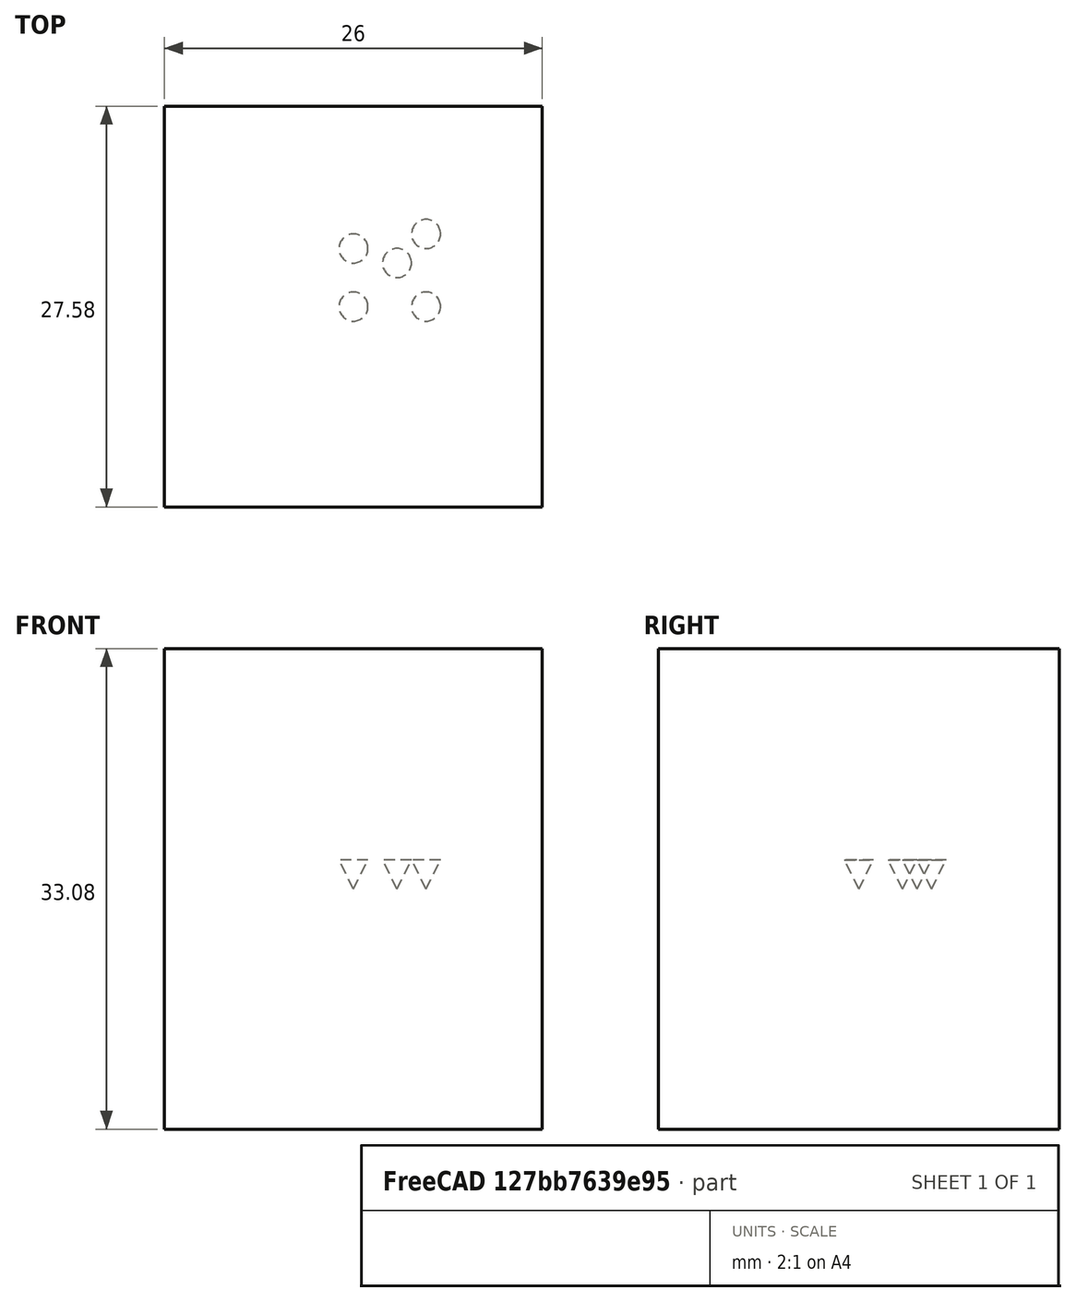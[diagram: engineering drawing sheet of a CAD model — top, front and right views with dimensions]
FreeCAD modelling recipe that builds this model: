
FCSTD DOCUMENT  (FreeCAD 1.0R39109 (Git))
Label: PointArray
License: All rights reserved
objects: App::DocumentObjectGroupPython×1251, Part::Vertex×5, Part::FeaturePython×2, App::Part×2, Part::Cone×1, Part::Compound×1
note: 9 computed .brp shape members not serialized (recipe doc carries the construction recipe); baked Part::Feature solids carry a one-line shape summary decoded from their .brp

FEATURE [App::DocumentObjectGroupPython] HALFPI  # scripted group (container) (typed FeaturePython)
  name = HALFPI
  value = pi/2.
FEATURE [App::DocumentObjectGroupPython] PI  # scripted group (container) (typed FeaturePython)
  name = PI
  value = 1.*pi
FEATURE [App::DocumentObjectGroupPython] TWOPI  # scripted group (container) (typed FeaturePython)
  name = TWOPI
  value = 2.*pi
FEATURE [App::DocumentObjectGroupPython] Constants  # scripted group (container) (typed FeaturePython)
  Group = -> [HALFPI,PI,TWOPI]
FEATURE [App::DocumentObjectGroupPython] Variables  # scripted group (container) (typed FeaturePython)
FEATURE [App::DocumentObjectGroupPython] Quantities  # scripted group (container) (typed FeaturePython)
FEATURE [App::DocumentObjectGroupPython] Isotopes  # scripted group (container) (typed FeaturePython)
FEATURE [App::DocumentObjectGroupPython] Elements  # scripted group (container) (typed FeaturePython)
FEATURE [App::DocumentObjectGroupPython] Matrix  # scripted group (container) (typed FeaturePython)
FEATURE [App::DocumentObjectGroupPython] Surfaces  # scripted group (container) (typed FeaturePython)
FEATURE [App::DocumentObjectGroupPython] Opticals  # scripted group (container) (typed FeaturePython)
  Group = -> [Matrix,Surfaces]
FEATURE [App::DocumentObjectGroupPython] G4Isotopes  # scripted group (container) (typed FeaturePython)
FEATURE [App::DocumentObjectGroupPython] H_element  # scripted group (container) (typed FeaturePython)
  Z = 1
  atom_value = 1.008
  formula = H
  name = H_element
FEATURE [App::DocumentObjectGroupPython] He_element  # scripted group (container) (typed FeaturePython)
  Z = 2
  atom_value = 4.0026
  formula = He
  name = He_element
FEATURE [App::DocumentObjectGroupPython] Li_element  # scripted group (container) (typed FeaturePython)
  Z = 3
  atom_value = 6.94
  formula = Li
  name = Li_element
FEATURE [App::DocumentObjectGroupPython] Be_element  # scripted group (container) (typed FeaturePython)
  Z = 4
  atom_value = 9.01218
  formula = Be
  name = Be_element
FEATURE [App::DocumentObjectGroupPython] B_element  # scripted group (container) (typed FeaturePython)
  Z = 5
  atom_value = 10.81
  formula = B
  name = B_element
FEATURE [App::DocumentObjectGroupPython] C_element  # scripted group (container) (typed FeaturePython)
  Z = 6
  atom_value = 12.011
  formula = C
  name = C_element
FEATURE [App::DocumentObjectGroupPython] N_element  # scripted group (container) (typed FeaturePython)
  Z = 7
  atom_value = 14.007
  formula = N
  name = N_element
FEATURE [App::DocumentObjectGroupPython] O_element  # scripted group (container) (typed FeaturePython)
  Z = 8
  atom_value = 15.999
  formula = O
  name = O_element
FEATURE [App::DocumentObjectGroupPython] F_element  # scripted group (container) (typed FeaturePython)
  Z = 9
  atom_value = 18.9984
  formula = F
  name = F_element
FEATURE [App::DocumentObjectGroupPython] Ne_element  # scripted group (container) (typed FeaturePython)
  Z = 10
  atom_value = 20.1797
  formula = Ne
  name = Ne_element
FEATURE [App::DocumentObjectGroupPython] Na_element  # scripted group (container) (typed FeaturePython)
  Z = 11
  atom_value = 22.9898
  formula = Na
  name = Na_element
FEATURE [App::DocumentObjectGroupPython] Mg_element  # scripted group (container) (typed FeaturePython)
  Z = 12
  atom_value = 24.305
  formula = Mg
  name = Mg_element
FEATURE [App::DocumentObjectGroupPython] Al_element  # scripted group (container) (typed FeaturePython)
  Z = 13
  atom_value = 26.9815
  formula = Al
  name = Al_element
FEATURE [App::DocumentObjectGroupPython] Si_element  # scripted group (container) (typed FeaturePython)
  Z = 14
  atom_value = 28.085
  formula = Si
  name = Si_element
FEATURE [App::DocumentObjectGroupPython] P_element  # scripted group (container) (typed FeaturePython)
  Z = 15
  atom_value = 30.9738
  formula = P
  name = P_element
FEATURE [App::DocumentObjectGroupPython] S_element  # scripted group (container) (typed FeaturePython)
  Z = 16
  atom_value = 32.06
  formula = S
  name = S_element
FEATURE [App::DocumentObjectGroupPython] Cl_element  # scripted group (container) (typed FeaturePython)
  Z = 17
  atom_value = 35.45
  formula = Cl
  name = Cl_element
FEATURE [App::DocumentObjectGroupPython] Ar_element  # scripted group (container) (typed FeaturePython)
  Z = 18
  atom_value = 39.95
  formula = Ar
  name = Ar_element
FEATURE [App::DocumentObjectGroupPython] K_element  # scripted group (container) (typed FeaturePython)
  Z = 19
  atom_value = 39.0983
  formula = K
  name = K_element
FEATURE [App::DocumentObjectGroupPython] Ca_element  # scripted group (container) (typed FeaturePython)
  Z = 20
  atom_value = 40.078
  formula = Ca
  name = Ca_element
FEATURE [App::DocumentObjectGroupPython] Sc_element  # scripted group (container) (typed FeaturePython)
  Z = 21
  atom_value = 44.9559
  formula = Sc
  name = Sc_element
FEATURE [App::DocumentObjectGroupPython] Ti_element  # scripted group (container) (typed FeaturePython)
  Z = 22
  atom_value = 47.867
  formula = Ti
  name = Ti_element
FEATURE [App::DocumentObjectGroupPython] V_element  # scripted group (container) (typed FeaturePython)
  Z = 23
  atom_value = 50.9415
  formula = V
  name = V_element
FEATURE [App::DocumentObjectGroupPython] Cr_element  # scripted group (container) (typed FeaturePython)
  Z = 24
  atom_value = 51.9961
  formula = Cr
  name = Cr_element
FEATURE [App::DocumentObjectGroupPython] Mn_element  # scripted group (container) (typed FeaturePython)
  Z = 25
  atom_value = 54.938
  formula = Mn
  name = Mn_element
FEATURE [App::DocumentObjectGroupPython] Fe_element  # scripted group (container) (typed FeaturePython)
  Z = 26
  atom_value = 55.845
  formula = Fe
  name = Fe_element
FEATURE [App::DocumentObjectGroupPython] Co_element  # scripted group (container) (typed FeaturePython)
  Z = 27
  atom_value = 58.9332
  formula = Co
  name = Co_element
FEATURE [App::DocumentObjectGroupPython] Ni_element  # scripted group (container) (typed FeaturePython)
  Z = 28
  atom_value = 58.6934
  formula = Ni
  name = Ni_element
FEATURE [App::DocumentObjectGroupPython] Cu_element  # scripted group (container) (typed FeaturePython)
  Z = 29
  atom_value = 63.546
  formula = Cu
  name = Cu_element
FEATURE [App::DocumentObjectGroupPython] Zn_element  # scripted group (container) (typed FeaturePython)
  Z = 30
  atom_value = 65.38
  formula = Zn
  name = Zn_element
FEATURE [App::DocumentObjectGroupPython] Ga_element  # scripted group (container) (typed FeaturePython)
  Z = 31
  atom_value = 69.723
  formula = Ga
  name = Ga_element
FEATURE [App::DocumentObjectGroupPython] Ge_element  # scripted group (container) (typed FeaturePython)
  Z = 32
  atom_value = 72.63
  formula = Ge
  name = Ge_element
FEATURE [App::DocumentObjectGroupPython] As_element  # scripted group (container) (typed FeaturePython)
  Z = 33
  atom_value = 74.9216
  formula = As
  name = As_element
FEATURE [App::DocumentObjectGroupPython] Se_element  # scripted group (container) (typed FeaturePython)
  Z = 34
  atom_value = 78.971
  formula = Se
  name = Se_element
FEATURE [App::DocumentObjectGroupPython] Br_element  # scripted group (container) (typed FeaturePython)
  Z = 35
  atom_value = 79.904
  formula = Br
  name = Br_element
FEATURE [App::DocumentObjectGroupPython] Kr_element  # scripted group (container) (typed FeaturePython)
  Z = 36
  atom_value = 83.798
  formula = Kr
  name = Kr_element
FEATURE [App::DocumentObjectGroupPython] Rb_element  # scripted group (container) (typed FeaturePython)
  Z = 37
  atom_value = 85.4678
  formula = Rb
  name = Rb_element
FEATURE [App::DocumentObjectGroupPython] Sr_element  # scripted group (container) (typed FeaturePython)
  Z = 38
  atom_value = 87.62
  formula = Sr
  name = Sr_element
FEATURE [App::DocumentObjectGroupPython] Y_element  # scripted group (container) (typed FeaturePython)
  Z = 39
  atom_value = 88.9058
  formula = Y
  name = Y_element
FEATURE [App::DocumentObjectGroupPython] Zr_element  # scripted group (container) (typed FeaturePython)
  Z = 40
  atom_value = 91.224
  formula = Zr
  name = Zr_element
FEATURE [App::DocumentObjectGroupPython] Nb_element  # scripted group (container) (typed FeaturePython)
  Z = 41
  atom_value = 92.9064
  formula = Nb
  name = Nb_element
FEATURE [App::DocumentObjectGroupPython] Mo_element  # scripted group (container) (typed FeaturePython)
  Z = 42
  atom_value = 95.95
  formula = Mo
  name = Mo_element
FEATURE [App::DocumentObjectGroupPython] Tc_element  # scripted group (container) (typed FeaturePython)
  Z = 43
  atom_value = 97
  formula = Tc
  name = Tc_element
FEATURE [App::DocumentObjectGroupPython] Ru_element  # scripted group (container) (typed FeaturePython)
  Z = 44
  atom_value = 101.07
  formula = Ru
  name = Ru_element
FEATURE [App::DocumentObjectGroupPython] Rh_element  # scripted group (container) (typed FeaturePython)
  Z = 45
  atom_value = 102.905
  formula = Rh
  name = Rh_element
FEATURE [App::DocumentObjectGroupPython] Pd_element  # scripted group (container) (typed FeaturePython)
  Z = 46
  atom_value = 106.42
  formula = Pd
  name = Pd_element
FEATURE [App::DocumentObjectGroupPython] Ag_element  # scripted group (container) (typed FeaturePython)
  Z = 47
  atom_value = 107.868
  formula = Ag
  name = Ag_element
FEATURE [App::DocumentObjectGroupPython] Cd_element  # scripted group (container) (typed FeaturePython)
  Z = 48
  atom_value = 112.414
  formula = Cd
  name = Cd_element
FEATURE [App::DocumentObjectGroupPython] In_element  # scripted group (container) (typed FeaturePython)
  Z = 49
  atom_value = 114.818
  formula = In
  name = In_element
FEATURE [App::DocumentObjectGroupPython] Sn_element  # scripted group (container) (typed FeaturePython)
  Z = 50
  atom_value = 118.71
  formula = Sn
  name = Sn_element
FEATURE [App::DocumentObjectGroupPython] Sb_element  # scripted group (container) (typed FeaturePython)
  Z = 51
  atom_value = 121.76
  formula = Sb
  name = Sb_element
FEATURE [App::DocumentObjectGroupPython] Te_element  # scripted group (container) (typed FeaturePython)
  Z = 52
  atom_value = 127.6
  formula = Te
  name = Te_element
FEATURE [App::DocumentObjectGroupPython] I_element  # scripted group (container) (typed FeaturePython)
  Z = 53
  atom_value = 126.904
  formula = I
  name = I_element
FEATURE [App::DocumentObjectGroupPython] Xe_element  # scripted group (container) (typed FeaturePython)
  Z = 54
  atom_value = 131.293
  formula = Xe
  name = Xe_element
FEATURE [App::DocumentObjectGroupPython] Cs_element  # scripted group (container) (typed FeaturePython)
  Z = 55
  atom_value = 132.905
  formula = Cs
  name = Cs_element
FEATURE [App::DocumentObjectGroupPython] Ba_element  # scripted group (container) (typed FeaturePython)
  Z = 56
  atom_value = 137.327
  formula = Ba
  name = Ba_element
FEATURE [App::DocumentObjectGroupPython] La_element  # scripted group (container) (typed FeaturePython)
  Z = 57
  atom_value = 138.905
  formula = La
  name = La_element
FEATURE [App::DocumentObjectGroupPython] Ce_element  # scripted group (container) (typed FeaturePython)
  Z = 58
  atom_value = 140.116
  formula = Ce
  name = Ce_element
FEATURE [App::DocumentObjectGroupPython] Pr_element  # scripted group (container) (typed FeaturePython)
  Z = 59
  atom_value = 140.908
  formula = Pr
  name = Pr_element
FEATURE [App::DocumentObjectGroupPython] Nd_element  # scripted group (container) (typed FeaturePython)
  Z = 60
  atom_value = 144.242
  formula = Nd
  name = Nd_element
FEATURE [App::DocumentObjectGroupPython] Pm_element  # scripted group (container) (typed FeaturePython)
  Z = 61
  atom_value = 145
  formula = Pm
  name = Pm_element
FEATURE [App::DocumentObjectGroupPython] Sm_element  # scripted group (container) (typed FeaturePython)
  Z = 62
  atom_value = 150.36
  formula = Sm
  name = Sm_element
FEATURE [App::DocumentObjectGroupPython] Eu_element  # scripted group (container) (typed FeaturePython)
  Z = 63
  atom_value = 151.964
  formula = Eu
  name = Eu_element
FEATURE [App::DocumentObjectGroupPython] Gd_element  # scripted group (container) (typed FeaturePython)
  Z = 64
  atom_value = 157.25
  formula = Gd
  name = Gd_element
FEATURE [App::DocumentObjectGroupPython] Tb_element  # scripted group (container) (typed FeaturePython)
  Z = 65
  atom_value = 158.925
  formula = Tb
  name = Tb_element
FEATURE [App::DocumentObjectGroupPython] Dy_element  # scripted group (container) (typed FeaturePython)
  Z = 66
  atom_value = 162.5
  formula = Dy
  name = Dy_element
FEATURE [App::DocumentObjectGroupPython] Ho_element  # scripted group (container) (typed FeaturePython)
  Z = 67
  atom_value = 164.93
  formula = Ho
  name = Ho_element
FEATURE [App::DocumentObjectGroupPython] Er_element  # scripted group (container) (typed FeaturePython)
  Z = 68
  atom_value = 167.259
  formula = Er
  name = Er_element
FEATURE [App::DocumentObjectGroupPython] Tm_element  # scripted group (container) (typed FeaturePython)
  Z = 69
  atom_value = 168.934
  formula = Tm
  name = Tm_element
FEATURE [App::DocumentObjectGroupPython] Yb_element  # scripted group (container) (typed FeaturePython)
  Z = 70
  atom_value = 173.045
  formula = Yb
  name = Yb_element
FEATURE [App::DocumentObjectGroupPython] Lu_element  # scripted group (container) (typed FeaturePython)
  Z = 71
  atom_value = 174.967
  formula = Lu
  name = Lu_element
FEATURE [App::DocumentObjectGroupPython] Hf_element  # scripted group (container) (typed FeaturePython)
  Z = 72
  atom_value = 178.49
  formula = Hf
  name = Hf_element
FEATURE [App::DocumentObjectGroupPython] Ta_element  # scripted group (container) (typed FeaturePython)
  Z = 73
  atom_value = 180.948
  formula = Ta
  name = Ta_element
FEATURE [App::DocumentObjectGroupPython] W_element  # scripted group (container) (typed FeaturePython)
  Z = 74
  atom_value = 183.84
  formula = W
  name = W_element
FEATURE [App::DocumentObjectGroupPython] Re_element  # scripted group (container) (typed FeaturePython)
  Z = 75
  atom_value = 186.207
  formula = Re
  name = Re_element
FEATURE [App::DocumentObjectGroupPython] Os_element  # scripted group (container) (typed FeaturePython)
  Z = 76
  atom_value = 190.23
  formula = Os
  name = Os_element
FEATURE [App::DocumentObjectGroupPython] Ir_element  # scripted group (container) (typed FeaturePython)
  Z = 77
  atom_value = 192.217
  formula = Ir
  name = Ir_element
FEATURE [App::DocumentObjectGroupPython] Pt_element  # scripted group (container) (typed FeaturePython)
  Z = 78
  atom_value = 195.084
  formula = Pt
  name = Pt_element
FEATURE [App::DocumentObjectGroupPython] Au_element  # scripted group (container) (typed FeaturePython)
  Z = 79
  atom_value = 196.967
  formula = Au
  name = Au_element
FEATURE [App::DocumentObjectGroupPython] Hg_element  # scripted group (container) (typed FeaturePython)
  Z = 80
  atom_value = 200.592
  formula = Hg
  name = Hg_element
FEATURE [App::DocumentObjectGroupPython] Tl_element  # scripted group (container) (typed FeaturePython)
  Z = 81
  atom_value = 204.38
  formula = Tl
  name = Tl_element
FEATURE [App::DocumentObjectGroupPython] Pb_element  # scripted group (container) (typed FeaturePython)
  Z = 82
  atom_value = 207.2
  formula = Pb
  name = Pb_element
FEATURE [App::DocumentObjectGroupPython] Bi_element  # scripted group (container) (typed FeaturePython)
  Z = 83
  atom_value = 208.98
  formula = Bi
  name = Bi_element
FEATURE [App::DocumentObjectGroupPython] Po_element  # scripted group (container) (typed FeaturePython)
  Z = 84
  atom_value = 209
  formula = Po
  name = Po_element
FEATURE [App::DocumentObjectGroupPython] At_element  # scripted group (container) (typed FeaturePython)
  Z = 85
  atom_value = 210
  formula = At
  name = At_element
FEATURE [App::DocumentObjectGroupPython] Rn_element  # scripted group (container) (typed FeaturePython)
  Z = 86
  atom_value = 222
  formula = Rn
  name = Rn_element
FEATURE [App::DocumentObjectGroupPython] Fr_element  # scripted group (container) (typed FeaturePython)
  Z = 87
  atom_value = 223
  formula = Fr
  name = Fr_element
FEATURE [App::DocumentObjectGroupPython] Ra_element  # scripted group (container) (typed FeaturePython)
  Z = 88
  atom_value = 226
  formula = Ra
  name = Ra_element
FEATURE [App::DocumentObjectGroupPython] Ac_element  # scripted group (container) (typed FeaturePython)
  Z = 89
  atom_value = 227
  formula = Ac
  name = Ac_element
FEATURE [App::DocumentObjectGroupPython] Th_element  # scripted group (container) (typed FeaturePython)
  Z = 90
  atom_value = 232.038
  formula = Th
  name = Th_element
FEATURE [App::DocumentObjectGroupPython] Pa_element  # scripted group (container) (typed FeaturePython)
  Z = 91
  atom_value = 231.036
  formula = Pa
  name = Pa_element
FEATURE [App::DocumentObjectGroupPython] U_element  # scripted group (container) (typed FeaturePython)
  Z = 92
  atom_value = 238.029
  formula = U
  name = U_element
FEATURE [App::DocumentObjectGroupPython] Np_element  # scripted group (container) (typed FeaturePython)
  Z = 93
  atom_value = 237
  formula = Np
  name = Np_element
FEATURE [App::DocumentObjectGroupPython] Pu_element  # scripted group (container) (typed FeaturePython)
  Z = 94
  atom_value = 244
  formula = Pu
  name = Pu_element
FEATURE [App::DocumentObjectGroupPython] Am_element  # scripted group (container) (typed FeaturePython)
  Z = 95
  atom_value = 243
  formula = Am
  name = Am_element
FEATURE [App::DocumentObjectGroupPython] Cm_element  # scripted group (container) (typed FeaturePython)
  Z = 96
  atom_value = 247
  formula = Cm
  name = Cm_element
FEATURE [App::DocumentObjectGroupPython] Bk_element  # scripted group (container) (typed FeaturePython)
  Z = 97
  atom_value = 247
  formula = Bk
  name = Bk_element
FEATURE [App::DocumentObjectGroupPython] Cf_element  # scripted group (container) (typed FeaturePython)
  Z = 98
  atom_value = 251
  formula = Cf
  name = Cf_element
FEATURE [App::DocumentObjectGroupPython] G4Elements  # scripted group (container) (typed FeaturePython)
  Group = -> [H_element,He_element,Li_element,Be_element,B_element,C_element,N_element,O_element,F_element,Ne_element,Na_element,Mg_element,Al_element,Si_element,P_element,S_element,Cl_element,Ar_element,K_element,Ca_element,Sc_element,Ti_element,V_element,Cr_element,Mn_element,Fe_element,Co_element,Ni_element,Cu_element,Zn_element,Ga_element,Ge_element,As_element,Se_element,Br_element,Kr_element,Rb_element,+61 more]
FEATURE [App::DocumentObjectGroupPython] H_element001  label="H_element : 0.101"  # scripted group (container) (typed FeaturePython)
  n = 0.101327
FEATURE [App::DocumentObjectGroupPython] C_element001  label="C_element : 0.775"  # scripted group (container) (typed FeaturePython)
  n = 0.7755
FEATURE [App::DocumentObjectGroupPython] N_element001  label="N_element : 0.035"  # scripted group (container) (typed FeaturePython)
  n = 0.035057
FEATURE [App::DocumentObjectGroupPython] O_element001  label="O_element : 0.052"  # scripted group (container) (typed FeaturePython)
  n = 0.0523159
FEATURE [App::DocumentObjectGroupPython] F_element001  label="F_element : 0.017"  # scripted group (container) (typed FeaturePython)
  n = 0.017422
FEATURE [App::DocumentObjectGroupPython] Ca_element001  label="Ca_element : 0.018"  # scripted group (container) (typed FeaturePython)
  n = 0.018378
FEATURE [App::DocumentObjectGroupPython] G4_A_150_TISSUE  label="G4_A-150_TISSUE"  # scripted group (container) (typed FeaturePython)
  Dunit = g/cm3
  Dvalue = 1.127
  Group = -> [H_element001,C_element001,N_element001,O_element001,F_element001,Ca_element001]
  conduct = 2
  density = 1
  expand = 3
  formula = G4_A-150_TISSUE
  name = G4_A-150_TISSUE
  specific = 4
FEATURE [App::DocumentObjectGroupPython] C_element002  label="C_element : 3"  # scripted group (container) (typed FeaturePython)
  n = 3
  ref = C_element
FEATURE [App::DocumentObjectGroupPython] H_element002  label="H_element : 6"  # scripted group (container) (typed FeaturePython)
  n = 6
  ref = H_element
FEATURE [App::DocumentObjectGroupPython] O_element002  label="O_element : 1"  # scripted group (container) (typed FeaturePython)
  n = 1
  ref = O_element
FEATURE [App::DocumentObjectGroupPython] G4_ACETONE  # scripted group (container) (typed FeaturePython)
  Dunit = g/cm3
  Dvalue = 0.7899
  Group = -> [C_element002,H_element002,O_element002]
  conduct = 2
  density = 1
  expand = 3
  formula = G4_ACETONE
  name = G4_ACETONE
  specific = 4
FEATURE [App::DocumentObjectGroupPython] C_element003  label="C_element : 2"  # scripted group (container) (typed FeaturePython)
  n = 2
  ref = C_element
FEATURE [App::DocumentObjectGroupPython] H_element003  label="H_element : 2"  # scripted group (container) (typed FeaturePython)
  n = 2
  ref = H_element
FEATURE [App::DocumentObjectGroupPython] G4_ACETYLENE  # scripted group (container) (typed FeaturePython)
  Dunit = g/cm3
  Dvalue = 0.0010967
  Group = -> [C_element003,H_element003]
  conduct = 2
  density = 1
  expand = 3
  formula = G4_ACETYLENE
  name = G4_ACETYLENE
  specific = 4
FEATURE [App::DocumentObjectGroupPython] C_element004  label="C_element : 5"  # scripted group (container) (typed FeaturePython)
  n = 5
  ref = C_element
FEATURE [App::DocumentObjectGroupPython] H_element004  label="H_element : 5"  # scripted group (container) (typed FeaturePython)
  n = 5
  ref = H_element
FEATURE [App::DocumentObjectGroupPython] N_element002  label="N_element : 5"  # scripted group (container) (typed FeaturePython)
  n = 5
  ref = N_element
FEATURE [App::DocumentObjectGroupPython] G4_ADENINE  # scripted group (container) (typed FeaturePython)
  Dunit = g/cm3
  Dvalue = 1.6
  Group = -> [C_element004,H_element004,N_element002]
  conduct = 2
  density = 1
  expand = 3
  formula = G4_ADENINE
  name = G4_ADENINE
  specific = 4
FEATURE [App::DocumentObjectGroupPython] H_element005  label="H_element : 0.114"  # scripted group (container) (typed FeaturePython)
  n = 0.114
FEATURE [App::DocumentObjectGroupPython] C_element005  label="C_element : 0.598"  # scripted group (container) (typed FeaturePython)
  n = 0.598
FEATURE [App::DocumentObjectGroupPython] N_element003  label="N_element : 0.007"  # scripted group (container) (typed FeaturePython)
  n = 0.007
FEATURE [App::DocumentObjectGroupPython] O_element003  label="O_element : 0.278"  # scripted group (container) (typed FeaturePython)
  n = 0.278
FEATURE [App::DocumentObjectGroupPython] Na_element001  label="Na_element : 0.001"  # scripted group (container) (typed FeaturePython)
  n = 0.001
FEATURE [App::DocumentObjectGroupPython] S_element001  label="S_element : 0.001"  # scripted group (container) (typed FeaturePython)
  n = 0.001
FEATURE [App::DocumentObjectGroupPython] Cl_element001  label="Cl_element : 0.001"  # scripted group (container) (typed FeaturePython)
  n = 0.001
FEATURE [App::DocumentObjectGroupPython] G4_ADIPOSE_TISSUE_ICRP  # scripted group (container) (typed FeaturePython)
  Dunit = g/cm3
  Dvalue = 0.95
  Group = -> [H_element005,C_element005,N_element003,O_element003,Na_element001,S_element001,Cl_element001]
  conduct = 2
  density = 1
  expand = 3
  formula = G4_ADIPOSE_TISSUE_ICRP
  name = G4_ADIPOSE_TISSUE_ICRP
  specific = 4
FEATURE [App::DocumentObjectGroupPython] C_element006  label="C_element : 0.000"  # scripted group (container) (typed FeaturePython)
  n = 0.000124
FEATURE [App::DocumentObjectGroupPython] N_element004  label="N_element : 0.755"  # scripted group (container) (typed FeaturePython)
  n = 0.755268
FEATURE [App::DocumentObjectGroupPython] O_element004  label="O_element : 0.232"  # scripted group (container) (typed FeaturePython)
  n = 0.231781
FEATURE [App::DocumentObjectGroupPython] Ar_element001  label="Ar_element : 0.013"  # scripted group (container) (typed FeaturePython)
  n = 0.012827
FEATURE [App::DocumentObjectGroupPython] G4_AIR  # scripted group (container) (typed FeaturePython)
  Dunit = g/cm3
  Dvalue = 0.00120479
  Group = -> [C_element006,N_element004,O_element004,Ar_element001]
  conduct = 2
  density = 1
  expand = 3
  formula = G4_AIR
  name = G4_AIR
  specific = 4
FEATURE [App::DocumentObjectGroupPython] C_element007  label="C_element : 006"  # scripted group (container) (typed FeaturePython)
  n = 3
  ref = C_element
FEATURE [App::DocumentObjectGroupPython] H_element006  label="H_element : 7"  # scripted group (container) (typed FeaturePython)
  n = 7
  ref = H_element
FEATURE [App::DocumentObjectGroupPython] N_element005  label="N_element : 1"  # scripted group (container) (typed FeaturePython)
  n = 1
  ref = N_element
FEATURE [App::DocumentObjectGroupPython] O_element005  label="O_element : 2"  # scripted group (container) (typed FeaturePython)
  n = 2
  ref = O_element
FEATURE [App::DocumentObjectGroupPython] G4_ALANINE  # scripted group (container) (typed FeaturePython)
  Dunit = g/cm3
  Dvalue = 1.42
  Group = -> [C_element007,H_element006,N_element005,O_element005]
  conduct = 2
  density = 1
  expand = 3
  formula = G4_ALANINE
  name = G4_ALANINE
  specific = 4
FEATURE [App::DocumentObjectGroupPython] Al_element001  label="Al_element : 2"  # scripted group (container) (typed FeaturePython)
  n = 2
  ref = Al_element
FEATURE [App::DocumentObjectGroupPython] O_element006  label="O_element : 3"  # scripted group (container) (typed FeaturePython)
  n = 3
  ref = O_element
FEATURE [App::DocumentObjectGroupPython] G4_ALUMINUM_OXIDE  # scripted group (container) (typed FeaturePython)
  Dunit = g/cm3
  Dvalue = 3.97
  Group = -> [Al_element001,O_element006]
  conduct = 2
  density = 1
  expand = 3
  formula = G4_ALUMINUM_OXIDE
  name = G4_ALUMINUM_OXIDE
  specific = 4
FEATURE [App::DocumentObjectGroupPython] H_element007  label="H_element : 0.106"  # scripted group (container) (typed FeaturePython)
  n = 0.10593
FEATURE [App::DocumentObjectGroupPython] C_element008  label="C_element : 0.789"  # scripted group (container) (typed FeaturePython)
  n = 0.788974
FEATURE [App::DocumentObjectGroupPython] O_element007  label="O_element : 0.105"  # scripted group (container) (typed FeaturePython)
  n = 0.105096
FEATURE [App::DocumentObjectGroupPython] G4_AMBER  # scripted group (container) (typed FeaturePython)
  Dunit = g/cm3
  Dvalue = 1.1
  Group = -> [H_element007,C_element008,O_element007]
  conduct = 2
  density = 1
  expand = 3
  formula = G4_AMBER
  name = G4_AMBER
  specific = 4
FEATURE [App::DocumentObjectGroupPython] N_element006  label="N_element : 006"  # scripted group (container) (typed FeaturePython)
  n = 1
  ref = N_element
FEATURE [App::DocumentObjectGroupPython] H_element008  label="H_element : 3"  # scripted group (container) (typed FeaturePython)
  n = 3
  ref = H_element
FEATURE [App::DocumentObjectGroupPython] G4_AMMONIA  # scripted group (container) (typed FeaturePython)
  Dunit = g/cm3
  Dvalue = 0.000826019
  Group = -> [N_element006,H_element008]
  conduct = 2
  density = 1
  expand = 3
  formula = G4_AMMONIA
  name = G4_AMMONIA
  specific = 4
FEATURE [App::DocumentObjectGroupPython] C_element009  label="C_element : 6"  # scripted group (container) (typed FeaturePython)
  n = 6
  ref = C_element
FEATURE [App::DocumentObjectGroupPython] H_element009  label="H_element : 008"  # scripted group (container) (typed FeaturePython)
  n = 7
  ref = H_element
FEATURE [App::DocumentObjectGroupPython] N_element007  label="N_element : 007"  # scripted group (container) (typed FeaturePython)
  n = 1
  ref = N_element
FEATURE [App::DocumentObjectGroupPython] G4_ANILINE  # scripted group (container) (typed FeaturePython)
  Dunit = g/cm3
  Dvalue = 1.0235
  Group = -> [C_element009,H_element009,N_element007]
  conduct = 2
  density = 1
  expand = 3
  formula = G4_ANILINE
  name = G4_ANILINE
  specific = 4
FEATURE [App::DocumentObjectGroupPython] C_element010  label="C_element : 14"  # scripted group (container) (typed FeaturePython)
  n = 14
  ref = C_element
FEATURE [App::DocumentObjectGroupPython] H_element010  label="H_element : 10"  # scripted group (container) (typed FeaturePython)
  n = 10
  ref = H_element
FEATURE [App::DocumentObjectGroupPython] G4_ANTHRACENE  # scripted group (container) (typed FeaturePython)
  Dunit = g/cm3
  Dvalue = 1.283
  Group = -> [C_element010,H_element010]
  conduct = 2
  density = 1
  expand = 3
  formula = G4_ANTHRACENE
  name = G4_ANTHRACENE
  specific = 4
FEATURE [App::DocumentObjectGroupPython] H_element011  label="H_element : 0.065"  # scripted group (container) (typed FeaturePython)
  n = 0.0654709
FEATURE [App::DocumentObjectGroupPython] C_element011  label="C_element : 0.537"  # scripted group (container) (typed FeaturePython)
  n = 0.536944
FEATURE [App::DocumentObjectGroupPython] N_element008  label="N_element : 0.021"  # scripted group (container) (typed FeaturePython)
  n = 0.0215
FEATURE [App::DocumentObjectGroupPython] O_element008  label="O_element : 0.032"  # scripted group (container) (typed FeaturePython)
  n = 0.032085
FEATURE [App::DocumentObjectGroupPython] F_element002  label="F_element : 0.167"  # scripted group (container) (typed FeaturePython)
  n = 0.167411
FEATURE [App::DocumentObjectGroupPython] Ca_element002  label="Ca_element : 0.177"  # scripted group (container) (typed FeaturePython)
  n = 0.176589
FEATURE [App::DocumentObjectGroupPython] G4_B_100_BONE  label="G4_B-100_BONE"  # scripted group (container) (typed FeaturePython)
  Dunit = g/cm3
  Dvalue = 1.45
  Group = -> [H_element011,C_element011,N_element008,O_element008,F_element002,Ca_element002]
  conduct = 2
  density = 1
  expand = 3
  formula = G4_B-100_BONE
  name = G4_B-100_BONE
  specific = 4
FEATURE [App::DocumentObjectGroupPython] H_element012  label="H_element : 0.057"  # scripted group (container) (typed FeaturePython)
  n = 0.057441
FEATURE [App::DocumentObjectGroupPython] C_element012  label="C_element : 0.790"  # scripted group (container) (typed FeaturePython)
  n = 0.774591
FEATURE [App::DocumentObjectGroupPython] O_element009  label="O_element : 0.168"  # scripted group (container) (typed FeaturePython)
  n = 0.167968
FEATURE [App::DocumentObjectGroupPython] G4_BAKELITE  # scripted group (container) (typed FeaturePython)
  Dunit = g/cm3
  Dvalue = 1.25
  Group = -> [H_element012,C_element012,O_element009]
  conduct = 2
  density = 1
  expand = 3
  formula = G4_BAKELITE
  name = G4_BAKELITE
  specific = 4
FEATURE [App::DocumentObjectGroupPython] Ba_element001  label="Ba_element : 1"  # scripted group (container) (typed FeaturePython)
  n = 1
  ref = Ba_element
FEATURE [App::DocumentObjectGroupPython] F_element003  label="F_element : 2"  # scripted group (container) (typed FeaturePython)
  n = 2
  ref = F_element
FEATURE [App::DocumentObjectGroupPython] G4_BARIUM_FLUORIDE  # scripted group (container) (typed FeaturePython)
  Dunit = g/cm3
  Dvalue = 4.89
  Group = -> [Ba_element001,F_element003]
  conduct = 2
  density = 1
  expand = 3
  formula = G4_BARIUM_FLUORIDE
  name = G4_BARIUM_FLUORIDE
  specific = 4
FEATURE [App::DocumentObjectGroupPython] Ba_element002  label="Ba_element : 002"  # scripted group (container) (typed FeaturePython)
  n = 1
  ref = Ba_element
FEATURE [App::DocumentObjectGroupPython] S_element002  label="S_element : 1"  # scripted group (container) (typed FeaturePython)
  n = 1
  ref = S_element
FEATURE [App::DocumentObjectGroupPython] O_element010  label="O_element : 4"  # scripted group (container) (typed FeaturePython)
  n = 4
  ref = O_element
FEATURE [App::DocumentObjectGroupPython] G4_BARIUM_SULFATE  # scripted group (container) (typed FeaturePython)
  Dunit = g/cm3
  Dvalue = 4.5
  Group = -> [Ba_element002,S_element002,O_element010]
  conduct = 2
  density = 1
  expand = 3
  formula = G4_BARIUM_SULFATE
  name = G4_BARIUM_SULFATE
  specific = 4
FEATURE [App::DocumentObjectGroupPython] C_element013  label="C_element : 007"  # scripted group (container) (typed FeaturePython)
  n = 6
  ref = C_element
FEATURE [App::DocumentObjectGroupPython] H_element013  label="H_element : 009"  # scripted group (container) (typed FeaturePython)
  n = 6
  ref = H_element
FEATURE [App::DocumentObjectGroupPython] G4_BENZENE  # scripted group (container) (typed FeaturePython)
  Dunit = g/cm3
  Dvalue = 0.87865
  Group = -> [C_element013,H_element013]
  conduct = 2
  density = 1
  expand = 3
  formula = G4_BENZENE
  name = G4_BENZENE
  specific = 4
FEATURE [App::DocumentObjectGroupPython] Be_element001  label="Be_element : 1"  # scripted group (container) (typed FeaturePython)
  n = 1
  ref = Be_element
FEATURE [App::DocumentObjectGroupPython] O_element011  label="O_element : 005"  # scripted group (container) (typed FeaturePython)
  n = 1
  ref = O_element
FEATURE [App::DocumentObjectGroupPython] G4_BERYLLIUM_OXIDE  # scripted group (container) (typed FeaturePython)
  Dunit = g/cm3
  Dvalue = 3.01
  Group = -> [Be_element001,O_element011]
  conduct = 2
  density = 1
  expand = 3
  formula = G4_BERYLLIUM_OXIDE
  name = G4_BERYLLIUM_OXIDE
  specific = 4
FEATURE [App::DocumentObjectGroupPython] Bi_element001  label="Bi_element : 4"  # scripted group (container) (typed FeaturePython)
  n = 4
  ref = Bi_element
FEATURE [App::DocumentObjectGroupPython] Ge_element001  label="Ge_element : 3"  # scripted group (container) (typed FeaturePython)
  n = 3
  ref = Ge_element
FEATURE [App::DocumentObjectGroupPython] O_element012  label="O_element : 12"  # scripted group (container) (typed FeaturePython)
  n = 12
  ref = O_element
FEATURE [App::DocumentObjectGroupPython] G4_BGO  # scripted group (container) (typed FeaturePython)
  Dunit = g/cm3
  Dvalue = 7.13
  Group = -> [Bi_element001,Ge_element001,O_element012]
  conduct = 2
  density = 1
  expand = 3
  formula = G4_BGO
  name = G4_BGO
  specific = 4
FEATURE [App::DocumentObjectGroupPython] H_element014  label="H_element : 0.102"  # scripted group (container) (typed FeaturePython)
  n = 0.102
FEATURE [App::DocumentObjectGroupPython] C_element014  label="C_element : 0.110"  # scripted group (container) (typed FeaturePython)
  n = 0.11
FEATURE [App::DocumentObjectGroupPython] N_element009  label="N_element : 0.033"  # scripted group (container) (typed FeaturePython)
  n = 0.033
FEATURE [App::DocumentObjectGroupPython] O_element013  label="O_element : 0.745"  # scripted group (container) (typed FeaturePython)
  n = 0.745
FEATURE [App::DocumentObjectGroupPython] Na_element002  label="Na_element : 0.002"  # scripted group (container) (typed FeaturePython)
  n = 0.001
FEATURE [App::DocumentObjectGroupPython] P_element001  label="P_element : 0.001"  # scripted group (container) (typed FeaturePython)
  n = 0.001
FEATURE [App::DocumentObjectGroupPython] S_element003  label="S_element : 0.002"  # scripted group (container) (typed FeaturePython)
  n = 0.002
FEATURE [App::DocumentObjectGroupPython] Cl_element002  label="Cl_element : 0.003"  # scripted group (container) (typed FeaturePython)
  n = 0.003
FEATURE [App::DocumentObjectGroupPython] K_element001  label="K_element : 0.002"  # scripted group (container) (typed FeaturePython)
  n = 0.002
FEATURE [App::DocumentObjectGroupPython] Fe_element001  label="Fe_element : 0.001"  # scripted group (container) (typed FeaturePython)
  n = 0.001
FEATURE [App::DocumentObjectGroupPython] G4_BLOOD_ICRP  # scripted group (container) (typed FeaturePython)
  Dunit = g/cm3
  Dvalue = 1.06
  Group = -> [H_element014,C_element014,N_element009,O_element013,Na_element002,P_element001,S_element003,Cl_element002,K_element001,Fe_element001]
  conduct = 2
  density = 1
  expand = 3
  formula = G4_BLOOD_ICRP
  name = G4_BLOOD_ICRP
  specific = 4
FEATURE [App::DocumentObjectGroupPython] H_element015  label="H_element : 0.064"  # scripted group (container) (typed FeaturePython)
  n = 0.064
FEATURE [App::DocumentObjectGroupPython] C_element015  label="C_element : 0.278"  # scripted group (container) (typed FeaturePython)
  n = 0.278
FEATURE [App::DocumentObjectGroupPython] N_element010  label="N_element : 0.027"  # scripted group (container) (typed FeaturePython)
  n = 0.027
FEATURE [App::DocumentObjectGroupPython] O_element014  label="O_element : 0.410"  # scripted group (container) (typed FeaturePython)
  n = 0.41
FEATURE [App::DocumentObjectGroupPython] Mg_element001  label="Mg_element : 0.002"  # scripted group (container) (typed FeaturePython)
  n = 0.002
FEATURE [App::DocumentObjectGroupPython] P_element002  label="P_element : 0.070"  # scripted group (container) (typed FeaturePython)
  n = 0.07
FEATURE [App::DocumentObjectGroupPython] S_element004  label="S_element : 0.003"  # scripted group (container) (typed FeaturePython)
  n = 0.002
FEATURE [App::DocumentObjectGroupPython] Ca_element003  label="Ca_element : 0.147"  # scripted group (container) (typed FeaturePython)
  n = 0.147
FEATURE [App::DocumentObjectGroupPython] G4_BONE_COMPACT_ICRU  # scripted group (container) (typed FeaturePython)
  Dunit = g/cm3
  Dvalue = 1.85
  Group = -> [H_element015,C_element015,N_element010,O_element014,Mg_element001,P_element002,S_element004,Ca_element003]
  conduct = 2
  density = 1
  expand = 3
  formula = G4_BONE_COMPACT_ICRU
  name = G4_BONE_COMPACT_ICRU
  specific = 4
FEATURE [App::DocumentObjectGroupPython] H_element016  label="H_element : 0.034"  # scripted group (container) (typed FeaturePython)
  n = 0.034
FEATURE [App::DocumentObjectGroupPython] C_element016  label="C_element : 0.155"  # scripted group (container) (typed FeaturePython)
  n = 0.155
FEATURE [App::DocumentObjectGroupPython] N_element011  label="N_element : 0.042"  # scripted group (container) (typed FeaturePython)
  n = 0.042
FEATURE [App::DocumentObjectGroupPython] O_element015  label="O_element : 0.435"  # scripted group (container) (typed FeaturePython)
  n = 0.435
FEATURE [App::DocumentObjectGroupPython] Na_element003  label="Na_element : 0.003"  # scripted group (container) (typed FeaturePython)
  n = 0.001
FEATURE [App::DocumentObjectGroupPython] Mg_element002  label="Mg_element : 0.003"  # scripted group (container) (typed FeaturePython)
  n = 0.002
FEATURE [App::DocumentObjectGroupPython] P_element003  label="P_element : 0.103"  # scripted group (container) (typed FeaturePython)
  n = 0.103
FEATURE [App::DocumentObjectGroupPython] S_element005  label="S_element : 0.004"  # scripted group (container) (typed FeaturePython)
  n = 0.003
FEATURE [App::DocumentObjectGroupPython] Ca_element004  label="Ca_element : 0.225"  # scripted group (container) (typed FeaturePython)
  n = 0.225
FEATURE [App::DocumentObjectGroupPython] G4_BONE_CORTICAL_ICRP  # scripted group (container) (typed FeaturePython)
  Dunit = g/cm3
  Dvalue = 1.92
  Group = -> [H_element016,C_element016,N_element011,O_element015,Na_element003,Mg_element002,P_element003,S_element005,Ca_element004]
  conduct = 2
  density = 1
  expand = 3
  formula = G4_BONE_CORTICAL_ICRP
  name = G4_BONE_CORTICAL_ICRP
  specific = 4
FEATURE [App::DocumentObjectGroupPython] B_element001  label="B_element : 4"  # scripted group (container) (typed FeaturePython)
  n = 4
  ref = B_element
FEATURE [App::DocumentObjectGroupPython] C_element017  label="C_element : 1"  # scripted group (container) (typed FeaturePython)
  n = 1
  ref = C_element
FEATURE [App::DocumentObjectGroupPython] G4_BORON_CARBIDE  # scripted group (container) (typed FeaturePython)
  Dunit = g/cm3
  Dvalue = 2.52
  Group = -> [B_element001,C_element017]
  conduct = 2
  density = 1
  expand = 3
  formula = G4_BORON_CARBIDE
  name = G4_BORON_CARBIDE
  specific = 4
FEATURE [App::DocumentObjectGroupPython] B_element002  label="B_element : 2"  # scripted group (container) (typed FeaturePython)
  n = 2
  ref = B_element
FEATURE [App::DocumentObjectGroupPython] O_element016  label="O_element : 006"  # scripted group (container) (typed FeaturePython)
  n = 3
  ref = O_element
FEATURE [App::DocumentObjectGroupPython] G4_BORON_OXIDE  # scripted group (container) (typed FeaturePython)
  Dunit = g/cm3
  Dvalue = 1.812
  Group = -> [B_element002,O_element016]
  conduct = 2
  density = 1
  expand = 3
  formula = G4_BORON_OXIDE
  name = G4_BORON_OXIDE
  specific = 4
FEATURE [App::DocumentObjectGroupPython] H_element017  label="H_element : 0.107"  # scripted group (container) (typed FeaturePython)
  n = 0.107
FEATURE [App::DocumentObjectGroupPython] C_element018  label="C_element : 0.145"  # scripted group (container) (typed FeaturePython)
  n = 0.145
FEATURE [App::DocumentObjectGroupPython] N_element012  label="N_element : 0.022"  # scripted group (container) (typed FeaturePython)
  n = 0.022
FEATURE [App::DocumentObjectGroupPython] O_element017  label="O_element : 0.712"  # scripted group (container) (typed FeaturePython)
  n = 0.712
FEATURE [App::DocumentObjectGroupPython] Na_element004  label="Na_element : 0.004"  # scripted group (container) (typed FeaturePython)
  n = 0.002
FEATURE [App::DocumentObjectGroupPython] P_element004  label="P_element : 0.004"  # scripted group (container) (typed FeaturePython)
  n = 0.004
FEATURE [App::DocumentObjectGroupPython] S_element006  label="S_element : 0.005"  # scripted group (container) (typed FeaturePython)
  n = 0.002
FEATURE [App::DocumentObjectGroupPython] Cl_element003  label="Cl_element : 0.004"  # scripted group (container) (typed FeaturePython)
  n = 0.003
FEATURE [App::DocumentObjectGroupPython] K_element002  label="K_element : 0.003"  # scripted group (container) (typed FeaturePython)
  n = 0.003
FEATURE [App::DocumentObjectGroupPython] G4_BRAIN_ICRP  # scripted group (container) (typed FeaturePython)
  Dunit = g/cm3
  Dvalue = 1.04
  Group = -> [H_element017,C_element018,N_element012,O_element017,Na_element004,P_element004,S_element006,Cl_element003,K_element002]
  conduct = 2
  density = 1
  expand = 3
  formula = G4_BRAIN_ICRP
  name = G4_BRAIN_ICRP
  specific = 4
FEATURE [App::DocumentObjectGroupPython] C_element019  label="C_element : 4"  # scripted group (container) (typed FeaturePython)
  n = 4
  ref = C_element
FEATURE [App::DocumentObjectGroupPython] H_element018  label="H_element : 010"  # scripted group (container) (typed FeaturePython)
  n = 10
  ref = H_element
FEATURE [App::DocumentObjectGroupPython] G4_BUTANE  # scripted group (container) (typed FeaturePython)
  Dunit = g/cm3
  Dvalue = 0.00249343
  Group = -> [C_element019,H_element018]
  conduct = 2
  density = 1
  expand = 3
  formula = G4_BUTANE
  name = G4_BUTANE
  specific = 4
FEATURE [App::DocumentObjectGroupPython] C_element020  label="C_element : 008"  # scripted group (container) (typed FeaturePython)
  n = 4
  ref = C_element
FEATURE [App::DocumentObjectGroupPython] H_element019  label="H_element : 011"  # scripted group (container) (typed FeaturePython)
  n = 10
  ref = H_element
FEATURE [App::DocumentObjectGroupPython] O_element018  label="O_element : 007"  # scripted group (container) (typed FeaturePython)
  n = 1
  ref = O_element
FEATURE [App::DocumentObjectGroupPython] G4_N_BUTYL_ALCOHOL  label="G4_N-BUTYL_ALCOHOL"  # scripted group (container) (typed FeaturePython)
  Dunit = g/cm3
  Dvalue = 0.8098
  Group = -> [C_element020,H_element019,O_element018]
  conduct = 2
  density = 1
  expand = 3
  formula = G4_N-BUTYL_ALCOHOL
  name = G4_N-BUTYL_ALCOHOL
  specific = 4
FEATURE [App::DocumentObjectGroupPython] H_element020  label="H_element : 0.025"  # scripted group (container) (typed FeaturePython)
  n = 0.02468
FEATURE [App::DocumentObjectGroupPython] C_element021  label="C_element : 0.502"  # scripted group (container) (typed FeaturePython)
  n = 0.501611
FEATURE [App::DocumentObjectGroupPython] O_element019  label="O_element : 0.005"  # scripted group (container) (typed FeaturePython)
  n = 0.004527
FEATURE [App::DocumentObjectGroupPython] F_element004  label="F_element : 0.465"  # scripted group (container) (typed FeaturePython)
  n = 0.465209
FEATURE [App::DocumentObjectGroupPython] Si_element001  label="Si_element : 0.004"  # scripted group (container) (typed FeaturePython)
  n = 0.003973
FEATURE [App::DocumentObjectGroupPython] G4_C_552  label="G4_C-552"  # scripted group (container) (typed FeaturePython)
  Dunit = g/cm3
  Dvalue = 1.76
  Group = -> [H_element020,C_element021,O_element019,F_element004,Si_element001]
  conduct = 2
  density = 1
  expand = 3
  formula = G4_C-552
  name = G4_C-552
  specific = 4
FEATURE [App::DocumentObjectGroupPython] Cd_element001  label="Cd_element : 1"  # scripted group (container) (typed FeaturePython)
  n = 1
  ref = Cd_element
FEATURE [App::DocumentObjectGroupPython] Te_element001  label="Te_element : 1"  # scripted group (container) (typed FeaturePython)
  n = 1
  ref = Te_element
FEATURE [App::DocumentObjectGroupPython] G4_CADMIUM_TELLURIDE  # scripted group (container) (typed FeaturePython)
  Dunit = g/cm3
  Dvalue = 6.2
  Group = -> [Cd_element001,Te_element001]
  conduct = 2
  density = 1
  expand = 3
  formula = G4_CADMIUM_TELLURIDE
  name = G4_CADMIUM_TELLURIDE
  specific = 4
FEATURE [App::DocumentObjectGroupPython] Cd_element002  label="Cd_element : 002"  # scripted group (container) (typed FeaturePython)
  n = 1
  ref = Cd_element
FEATURE [App::DocumentObjectGroupPython] W_element001  label="W_element : 1"  # scripted group (container) (typed FeaturePython)
  n = 1
  ref = W_element
FEATURE [App::DocumentObjectGroupPython] O_element020  label="O_element : 008"  # scripted group (container) (typed FeaturePython)
  n = 4
  ref = O_element
FEATURE [App::DocumentObjectGroupPython] G4_CADMIUM_TUNGSTATE  # scripted group (container) (typed FeaturePython)
  Dunit = g/cm3
  Dvalue = 7.9
  Group = -> [Cd_element002,W_element001,O_element020]
  conduct = 2
  density = 1
  expand = 3
  formula = G4_CADMIUM_TUNGSTATE
  name = G4_CADMIUM_TUNGSTATE
  specific = 4
FEATURE [App::DocumentObjectGroupPython] Ca_element005  label="Ca_element : 1"  # scripted group (container) (typed FeaturePython)
  n = 1
  ref = Ca_element
FEATURE [App::DocumentObjectGroupPython] C_element022  label="C_element : 009"  # scripted group (container) (typed FeaturePython)
  n = 1
  ref = C_element
FEATURE [App::DocumentObjectGroupPython] O_element021  label="O_element : 009"  # scripted group (container) (typed FeaturePython)
  n = 3
  ref = O_element
FEATURE [App::DocumentObjectGroupPython] G4_CALCIUM_CARBONATE  # scripted group (container) (typed FeaturePython)
  Dunit = g/cm3
  Dvalue = 2.8
  Group = -> [Ca_element005,C_element022,O_element021]
  conduct = 2
  density = 1
  expand = 3
  formula = G4_CALCIUM_CARBONATE
  name = G4_CALCIUM_CARBONATE
  specific = 4
FEATURE [App::DocumentObjectGroupPython] Ca_element006  label="Ca_element : 002"  # scripted group (container) (typed FeaturePython)
  n = 1
  ref = Ca_element
FEATURE [App::DocumentObjectGroupPython] F_element005  label="F_element : 003"  # scripted group (container) (typed FeaturePython)
  n = 2
  ref = F_element
FEATURE [App::DocumentObjectGroupPython] G4_CALCIUM_FLUORIDE  # scripted group (container) (typed FeaturePython)
  Dunit = g/cm3
  Dvalue = 3.18
  Group = -> [Ca_element006,F_element005]
  conduct = 2
  density = 1
  expand = 3
  formula = G4_CALCIUM_FLUORIDE
  name = G4_CALCIUM_FLUORIDE
  specific = 4
FEATURE [App::DocumentObjectGroupPython] Ca_element007  label="Ca_element : 003"  # scripted group (container) (typed FeaturePython)
  n = 1
  ref = Ca_element
FEATURE [App::DocumentObjectGroupPython] O_element022  label="O_element : 010"  # scripted group (container) (typed FeaturePython)
  n = 1
  ref = O_element
FEATURE [App::DocumentObjectGroupPython] G4_CALCIUM_OXIDE  # scripted group (container) (typed FeaturePython)
  Dunit = g/cm3
  Dvalue = 3.3
  Group = -> [Ca_element007,O_element022]
  conduct = 2
  density = 1
  expand = 3
  formula = G4_CALCIUM_OXIDE
  name = G4_CALCIUM_OXIDE
  specific = 4
FEATURE [App::DocumentObjectGroupPython] Ca_element008  label="Ca_element : 004"  # scripted group (container) (typed FeaturePython)
  n = 1
  ref = Ca_element
FEATURE [App::DocumentObjectGroupPython] S_element007  label="S_element : 002"  # scripted group (container) (typed FeaturePython)
  n = 1
  ref = S_element
FEATURE [App::DocumentObjectGroupPython] O_element023  label="O_element : 011"  # scripted group (container) (typed FeaturePython)
  n = 4
  ref = O_element
FEATURE [App::DocumentObjectGroupPython] G4_CALCIUM_SULFATE  # scripted group (container) (typed FeaturePython)
  Dunit = g/cm3
  Dvalue = 2.96
  Group = -> [Ca_element008,S_element007,O_element023]
  conduct = 2
  density = 1
  expand = 3
  formula = G4_CALCIUM_SULFATE
  name = G4_CALCIUM_SULFATE
  specific = 4
FEATURE [App::DocumentObjectGroupPython] Ca_element009  label="Ca_element : 005"  # scripted group (container) (typed FeaturePython)
  n = 1
  ref = Ca_element
FEATURE [App::DocumentObjectGroupPython] W_element002  label="W_element : 002"  # scripted group (container) (typed FeaturePython)
  n = 1
  ref = W_element
FEATURE [App::DocumentObjectGroupPython] O_element024  label="O_element : 012"  # scripted group (container) (typed FeaturePython)
  n = 4
  ref = O_element
FEATURE [App::DocumentObjectGroupPython] G4_CALCIUM_TUNGSTATE  # scripted group (container) (typed FeaturePython)
  Dunit = g/cm3
  Dvalue = 6.062
  Group = -> [Ca_element009,W_element002,O_element024]
  conduct = 2
  density = 1
  expand = 3
  formula = G4_CALCIUM_TUNGSTATE
  name = G4_CALCIUM_TUNGSTATE
  specific = 4
FEATURE [App::DocumentObjectGroupPython] C_element023  label="C_element : 010"  # scripted group (container) (typed FeaturePython)
  n = 1
  ref = C_element
FEATURE [App::DocumentObjectGroupPython] O_element025  label="O_element : 013"  # scripted group (container) (typed FeaturePython)
  n = 2
  ref = O_element
FEATURE [App::DocumentObjectGroupPython] G4_CARBON_DIOXIDE  # scripted group (container) (typed FeaturePython)
  Dunit = g/cm3
  Dvalue = 0.00184212
  Group = -> [C_element023,O_element025]
  conduct = 2
  density = 1
  expand = 3
  formula = G4_CARBON_DIOXIDE
  name = G4_CARBON_DIOXIDE
  specific = 4
FEATURE [App::DocumentObjectGroupPython] C_element024  label="C_element : 011"  # scripted group (container) (typed FeaturePython)
  n = 1
  ref = C_element
FEATURE [App::DocumentObjectGroupPython] Cl_element004  label="Cl_element : 4"  # scripted group (container) (typed FeaturePython)
  n = 4
  ref = Cl_element
FEATURE [App::DocumentObjectGroupPython] G4_CARBON_TETRACHLORIDE  # scripted group (container) (typed FeaturePython)
  Dunit = g/cm3
  Dvalue = 1.594
  Group = -> [C_element024,Cl_element004]
  conduct = 2
  density = 1
  expand = 3
  formula = G4_CARBON_TETRACHLORIDE
  name = G4_CARBON_TETRACHLORIDE
  specific = 4
FEATURE [App::DocumentObjectGroupPython] C_element025  label="C_element : 012"  # scripted group (container) (typed FeaturePython)
  n = 6
  ref = C_element
FEATURE [App::DocumentObjectGroupPython] H_element021  label="H_element : 012"  # scripted group (container) (typed FeaturePython)
  n = 10
  ref = H_element
FEATURE [App::DocumentObjectGroupPython] O_element026  label="O_element : 5"  # scripted group (container) (typed FeaturePython)
  n = 5
  ref = O_element
FEATURE [App::DocumentObjectGroupPython] G4_CELLULOSE_CELLOPHANE  # scripted group (container) (typed FeaturePython)
  Dunit = g/cm3
  Dvalue = 1.42
  Group = -> [C_element025,H_element021,O_element026]
  conduct = 2
  density = 1
  expand = 3
  formula = G4_CELLULOSE_CELLOPHANE
  name = G4_CELLULOSE_CELLOPHANE
  specific = 4
FEATURE [App::DocumentObjectGroupPython] H_element022  label="H_element : 0.067"  # scripted group (container) (typed FeaturePython)
  n = 0.067125
FEATURE [App::DocumentObjectGroupPython] C_element026  label="C_element : 0.545"  # scripted group (container) (typed FeaturePython)
  n = 0.545403
FEATURE [App::DocumentObjectGroupPython] O_element027  label="O_element : 0.387"  # scripted group (container) (typed FeaturePython)
  n = 0.387472
FEATURE [App::DocumentObjectGroupPython] G4_CELLULOSE_BUTYRATE  # scripted group (container) (typed FeaturePython)
  Dunit = g/cm3
  Dvalue = 1.2
  Group = -> [H_element022,C_element026,O_element027]
  conduct = 2
  density = 1
  expand = 3
  formula = G4_CELLULOSE_BUTYRATE
  name = G4_CELLULOSE_BUTYRATE
  specific = 4
FEATURE [App::DocumentObjectGroupPython] H_element023  label="H_element : 0.029"  # scripted group (container) (typed FeaturePython)
  n = 0.029216
FEATURE [App::DocumentObjectGroupPython] C_element027  label="C_element : 0.271"  # scripted group (container) (typed FeaturePython)
  n = 0.271296
FEATURE [App::DocumentObjectGroupPython] N_element013  label="N_element : 0.121"  # scripted group (container) (typed FeaturePython)
  n = 0.121276
FEATURE [App::DocumentObjectGroupPython] O_element028  label="O_element : 0.578"  # scripted group (container) (typed FeaturePython)
  n = 0.578212
FEATURE [App::DocumentObjectGroupPython] G4_CELLULOSE_NITRATE  # scripted group (container) (typed FeaturePython)
  Dunit = g/cm3
  Dvalue = 1.49
  Group = -> [H_element023,C_element027,N_element013,O_element028]
  conduct = 2
  density = 1
  expand = 3
  formula = G4_CELLULOSE_NITRATE
  name = G4_CELLULOSE_NITRATE
  specific = 4
FEATURE [App::DocumentObjectGroupPython] H_element024  label="H_element : 0.108"  # scripted group (container) (typed FeaturePython)
  n = 0.107596
FEATURE [App::DocumentObjectGroupPython] N_element014  label="N_element : 0.001"  # scripted group (container) (typed FeaturePython)
  n = 0.0008
FEATURE [App::DocumentObjectGroupPython] O_element029  label="O_element : 0.875"  # scripted group (container) (typed FeaturePython)
  n = 0.874976
FEATURE [App::DocumentObjectGroupPython] S_element008  label="S_element : 0.015"  # scripted group (container) (typed FeaturePython)
  n = 0.014627
FEATURE [App::DocumentObjectGroupPython] Ce_element001  label="Ce_element : 0.002"  # scripted group (container) (typed FeaturePython)
  n = 0.002001
FEATURE [App::DocumentObjectGroupPython] G4_CERIC_SULFATE  # scripted group (container) (typed FeaturePython)
  Dunit = g/cm3
  Dvalue = 1.03
  Group = -> [H_element024,N_element014,O_element029,S_element008,Ce_element001]
  conduct = 2
  density = 1
  expand = 3
  formula = G4_CERIC_SULFATE
  name = G4_CERIC_SULFATE
  specific = 4
FEATURE [App::DocumentObjectGroupPython] Cs_element001  label="Cs_element : 1"  # scripted group (container) (typed FeaturePython)
  n = 1
  ref = Cs_element
FEATURE [App::DocumentObjectGroupPython] F_element006  label="F_element : 1"  # scripted group (container) (typed FeaturePython)
  n = 1
  ref = F_element
FEATURE [App::DocumentObjectGroupPython] G4_CESIUM_FLUORIDE  # scripted group (container) (typed FeaturePython)
  Dunit = g/cm3
  Dvalue = 4.115
  Group = -> [Cs_element001,F_element006]
  conduct = 2
  density = 1
  expand = 3
  formula = G4_CESIUM_FLUORIDE
  name = G4_CESIUM_FLUORIDE
  specific = 4
FEATURE [App::DocumentObjectGroupPython] Cs_element002  label="Cs_element : 002"  # scripted group (container) (typed FeaturePython)
  n = 1
  ref = Cs_element
FEATURE [App::DocumentObjectGroupPython] I_element001  label="I_element : 1"  # scripted group (container) (typed FeaturePython)
  n = 1
  ref = I_element
FEATURE [App::DocumentObjectGroupPython] G4_CESIUM_IODIDE  # scripted group (container) (typed FeaturePython)
  Dunit = g/cm3
  Dvalue = 4.51
  Group = -> [Cs_element002,I_element001]
  conduct = 2
  density = 1
  expand = 3
  formula = G4_CESIUM_IODIDE
  name = G4_CESIUM_IODIDE
  specific = 4
FEATURE [App::DocumentObjectGroupPython] C_element028  label="C_element : 013"  # scripted group (container) (typed FeaturePython)
  n = 6
  ref = C_element
FEATURE [App::DocumentObjectGroupPython] H_element025  label="H_element : 013"  # scripted group (container) (typed FeaturePython)
  n = 5
  ref = H_element
FEATURE [App::DocumentObjectGroupPython] Cl_element005  label="Cl_element : 1"  # scripted group (container) (typed FeaturePython)
  n = 1
  ref = Cl_element
FEATURE [App::DocumentObjectGroupPython] G4_CHLOROBENZENE  # scripted group (container) (typed FeaturePython)
  Dunit = g/cm3
  Dvalue = 1.1058
  Group = -> [C_element028,H_element025,Cl_element005]
  conduct = 2
  density = 1
  expand = 3
  formula = G4_CHLOROBENZENE
  name = G4_CHLOROBENZENE
  specific = 4
FEATURE [App::DocumentObjectGroupPython] C_element029  label="C_element : 014"  # scripted group (container) (typed FeaturePython)
  n = 1
  ref = C_element
FEATURE [App::DocumentObjectGroupPython] H_element026  label="H_element : 1"  # scripted group (container) (typed FeaturePython)
  n = 1
  ref = H_element
FEATURE [App::DocumentObjectGroupPython] Cl_element006  label="Cl_element : 3"  # scripted group (container) (typed FeaturePython)
  n = 3
  ref = Cl_element
FEATURE [App::DocumentObjectGroupPython] G4_CHLOROFORM  # scripted group (container) (typed FeaturePython)
  Dunit = g/cm3
  Dvalue = 1.4832
  Group = -> [C_element029,H_element026,Cl_element006]
  conduct = 2
  density = 1
  expand = 3
  formula = G4_CHLOROFORM
  name = G4_CHLOROFORM
  specific = 4
FEATURE [App::DocumentObjectGroupPython] H_element027  label="H_element : 0.010"  # scripted group (container) (typed FeaturePython)
  n = 0.01
FEATURE [App::DocumentObjectGroupPython] C_element030  label="C_element : 0.001"  # scripted group (container) (typed FeaturePython)
  n = 0.001
FEATURE [App::DocumentObjectGroupPython] O_element030  label="O_element : 0.529"  # scripted group (container) (typed FeaturePython)
  n = 0.529107
FEATURE [App::DocumentObjectGroupPython] Na_element005  label="Na_element : 0.016"  # scripted group (container) (typed FeaturePython)
  n = 0.016
FEATURE [App::DocumentObjectGroupPython] Mg_element003  label="Mg_element : 0.004"  # scripted group (container) (typed FeaturePython)
  n = 0.002
FEATURE [App::DocumentObjectGroupPython] Al_element002  label="Al_element : 0.034"  # scripted group (container) (typed FeaturePython)
  n = 0.033872
FEATURE [App::DocumentObjectGroupPython] Si_element002  label="Si_element : 0.337"  # scripted group (container) (typed FeaturePython)
  n = 0.337021
FEATURE [App::DocumentObjectGroupPython] K_element003  label="K_element : 0.013"  # scripted group (container) (typed FeaturePython)
  n = 0.013
FEATURE [App::DocumentObjectGroupPython] Ca_element010  label="Ca_element : 0.044"  # scripted group (container) (typed FeaturePython)
  n = 0.044
FEATURE [App::DocumentObjectGroupPython] Fe_element002  label="Fe_element : 0.014"  # scripted group (container) (typed FeaturePython)
  n = 0.014
FEATURE [App::DocumentObjectGroupPython] G4_CONCRETE  # scripted group (container) (typed FeaturePython)
  Dunit = g/cm3
  Dvalue = 2.3
  Group = -> [H_element027,C_element030,O_element030,Na_element005,Mg_element003,Al_element002,Si_element002,K_element003,Ca_element010,Fe_element002]
  conduct = 2
  density = 1
  expand = 3
  formula = G4_CONCRETE
  name = G4_CONCRETE
  specific = 4
FEATURE [App::DocumentObjectGroupPython] C_element031  label="C_element : 015"  # scripted group (container) (typed FeaturePython)
  n = 6
  ref = C_element
FEATURE [App::DocumentObjectGroupPython] H_element028  label="H_element : 12"  # scripted group (container) (typed FeaturePython)
  n = 12
  ref = H_element
FEATURE [App::DocumentObjectGroupPython] G4_CYCLOHEXANE  # scripted group (container) (typed FeaturePython)
  Dunit = g/cm3
  Dvalue = 0.779
  Group = -> [C_element031,H_element028]
  conduct = 2
  density = 1
  expand = 3
  formula = G4_CYCLOHEXANE
  name = G4_CYCLOHEXANE
  specific = 4
FEATURE [App::DocumentObjectGroupPython] C_element032  label="C_element : 016"  # scripted group (container) (typed FeaturePython)
  n = 6
  ref = C_element
FEATURE [App::DocumentObjectGroupPython] H_element029  label="H_element : 4"  # scripted group (container) (typed FeaturePython)
  n = 4
  ref = H_element
FEATURE [App::DocumentObjectGroupPython] Cl_element007  label="Cl_element : 2"  # scripted group (container) (typed FeaturePython)
  n = 2
  ref = Cl_element
FEATURE [App::DocumentObjectGroupPython] G4_1_2_DICHLOROBENZENE  label="G4_1.2-DICHLOROBENZENE"  # scripted group (container) (typed FeaturePython)
  Dunit = g/cm3
  Dvalue = 1.3048
  Group = -> [C_element032,H_element029,Cl_element007]
  conduct = 2
  density = 1
  expand = 3
  formula = G4_1.2-DICHLOROBENZENE
  name = G4_1.2-DICHLOROBENZENE
  specific = 4
FEATURE [App::DocumentObjectGroupPython] C_element033  label="C_element : 017"  # scripted group (container) (typed FeaturePython)
  n = 4
  ref = C_element
FEATURE [App::DocumentObjectGroupPython] H_element030  label="H_element : 8"  # scripted group (container) (typed FeaturePython)
  n = 8
  ref = H_element
FEATURE [App::DocumentObjectGroupPython] O_element031  label="O_element : 014"  # scripted group (container) (typed FeaturePython)
  n = 1
  ref = O_element
FEATURE [App::DocumentObjectGroupPython] Cl_element008  label="Cl_element : 005"  # scripted group (container) (typed FeaturePython)
  n = 2
  ref = Cl_element
FEATURE [App::DocumentObjectGroupPython] G4_DICHLORODIETHYL_ETHER  # scripted group (container) (typed FeaturePython)
  Dunit = g/cm3
  Dvalue = 1.2199
  Group = -> [C_element033,H_element030,O_element031,Cl_element008]
  conduct = 2
  density = 1
  expand = 3
  formula = G4_DICHLORODIETHYL_ETHER
  name = G4_DICHLORODIETHYL_ETHER
  specific = 4
FEATURE [App::DocumentObjectGroupPython] C_element034  label="C_element : 018"  # scripted group (container) (typed FeaturePython)
  n = 2
  ref = C_element
FEATURE [App::DocumentObjectGroupPython] H_element031  label="H_element : 014"  # scripted group (container) (typed FeaturePython)
  n = 4
  ref = H_element
FEATURE [App::DocumentObjectGroupPython] Cl_element009  label="Cl_element : 006"  # scripted group (container) (typed FeaturePython)
  n = 2
  ref = Cl_element
FEATURE [App::DocumentObjectGroupPython] G4_1_2_DICHLOROETHANE  label="G4_1.2-DICHLOROETHANE"  # scripted group (container) (typed FeaturePython)
  Dunit = g/cm3
  Dvalue = 1.2351
  Group = -> [C_element034,H_element031,Cl_element009]
  conduct = 2
  density = 1
  expand = 3
  formula = G4_1.2-DICHLOROETHANE
  name = G4_1.2-DICHLOROETHANE
  specific = 4
FEATURE [App::DocumentObjectGroupPython] C_element035  label="C_element : 019"  # scripted group (container) (typed FeaturePython)
  n = 4
  ref = C_element
FEATURE [App::DocumentObjectGroupPython] H_element032  label="H_element : 015"  # scripted group (container) (typed FeaturePython)
  n = 10
  ref = H_element
FEATURE [App::DocumentObjectGroupPython] O_element032  label="O_element : 015"  # scripted group (container) (typed FeaturePython)
  n = 1
  ref = O_element
FEATURE [App::DocumentObjectGroupPython] G4_DIETHYL_ETHER  # scripted group (container) (typed FeaturePython)
  Dunit = g/cm3
  Dvalue = 0.71378
  Group = -> [C_element035,H_element032,O_element032]
  conduct = 2
  density = 1
  expand = 3
  formula = G4_DIETHYL_ETHER
  name = G4_DIETHYL_ETHER
  specific = 4
FEATURE [App::DocumentObjectGroupPython] C_element036  label="C_element : 020"  # scripted group (container) (typed FeaturePython)
  n = 3
  ref = C_element
FEATURE [App::DocumentObjectGroupPython] H_element033  label="H_element : 016"  # scripted group (container) (typed FeaturePython)
  n = 7
  ref = H_element
FEATURE [App::DocumentObjectGroupPython] N_element015  label="N_element : 008"  # scripted group (container) (typed FeaturePython)
  n = 1
  ref = N_element
FEATURE [App::DocumentObjectGroupPython] O_element033  label="O_element : 016"  # scripted group (container) (typed FeaturePython)
  n = 1
  ref = O_element
FEATURE [App::DocumentObjectGroupPython] G4_N_N_DIMETHYL_FORMAMIDE  label="G4_N.N-DIMETHYL_FORMAMIDE"  # scripted group (container) (typed FeaturePython)
  Dunit = g/cm3
  Dvalue = 0.9487
  Group = -> [C_element036,H_element033,N_element015,O_element033]
  conduct = 2
  density = 1
  expand = 3
  formula = G4_N.N-DIMETHYL_FORMAMIDE
  name = G4_N.N-DIMETHYL_FORMAMIDE
  specific = 4
FEATURE [App::DocumentObjectGroupPython] C_element037  label="C_element : 021"  # scripted group (container) (typed FeaturePython)
  n = 2
  ref = C_element
FEATURE [App::DocumentObjectGroupPython] H_element034  label="H_element : 017"  # scripted group (container) (typed FeaturePython)
  n = 6
  ref = H_element
FEATURE [App::DocumentObjectGroupPython] O_element034  label="O_element : 017"  # scripted group (container) (typed FeaturePython)
  n = 1
  ref = O_element
FEATURE [App::DocumentObjectGroupPython] S_element009  label="S_element : 003"  # scripted group (container) (typed FeaturePython)
  n = 1
  ref = S_element
FEATURE [App::DocumentObjectGroupPython] G4_DIMETHYL_SULFOXIDE  # scripted group (container) (typed FeaturePython)
  Dunit = g/cm3
  Dvalue = 1.1014
  Group = -> [C_element037,H_element034,O_element034,S_element009]
  conduct = 2
  density = 1
  expand = 3
  formula = G4_DIMETHYL_SULFOXIDE
  name = G4_DIMETHYL_SULFOXIDE
  specific = 4
FEATURE [App::DocumentObjectGroupPython] C_element038  label="C_element : 022"  # scripted group (container) (typed FeaturePython)
  n = 2
  ref = C_element
FEATURE [App::DocumentObjectGroupPython] H_element035  label="H_element : 018"  # scripted group (container) (typed FeaturePython)
  n = 6
  ref = H_element
FEATURE [App::DocumentObjectGroupPython] G4_ETHANE  # scripted group (container) (typed FeaturePython)
  Dunit = g/cm3
  Dvalue = 0.00125324
  Group = -> [C_element038,H_element035]
  conduct = 2
  density = 1
  expand = 3
  formula = G4_ETHANE
  name = G4_ETHANE
  specific = 4
FEATURE [App::DocumentObjectGroupPython] C_element039  label="C_element : 023"  # scripted group (container) (typed FeaturePython)
  n = 2
  ref = C_element
FEATURE [App::DocumentObjectGroupPython] H_element036  label="H_element : 019"  # scripted group (container) (typed FeaturePython)
  n = 6
  ref = H_element
FEATURE [App::DocumentObjectGroupPython] O_element035  label="O_element : 018"  # scripted group (container) (typed FeaturePython)
  n = 1
  ref = O_element
FEATURE [App::DocumentObjectGroupPython] G4_ETHYL_ALCOHOL  # scripted group (container) (typed FeaturePython)
  Dunit = g/cm3
  Dvalue = 0.7893
  Group = -> [C_element039,H_element036,O_element035]
  conduct = 2
  density = 1
  expand = 3
  formula = G4_ETHYL_ALCOHOL
  name = G4_ETHYL_ALCOHOL
  specific = 4
FEATURE [App::DocumentObjectGroupPython] H_element037  label="H_element : 0.090"  # scripted group (container) (typed FeaturePython)
  n = 0.090027
FEATURE [App::DocumentObjectGroupPython] C_element040  label="C_element : 0.585"  # scripted group (container) (typed FeaturePython)
  n = 0.585182
FEATURE [App::DocumentObjectGroupPython] O_element036  label="O_element : 0.325"  # scripted group (container) (typed FeaturePython)
  n = 0.324791
FEATURE [App::DocumentObjectGroupPython] G4_ETHYL_CELLULOSE  # scripted group (container) (typed FeaturePython)
  Dunit = g/cm3
  Dvalue = 1.13
  Group = -> [H_element037,C_element040,O_element036]
  conduct = 2
  density = 1
  expand = 3
  formula = G4_ETHYL_CELLULOSE
  name = G4_ETHYL_CELLULOSE
  specific = 4
FEATURE [App::DocumentObjectGroupPython] C_element041  label="C_element : 024"  # scripted group (container) (typed FeaturePython)
  n = 2
  ref = C_element
FEATURE [App::DocumentObjectGroupPython] H_element038  label="H_element : 020"  # scripted group (container) (typed FeaturePython)
  n = 4
  ref = H_element
FEATURE [App::DocumentObjectGroupPython] G4_ETHYLENE  # scripted group (container) (typed FeaturePython)
  Dunit = g/cm3
  Dvalue = 0.00117497
  Group = -> [C_element041,H_element038]
  conduct = 2
  density = 1
  expand = 3
  formula = G4_ETHYLENE
  name = G4_ETHYLENE
  specific = 4
FEATURE [App::DocumentObjectGroupPython] H_element039  label="H_element : 0.096"  # scripted group (container) (typed FeaturePython)
  n = 0.096
FEATURE [App::DocumentObjectGroupPython] C_element042  label="C_element : 0.195"  # scripted group (container) (typed FeaturePython)
  n = 0.195
FEATURE [App::DocumentObjectGroupPython] N_element016  label="N_element : 0.057"  # scripted group (container) (typed FeaturePython)
  n = 0.057
FEATURE [App::DocumentObjectGroupPython] O_element037  label="O_element : 0.646"  # scripted group (container) (typed FeaturePython)
  n = 0.646
FEATURE [App::DocumentObjectGroupPython] Na_element006  label="Na_element : 0.017"  # scripted group (container) (typed FeaturePython)
  n = 0.001
FEATURE [App::DocumentObjectGroupPython] P_element005  label="P_element : 0.104"  # scripted group (container) (typed FeaturePython)
  n = 0.001
FEATURE [App::DocumentObjectGroupPython] S_element010  label="S_element : 0.016"  # scripted group (container) (typed FeaturePython)
  n = 0.003
FEATURE [App::DocumentObjectGroupPython] Cl_element010  label="Cl_element : 0.005"  # scripted group (container) (typed FeaturePython)
  n = 0.001
FEATURE [App::DocumentObjectGroupPython] G4_EYE_LENS_ICRP  # scripted group (container) (typed FeaturePython)
  Dunit = g/cm3
  Dvalue = 1.07
  Group = -> [H_element039,C_element042,N_element016,O_element037,Na_element006,P_element005,S_element010,Cl_element010]
  conduct = 2
  density = 1
  expand = 3
  formula = G4_EYE_LENS_ICRP
  name = G4_EYE_LENS_ICRP
  specific = 4
FEATURE [App::DocumentObjectGroupPython] Fe_element003  label="Fe_element : 2"  # scripted group (container) (typed FeaturePython)
  n = 2
  ref = Fe_element
FEATURE [App::DocumentObjectGroupPython] O_element038  label="O_element : 019"  # scripted group (container) (typed FeaturePython)
  n = 3
  ref = O_element
FEATURE [App::DocumentObjectGroupPython] G4_FERRIC_OXIDE  # scripted group (container) (typed FeaturePython)
  Dunit = g/cm3
  Dvalue = 5.2
  Group = -> [Fe_element003,O_element038]
  conduct = 2
  density = 1
  expand = 3
  formula = G4_FERRIC_OXIDE
  name = G4_FERRIC_OXIDE
  specific = 4
FEATURE [App::DocumentObjectGroupPython] Fe_element004  label="Fe_element : 1"  # scripted group (container) (typed FeaturePython)
  n = 1
  ref = Fe_element
FEATURE [App::DocumentObjectGroupPython] B_element003  label="B_element : 1"  # scripted group (container) (typed FeaturePython)
  n = 1
  ref = B_element
FEATURE [App::DocumentObjectGroupPython] G4_FERROBORIDE  # scripted group (container) (typed FeaturePython)
  Dunit = g/cm3
  Dvalue = 7.15
  Group = -> [Fe_element004,B_element003]
  conduct = 2
  density = 1
  expand = 3
  formula = G4_FERROBORIDE
  name = G4_FERROBORIDE
  specific = 4
FEATURE [App::DocumentObjectGroupPython] Fe_element005  label="Fe_element : 003"  # scripted group (container) (typed FeaturePython)
  n = 1
  ref = Fe_element
FEATURE [App::DocumentObjectGroupPython] O_element039  label="O_element : 020"  # scripted group (container) (typed FeaturePython)
  n = 1
  ref = O_element
FEATURE [App::DocumentObjectGroupPython] G4_FERROUS_OXIDE  # scripted group (container) (typed FeaturePython)
  Dunit = g/cm3
  Dvalue = 5.7
  Group = -> [Fe_element005,O_element039]
  conduct = 2
  density = 1
  expand = 3
  formula = G4_FERROUS_OXIDE
  name = G4_FERROUS_OXIDE
  specific = 4
FEATURE [App::DocumentObjectGroupPython] H_element040  label="H_element : 0.115"  # scripted group (container) (typed FeaturePython)
  n = 0.108259
FEATURE [App::DocumentObjectGroupPython] N_element017  label="N_element : 0.000"  # scripted group (container) (typed FeaturePython)
  n = 2.7e-05
FEATURE [App::DocumentObjectGroupPython] O_element040  label="O_element : 0.879"  # scripted group (container) (typed FeaturePython)
  n = 0.878636
FEATURE [App::DocumentObjectGroupPython] Na_element007  label="Na_element : 0.000"  # scripted group (container) (typed FeaturePython)
  n = 2.2e-05
FEATURE [App::DocumentObjectGroupPython] S_element011  label="S_element : 0.013"  # scripted group (container) (typed FeaturePython)
  n = 0.012968
FEATURE [App::DocumentObjectGroupPython] Cl_element011  label="Cl_element : 0.000"  # scripted group (container) (typed FeaturePython)
  n = 3.4e-05
FEATURE [App::DocumentObjectGroupPython] Fe_element006  label="Fe_element : 0.000"  # scripted group (container) (typed FeaturePython)
  n = 5.4e-05
FEATURE [App::DocumentObjectGroupPython] G4_FERROUS_SULFATE  # scripted group (container) (typed FeaturePython)
  Dunit = g/cm3
  Dvalue = 1.024
  Group = -> [H_element040,N_element017,O_element040,Na_element007,S_element011,Cl_element011,Fe_element006]
  conduct = 2
  density = 1
  expand = 3
  formula = G4_FERROUS_SULFATE
  name = G4_FERROUS_SULFATE
  specific = 4
FEATURE [App::DocumentObjectGroupPython] C_element043  label="C_element : 0.099"  # scripted group (container) (typed FeaturePython)
  n = 0.099335
FEATURE [App::DocumentObjectGroupPython] F_element007  label="F_element : 0.314"  # scripted group (container) (typed FeaturePython)
  n = 0.314247
FEATURE [App::DocumentObjectGroupPython] Cl_element012  label="Cl_element : 0.586"  # scripted group (container) (typed FeaturePython)
  n = 0.586418
FEATURE [App::DocumentObjectGroupPython] G4_FREON_12  label="G4_FREON-12"  # scripted group (container) (typed FeaturePython)
  Dunit = g/cm3
  Dvalue = 1.12
  Group = -> [C_element043,F_element007,Cl_element012]
  conduct = 2
  density = 1
  expand = 3
  formula = G4_FREON-12
  name = G4_FREON-12
  specific = 4
FEATURE [App::DocumentObjectGroupPython] C_element044  label="C_element : 0.057"  # scripted group (container) (typed FeaturePython)
  n = 0.057245
FEATURE [App::DocumentObjectGroupPython] F_element008  label="F_element : 0.181"  # scripted group (container) (typed FeaturePython)
  n = 0.181096
FEATURE [App::DocumentObjectGroupPython] Br_element001  label="Br_element : 0.762"  # scripted group (container) (typed FeaturePython)
  n = 0.761659
FEATURE [App::DocumentObjectGroupPython] G4_FREON_12B2  label="G4_FREON-12B2"  # scripted group (container) (typed FeaturePython)
  Dunit = g/cm3
  Dvalue = 1.8
  Group = -> [C_element044,F_element008,Br_element001]
  conduct = 2
  density = 1
  expand = 3
  formula = G4_FREON-12B2
  name = G4_FREON-12B2
  specific = 4
FEATURE [App::DocumentObjectGroupPython] C_element045  label="C_element : 0.115"  # scripted group (container) (typed FeaturePython)
  n = 0.114983
FEATURE [App::DocumentObjectGroupPython] F_element009  label="F_element : 0.546"  # scripted group (container) (typed FeaturePython)
  n = 0.545621
FEATURE [App::DocumentObjectGroupPython] Cl_element013  label="Cl_element : 0.339"  # scripted group (container) (typed FeaturePython)
  n = 0.339396
FEATURE [App::DocumentObjectGroupPython] G4_FREON_13  label="G4_FREON-13"  # scripted group (container) (typed FeaturePython)
  Dunit = g/cm3
  Dvalue = 0.95
  Group = -> [C_element045,F_element009,Cl_element013]
  conduct = 2
  density = 1
  expand = 3
  formula = G4_FREON-13
  name = G4_FREON-13
  specific = 4
FEATURE [App::DocumentObjectGroupPython] C_element046  label="C_element : 025"  # scripted group (container) (typed FeaturePython)
  n = 1
  ref = C_element
FEATURE [App::DocumentObjectGroupPython] F_element010  label="F_element : 3"  # scripted group (container) (typed FeaturePython)
  n = 3
  ref = F_element
FEATURE [App::DocumentObjectGroupPython] Br_element002  label="Br_element : 1"  # scripted group (container) (typed FeaturePython)
  n = 1
  ref = Br_element
FEATURE [App::DocumentObjectGroupPython] G4_FREON_13B1  label="G4_FREON-13B1"  # scripted group (container) (typed FeaturePython)
  Dunit = g/cm3
  Dvalue = 1.5
  Group = -> [C_element046,F_element010,Br_element002]
  conduct = 2
  density = 1
  expand = 3
  formula = G4_FREON-13B1
  name = G4_FREON-13B1
  specific = 4
FEATURE [App::DocumentObjectGroupPython] C_element047  label="C_element : 0.061"  # scripted group (container) (typed FeaturePython)
  n = 0.061309
FEATURE [App::DocumentObjectGroupPython] F_element011  label="F_element : 0.291"  # scripted group (container) (typed FeaturePython)
  n = 0.290924
FEATURE [App::DocumentObjectGroupPython] I_element002  label="I_element : 0.648"  # scripted group (container) (typed FeaturePython)
  n = 0.647767
FEATURE [App::DocumentObjectGroupPython] G4_FREON_13I1  label="G4_FREON-13I1"  # scripted group (container) (typed FeaturePython)
  Dunit = g/cm3
  Dvalue = 1.8
  Group = -> [C_element047,F_element011,I_element002]
  conduct = 2
  density = 1
  expand = 3
  formula = G4_FREON-13I1
  name = G4_FREON-13I1
  specific = 4
FEATURE [App::DocumentObjectGroupPython] Gd_element001  label="Gd_element : 2"  # scripted group (container) (typed FeaturePython)
  n = 2
  ref = Gd_element
FEATURE [App::DocumentObjectGroupPython] O_element041  label="O_element : 021"  # scripted group (container) (typed FeaturePython)
  n = 2
  ref = O_element
FEATURE [App::DocumentObjectGroupPython] S_element012  label="S_element : 004"  # scripted group (container) (typed FeaturePython)
  n = 1
  ref = S_element
FEATURE [App::DocumentObjectGroupPython] G4_GADOLINIUM_OXYSULFIDE  # scripted group (container) (typed FeaturePython)
  Dunit = g/cm3
  Dvalue = 7.44
  Group = -> [Gd_element001,O_element041,S_element012]
  conduct = 2
  density = 1
  expand = 3
  formula = G4_GADOLINIUM_OXYSULFIDE
  name = G4_GADOLINIUM_OXYSULFIDE
  specific = 4
FEATURE [App::DocumentObjectGroupPython] Ga_element001  label="Ga_element : 1"  # scripted group (container) (typed FeaturePython)
  n = 1
  ref = Ga_element
FEATURE [App::DocumentObjectGroupPython] As_element001  label="As_element : 1"  # scripted group (container) (typed FeaturePython)
  n = 1
  ref = As_element
FEATURE [App::DocumentObjectGroupPython] G4_GALLIUM_ARSENIDE  # scripted group (container) (typed FeaturePython)
  Dunit = g/cm3
  Dvalue = 5.31
  Group = -> [Ga_element001,As_element001]
  conduct = 2
  density = 1
  expand = 3
  formula = G4_GALLIUM_ARSENIDE
  name = G4_GALLIUM_ARSENIDE
  specific = 4
FEATURE [App::DocumentObjectGroupPython] H_element041  label="H_element : 0.081"  # scripted group (container) (typed FeaturePython)
  n = 0.08118
FEATURE [App::DocumentObjectGroupPython] C_element048  label="C_element : 0.416"  # scripted group (container) (typed FeaturePython)
  n = 0.41606
FEATURE [App::DocumentObjectGroupPython] N_element018  label="N_element : 0.111"  # scripted group (container) (typed FeaturePython)
  n = 0.11124
FEATURE [App::DocumentObjectGroupPython] O_element042  label="O_element : 0.381"  # scripted group (container) (typed FeaturePython)
  n = 0.38064
FEATURE [App::DocumentObjectGroupPython] S_element013  label="S_element : 0.011"  # scripted group (container) (typed FeaturePython)
  n = 0.01088
FEATURE [App::DocumentObjectGroupPython] G4_GEL_PHOTO_EMULSION  # scripted group (container) (typed FeaturePython)
  Dunit = g/cm3
  Dvalue = 1.2914
  Group = -> [H_element041,C_element048,N_element018,O_element042,S_element013]
  conduct = 2
  density = 1
  expand = 3
  formula = G4_GEL_PHOTO_EMULSION
  name = G4_GEL_PHOTO_EMULSION
  specific = 4
FEATURE [App::DocumentObjectGroupPython] B_element004  label="B_element : 0.040"  # scripted group (container) (typed FeaturePython)
  n = 0.0400639
FEATURE [App::DocumentObjectGroupPython] O_element043  label="O_element : 0.540"  # scripted group (container) (typed FeaturePython)
  n = 0.539561
FEATURE [App::DocumentObjectGroupPython] Na_element008  label="Na_element : 0.028"  # scripted group (container) (typed FeaturePython)
  n = 0.0281909
FEATURE [App::DocumentObjectGroupPython] Al_element003  label="Al_element : 0.012"  # scripted group (container) (typed FeaturePython)
  n = 0.011644
FEATURE [App::DocumentObjectGroupPython] Si_element003  label="Si_element : 0.377"  # scripted group (container) (typed FeaturePython)
  n = 0.377219
FEATURE [App::DocumentObjectGroupPython] K_element004  label="K_element : 0.014"  # scripted group (container) (typed FeaturePython)
  n = 0.00332099
FEATURE [App::DocumentObjectGroupPython] G4_Pyrex_Glass  # scripted group (container) (typed FeaturePython)
  Dunit = g/cm3
  Dvalue = 2.23
  Group = -> [B_element004,O_element043,Na_element008,Al_element003,Si_element003,K_element004]
  conduct = 2
  density = 1
  expand = 3
  formula = G4_Pyrex_Glass
  name = G4_Pyrex_Glass
  specific = 4
FEATURE [App::DocumentObjectGroupPython] O_element044  label="O_element : 0.156"  # scripted group (container) (typed FeaturePython)
  n = 0.156453
FEATURE [App::DocumentObjectGroupPython] Si_element004  label="Si_element : 0.081"  # scripted group (container) (typed FeaturePython)
  n = 0.080866
FEATURE [App::DocumentObjectGroupPython] Ti_element001  label="Ti_element : 0.008"  # scripted group (container) (typed FeaturePython)
  n = 0.008092
FEATURE [App::DocumentObjectGroupPython] As_element002  label="As_element : 0.003"  # scripted group (container) (typed FeaturePython)
  n = 0.002651
FEATURE [App::DocumentObjectGroupPython] Pb_element001  label="Pb_element : 0.752"  # scripted group (container) (typed FeaturePython)
  n = 0.751938
FEATURE [App::DocumentObjectGroupPython] G4_GLASS_LEAD  # scripted group (container) (typed FeaturePython)
  Dunit = g/cm3
  Dvalue = 6.22
  Group = -> [O_element044,Si_element004,Ti_element001,As_element002,Pb_element001]
  conduct = 2
  density = 1
  expand = 3
  formula = G4_GLASS_LEAD
  name = G4_GLASS_LEAD
  specific = 4
FEATURE [App::DocumentObjectGroupPython] O_element045  label="O_element : 0.460"  # scripted group (container) (typed FeaturePython)
  n = 0.4598
FEATURE [App::DocumentObjectGroupPython] Na_element009  label="Na_element : 0.096"  # scripted group (container) (typed FeaturePython)
  n = 0.0964411
FEATURE [App::DocumentObjectGroupPython] Si_element005  label="Si_element : 0.378"  # scripted group (container) (typed FeaturePython)
  n = 0.336553
FEATURE [App::DocumentObjectGroupPython] Ca_element011  label="Ca_element : 0.107"  # scripted group (container) (typed FeaturePython)
  n = 0.107205
FEATURE [App::DocumentObjectGroupPython] G4_GLASS_PLATE  # scripted group (container) (typed FeaturePython)
  Dunit = g/cm3
  Dvalue = 2.4
  Group = -> [O_element045,Na_element009,Si_element005,Ca_element011]
  conduct = 2
  density = 1
  expand = 3
  formula = G4_GLASS_PLATE
  name = G4_GLASS_PLATE
  specific = 4
FEATURE [App::DocumentObjectGroupPython] C_element049  label="C_element : 026"  # scripted group (container) (typed FeaturePython)
  n = 5
  ref = C_element
FEATURE [App::DocumentObjectGroupPython] H_element042  label="H_element : 021"  # scripted group (container) (typed FeaturePython)
  n = 10
  ref = H_element
FEATURE [App::DocumentObjectGroupPython] N_element019  label="N_element : 2"  # scripted group (container) (typed FeaturePython)
  n = 2
  ref = N_element
FEATURE [App::DocumentObjectGroupPython] O_element046  label="O_element : 022"  # scripted group (container) (typed FeaturePython)
  n = 3
  ref = O_element
FEATURE [App::DocumentObjectGroupPython] G4_GLUTAMINE  # scripted group (container) (typed FeaturePython)
  Dunit = g/cm3
  Dvalue = 1.46
  Group = -> [C_element049,H_element042,N_element019,O_element046]
  conduct = 2
  density = 1
  expand = 3
  formula = G4_GLUTAMINE
  name = G4_GLUTAMINE
  specific = 4
FEATURE [App::DocumentObjectGroupPython] C_element050  label="C_element : 027"  # scripted group (container) (typed FeaturePython)
  n = 3
  ref = C_element
FEATURE [App::DocumentObjectGroupPython] H_element043  label="H_element : 022"  # scripted group (container) (typed FeaturePython)
  n = 8
  ref = H_element
FEATURE [App::DocumentObjectGroupPython] O_element047  label="O_element : 023"  # scripted group (container) (typed FeaturePython)
  n = 3
  ref = O_element
FEATURE [App::DocumentObjectGroupPython] G4_GLYCEROL  # scripted group (container) (typed FeaturePython)
  Dunit = g/cm3
  Dvalue = 1.2613
  Group = -> [C_element050,H_element043,O_element047]
  conduct = 2
  density = 1
  expand = 3
  formula = G4_GLYCEROL
  name = G4_GLYCEROL
  specific = 4
FEATURE [App::DocumentObjectGroupPython] C_element051  label="C_element : 028"  # scripted group (container) (typed FeaturePython)
  n = 5
  ref = C_element
FEATURE [App::DocumentObjectGroupPython] H_element044  label="H_element : 023"  # scripted group (container) (typed FeaturePython)
  n = 5
  ref = H_element
FEATURE [App::DocumentObjectGroupPython] N_element020  label="N_element : 009"  # scripted group (container) (typed FeaturePython)
  n = 5
  ref = N_element
FEATURE [App::DocumentObjectGroupPython] O_element048  label="O_element : 024"  # scripted group (container) (typed FeaturePython)
  n = 1
  ref = O_element
FEATURE [App::DocumentObjectGroupPython] G4_GUANINE  # scripted group (container) (typed FeaturePython)
  Dunit = g/cm3
  Dvalue = 2.2
  Group = -> [C_element051,H_element044,N_element020,O_element048]
  conduct = 2
  density = 1
  expand = 3
  formula = G4_GUANINE
  name = G4_GUANINE
  specific = 4
FEATURE [App::DocumentObjectGroupPython] Ca_element012  label="Ca_element : 006"  # scripted group (container) (typed FeaturePython)
  n = 1
  ref = Ca_element
FEATURE [App::DocumentObjectGroupPython] S_element014  label="S_element : 005"  # scripted group (container) (typed FeaturePython)
  n = 1
  ref = S_element
FEATURE [App::DocumentObjectGroupPython] O_element049  label="O_element : 6"  # scripted group (container) (typed FeaturePython)
  n = 6
  ref = O_element
FEATURE [App::DocumentObjectGroupPython] H_element045  label="H_element : 024"  # scripted group (container) (typed FeaturePython)
  n = 4
  ref = H_element
FEATURE [App::DocumentObjectGroupPython] G4_GYPSUM  # scripted group (container) (typed FeaturePython)
  Dunit = g/cm3
  Dvalue = 2.32
  Group = -> [Ca_element012,S_element014,O_element049,H_element045]
  conduct = 2
  density = 1
  expand = 3
  formula = G4_GYPSUM
  name = G4_GYPSUM
  specific = 4
FEATURE [App::DocumentObjectGroupPython] C_element052  label="C_element : 7"  # scripted group (container) (typed FeaturePython)
  n = 7
  ref = C_element
FEATURE [App::DocumentObjectGroupPython] H_element046  label="H_element : 16"  # scripted group (container) (typed FeaturePython)
  n = 16
  ref = H_element
FEATURE [App::DocumentObjectGroupPython] G4_N_HEPTANE  label="G4_N-HEPTANE"  # scripted group (container) (typed FeaturePython)
  Dunit = g/cm3
  Dvalue = 0.68376
  Group = -> [C_element052,H_element046]
  conduct = 2
  density = 1
  expand = 3
  formula = G4_N-HEPTANE
  name = G4_N-HEPTANE
  specific = 4
FEATURE [App::DocumentObjectGroupPython] C_element053  label="C_element : 029"  # scripted group (container) (typed FeaturePython)
  n = 6
  ref = C_element
FEATURE [App::DocumentObjectGroupPython] H_element047  label="H_element : 14"  # scripted group (container) (typed FeaturePython)
  n = 14
  ref = H_element
FEATURE [App::DocumentObjectGroupPython] G4_N_HEXANE  label="G4_N-HEXANE"  # scripted group (container) (typed FeaturePython)
  Dunit = g/cm3
  Dvalue = 0.6603
  Group = -> [C_element053,H_element047]
  conduct = 2
  density = 1
  expand = 3
  formula = G4_N-HEXANE
  name = G4_N-HEXANE
  specific = 4
FEATURE [App::DocumentObjectGroupPython] C_element054  label="C_element : 22"  # scripted group (container) (typed FeaturePython)
  n = 22
  ref = C_element
FEATURE [App::DocumentObjectGroupPython] H_element048  label="H_element : 025"  # scripted group (container) (typed FeaturePython)
  n = 10
  ref = H_element
FEATURE [App::DocumentObjectGroupPython] N_element021  label="N_element : 010"  # scripted group (container) (typed FeaturePython)
  n = 2
  ref = N_element
FEATURE [App::DocumentObjectGroupPython] O_element050  label="O_element : 025"  # scripted group (container) (typed FeaturePython)
  n = 5
  ref = O_element
FEATURE [App::DocumentObjectGroupPython] G4_KAPTON  # scripted group (container) (typed FeaturePython)
  Dunit = g/cm3
  Dvalue = 1.42
  Group = -> [C_element054,H_element048,N_element021,O_element050]
  conduct = 2
  density = 1
  expand = 3
  formula = G4_KAPTON
  name = G4_KAPTON
  specific = 4
FEATURE [App::DocumentObjectGroupPython] La_element001  label="La_element : 1"  # scripted group (container) (typed FeaturePython)
  n = 1
  ref = La_element
FEATURE [App::DocumentObjectGroupPython] Br_element003  label="Br_element : 002"  # scripted group (container) (typed FeaturePython)
  n = 1
  ref = Br_element
FEATURE [App::DocumentObjectGroupPython] O_element051  label="O_element : 026"  # scripted group (container) (typed FeaturePython)
  n = 1
  ref = O_element
FEATURE [App::DocumentObjectGroupPython] G4_LANTHANUM_OXYBROMIDE  # scripted group (container) (typed FeaturePython)
  Dunit = g/cm3
  Dvalue = 6.28
  Group = -> [La_element001,Br_element003,O_element051]
  conduct = 2
  density = 1
  expand = 3
  formula = G4_LANTHANUM_OXYBROMIDE
  name = G4_LANTHANUM_OXYBROMIDE
  specific = 4
FEATURE [App::DocumentObjectGroupPython] La_element002  label="La_element : 2"  # scripted group (container) (typed FeaturePython)
  n = 2
  ref = La_element
FEATURE [App::DocumentObjectGroupPython] O_element052  label="O_element : 027"  # scripted group (container) (typed FeaturePython)
  n = 2
  ref = O_element
FEATURE [App::DocumentObjectGroupPython] S_element015  label="S_element : 006"  # scripted group (container) (typed FeaturePython)
  n = 1
  ref = S_element
FEATURE [App::DocumentObjectGroupPython] G4_LANTHANUM_OXYSULFIDE  # scripted group (container) (typed FeaturePython)
  Dunit = g/cm3
  Dvalue = 5.86
  Group = -> [La_element002,O_element052,S_element015]
  conduct = 2
  density = 1
  expand = 3
  formula = G4_LANTHANUM_OXYSULFIDE
  name = G4_LANTHANUM_OXYSULFIDE
  specific = 4
FEATURE [App::DocumentObjectGroupPython] O_element053  label="O_element : 0.072"  # scripted group (container) (typed FeaturePython)
  n = 0.071682
FEATURE [App::DocumentObjectGroupPython] Pb_element002  label="Pb_element : 0.928"  # scripted group (container) (typed FeaturePython)
  n = 0.928318
FEATURE [App::DocumentObjectGroupPython] G4_LEAD_OXIDE  # scripted group (container) (typed FeaturePython)
  Dunit = g/cm3
  Dvalue = 9.53
  Group = -> [O_element053,Pb_element002]
  conduct = 2
  density = 1
  expand = 3
  formula = G4_LEAD_OXIDE
  name = G4_LEAD_OXIDE
  specific = 4
FEATURE [App::DocumentObjectGroupPython] Li_element001  label="Li_element : 1"  # scripted group (container) (typed FeaturePython)
  n = 1
  ref = Li_element
FEATURE [App::DocumentObjectGroupPython] N_element022  label="N_element : 011"  # scripted group (container) (typed FeaturePython)
  n = 1
  ref = N_element
FEATURE [App::DocumentObjectGroupPython] H_element049  label="H_element : 026"  # scripted group (container) (typed FeaturePython)
  n = 2
  ref = H_element
FEATURE [App::DocumentObjectGroupPython] G4_LITHIUM_AMIDE  # scripted group (container) (typed FeaturePython)
  Dunit = g/cm3
  Dvalue = 1.178
  Group = -> [Li_element001,N_element022,H_element049]
  conduct = 2
  density = 1
  expand = 3
  formula = G4_LITHIUM_AMIDE
  name = G4_LITHIUM_AMIDE
  specific = 4
FEATURE [App::DocumentObjectGroupPython] Li_element002  label="Li_element : 2"  # scripted group (container) (typed FeaturePython)
  n = 2
  ref = Li_element
FEATURE [App::DocumentObjectGroupPython] C_element055  label="C_element : 030"  # scripted group (container) (typed FeaturePython)
  n = 1
  ref = C_element
FEATURE [App::DocumentObjectGroupPython] O_element054  label="O_element : 028"  # scripted group (container) (typed FeaturePython)
  n = 3
  ref = O_element
FEATURE [App::DocumentObjectGroupPython] G4_LITHIUM_CARBONATE  # scripted group (container) (typed FeaturePython)
  Dunit = g/cm3
  Dvalue = 2.11
  Group = -> [Li_element002,C_element055,O_element054]
  conduct = 2
  density = 1
  expand = 3
  formula = G4_LITHIUM_CARBONATE
  name = G4_LITHIUM_CARBONATE
  specific = 4
FEATURE [App::DocumentObjectGroupPython] Li_element003  label="Li_element : 003"  # scripted group (container) (typed FeaturePython)
  n = 1
  ref = Li_element
FEATURE [App::DocumentObjectGroupPython] F_element012  label="F_element : 004"  # scripted group (container) (typed FeaturePython)
  n = 1
  ref = F_element
FEATURE [App::DocumentObjectGroupPython] G4_LITHIUM_FLUORIDE  # scripted group (container) (typed FeaturePython)
  Dunit = g/cm3
  Dvalue = 2.635
  Group = -> [Li_element003,F_element012]
  conduct = 2
  density = 1
  expand = 3
  formula = G4_LITHIUM_FLUORIDE
  name = G4_LITHIUM_FLUORIDE
  specific = 4
FEATURE [App::DocumentObjectGroupPython] Li_element004  label="Li_element : 004"  # scripted group (container) (typed FeaturePython)
  n = 1
  ref = Li_element
FEATURE [App::DocumentObjectGroupPython] H_element050  label="H_element : 027"  # scripted group (container) (typed FeaturePython)
  n = 1
  ref = H_element
FEATURE [App::DocumentObjectGroupPython] G4_LITHIUM_HYDRIDE  # scripted group (container) (typed FeaturePython)
  Dunit = g/cm3
  Dvalue = 0.82
  Group = -> [Li_element004,H_element050]
  conduct = 2
  density = 1
  expand = 3
  formula = G4_LITHIUM_HYDRIDE
  name = G4_LITHIUM_HYDRIDE
  specific = 4
FEATURE [App::DocumentObjectGroupPython] Li_element005  label="Li_element : 005"  # scripted group (container) (typed FeaturePython)
  n = 1
  ref = Li_element
FEATURE [App::DocumentObjectGroupPython] I_element003  label="I_element : 002"  # scripted group (container) (typed FeaturePython)
  n = 1
  ref = I_element
FEATURE [App::DocumentObjectGroupPython] G4_LITHIUM_IODIDE  # scripted group (container) (typed FeaturePython)
  Dunit = g/cm3
  Dvalue = 3.494
  Group = -> [Li_element005,I_element003]
  conduct = 2
  density = 1
  expand = 3
  formula = G4_LITHIUM_IODIDE
  name = G4_LITHIUM_IODIDE
  specific = 4
FEATURE [App::DocumentObjectGroupPython] Li_element006  label="Li_element : 006"  # scripted group (container) (typed FeaturePython)
  n = 2
  ref = Li_element
FEATURE [App::DocumentObjectGroupPython] O_element055  label="O_element : 029"  # scripted group (container) (typed FeaturePython)
  n = 1
  ref = O_element
FEATURE [App::DocumentObjectGroupPython] G4_LITHIUM_OXIDE  # scripted group (container) (typed FeaturePython)
  Dunit = g/cm3
  Dvalue = 2.013
  Group = -> [Li_element006,O_element055]
  conduct = 2
  density = 1
  expand = 3
  formula = G4_LITHIUM_OXIDE
  name = G4_LITHIUM_OXIDE
  specific = 4
FEATURE [App::DocumentObjectGroupPython] Li_element007  label="Li_element : 007"  # scripted group (container) (typed FeaturePython)
  n = 2
  ref = Li_element
FEATURE [App::DocumentObjectGroupPython] B_element005  label="B_element : 005"  # scripted group (container) (typed FeaturePython)
  n = 4
  ref = B_element
FEATURE [App::DocumentObjectGroupPython] O_element056  label="O_element : 7"  # scripted group (container) (typed FeaturePython)
  n = 7
  ref = O_element
FEATURE [App::DocumentObjectGroupPython] G4_LITHIUM_TETRABORATE  # scripted group (container) (typed FeaturePython)
  Dunit = g/cm3
  Dvalue = 2.44
  Group = -> [Li_element007,B_element005,O_element056]
  conduct = 2
  density = 1
  expand = 3
  formula = G4_LITHIUM_TETRABORATE
  name = G4_LITHIUM_TETRABORATE
  specific = 4
FEATURE [App::DocumentObjectGroupPython] H_element051  label="H_element : 0.105"  # scripted group (container) (typed FeaturePython)
  n = 0.105
FEATURE [App::DocumentObjectGroupPython] C_element056  label="C_element : 0.083"  # scripted group (container) (typed FeaturePython)
  n = 0.083
FEATURE [App::DocumentObjectGroupPython] N_element023  label="N_element : 0.023"  # scripted group (container) (typed FeaturePython)
  n = 0.023
FEATURE [App::DocumentObjectGroupPython] O_element057  label="O_element : 0.779"  # scripted group (container) (typed FeaturePython)
  n = 0.779
FEATURE [App::DocumentObjectGroupPython] Na_element010  label="Na_element : 0.097"  # scripted group (container) (typed FeaturePython)
  n = 0.002
FEATURE [App::DocumentObjectGroupPython] P_element006  label="P_element : 0.105"  # scripted group (container) (typed FeaturePython)
  n = 0.001
FEATURE [App::DocumentObjectGroupPython] S_element016  label="S_element : 0.017"  # scripted group (container) (typed FeaturePython)
  n = 0.002
FEATURE [App::DocumentObjectGroupPython] Cl_element014  label="Cl_element : 0.587"  # scripted group (container) (typed FeaturePython)
  n = 0.003
FEATURE [App::DocumentObjectGroupPython] K_element005  label="K_element : 0.015"  # scripted group (container) (typed FeaturePython)
  n = 0.002
FEATURE [App::DocumentObjectGroupPython] G4_LUNG_ICRP  # scripted group (container) (typed FeaturePython)
  Dunit = g/cm3
  Dvalue = 1.04
  Group = -> [H_element051,C_element056,N_element023,O_element057,Na_element010,P_element006,S_element016,Cl_element014,K_element005]
  conduct = 2
  density = 1
  expand = 3
  formula = G4_LUNG_ICRP
  name = G4_LUNG_ICRP
  specific = 4
FEATURE [App::DocumentObjectGroupPython] H_element052  label="H_element : 0.116"  # scripted group (container) (typed FeaturePython)
  n = 0.114318
FEATURE [App::DocumentObjectGroupPython] C_element057  label="C_element : 0.656"  # scripted group (container) (typed FeaturePython)
  n = 0.655824
FEATURE [App::DocumentObjectGroupPython] O_element058  label="O_element : 0.092"  # scripted group (container) (typed FeaturePython)
  n = 0.0921831
FEATURE [App::DocumentObjectGroupPython] Mg_element004  label="Mg_element : 0.135"  # scripted group (container) (typed FeaturePython)
  n = 0.134792
FEATURE [App::DocumentObjectGroupPython] Ca_element013  label="Ca_element : 0.003"  # scripted group (container) (typed FeaturePython)
  n = 0.002883
FEATURE [App::DocumentObjectGroupPython] G4_M3_WAX  # scripted group (container) (typed FeaturePython)
  Dunit = g/cm3
  Dvalue = 1.05
  Group = -> [H_element052,C_element057,O_element058,Mg_element004,Ca_element013]
  conduct = 2
  density = 1
  expand = 3
  formula = G4_M3_WAX
  name = G4_M3_WAX
  specific = 4
FEATURE [App::DocumentObjectGroupPython] Mg_element005  label="Mg_element : 1"  # scripted group (container) (typed FeaturePython)
  n = 1
  ref = Mg_element
FEATURE [App::DocumentObjectGroupPython] C_element058  label="C_element : 031"  # scripted group (container) (typed FeaturePython)
  n = 1
  ref = C_element
FEATURE [App::DocumentObjectGroupPython] O_element059  label="O_element : 030"  # scripted group (container) (typed FeaturePython)
  n = 3
  ref = O_element
FEATURE [App::DocumentObjectGroupPython] G4_MAGNESIUM_CARBONATE  # scripted group (container) (typed FeaturePython)
  Dunit = g/cm3
  Dvalue = 2.958
  Group = -> [Mg_element005,C_element058,O_element059]
  conduct = 2
  density = 1
  expand = 3
  formula = G4_MAGNESIUM_CARBONATE
  name = G4_MAGNESIUM_CARBONATE
  specific = 4
FEATURE [App::DocumentObjectGroupPython] Mg_element006  label="Mg_element : 002"  # scripted group (container) (typed FeaturePython)
  n = 1
  ref = Mg_element
FEATURE [App::DocumentObjectGroupPython] F_element013  label="F_element : 005"  # scripted group (container) (typed FeaturePython)
  n = 2
  ref = F_element
FEATURE [App::DocumentObjectGroupPython] G4_MAGNESIUM_FLUORIDE  # scripted group (container) (typed FeaturePython)
  Dunit = g/cm3
  Dvalue = 3
  Group = -> [Mg_element006,F_element013]
  conduct = 2
  density = 1
  expand = 3
  formula = G4_MAGNESIUM_FLUORIDE
  name = G4_MAGNESIUM_FLUORIDE
  specific = 4
FEATURE [App::DocumentObjectGroupPython] Mg_element007  label="Mg_element : 003"  # scripted group (container) (typed FeaturePython)
  n = 1
  ref = Mg_element
FEATURE [App::DocumentObjectGroupPython] O_element060  label="O_element : 031"  # scripted group (container) (typed FeaturePython)
  n = 1
  ref = O_element
FEATURE [App::DocumentObjectGroupPython] G4_MAGNESIUM_OXIDE  # scripted group (container) (typed FeaturePython)
  Dunit = g/cm3
  Dvalue = 3.58
  Group = -> [Mg_element007,O_element060]
  conduct = 2
  density = 1
  expand = 3
  formula = G4_MAGNESIUM_OXIDE
  name = G4_MAGNESIUM_OXIDE
  specific = 4
FEATURE [App::DocumentObjectGroupPython] Mg_element008  label="Mg_element : 004"  # scripted group (container) (typed FeaturePython)
  n = 1
  ref = Mg_element
FEATURE [App::DocumentObjectGroupPython] B_element006  label="B_element : 006"  # scripted group (container) (typed FeaturePython)
  n = 4
  ref = B_element
FEATURE [App::DocumentObjectGroupPython] O_element061  label="O_element : 032"  # scripted group (container) (typed FeaturePython)
  n = 7
  ref = O_element
FEATURE [App::DocumentObjectGroupPython] G4_MAGNESIUM_TETRABORATE  # scripted group (container) (typed FeaturePython)
  Dunit = g/cm3
  Dvalue = 2.53
  Group = -> [Mg_element008,B_element006,O_element061]
  conduct = 2
  density = 1
  expand = 3
  formula = G4_MAGNESIUM_TETRABORATE
  name = G4_MAGNESIUM_TETRABORATE
  specific = 4
FEATURE [App::DocumentObjectGroupPython] Hg_element001  label="Hg_element : 1"  # scripted group (container) (typed FeaturePython)
  n = 1
  ref = Hg_element
FEATURE [App::DocumentObjectGroupPython] I_element004  label="I_element : 2"  # scripted group (container) (typed FeaturePython)
  n = 2
  ref = I_element
FEATURE [App::DocumentObjectGroupPython] G4_MERCURIC_IODIDE  # scripted group (container) (typed FeaturePython)
  Dunit = g/cm3
  Dvalue = 6.36
  Group = -> [Hg_element001,I_element004]
  conduct = 2
  density = 1
  expand = 3
  formula = G4_MERCURIC_IODIDE
  name = G4_MERCURIC_IODIDE
  specific = 4
FEATURE [App::DocumentObjectGroupPython] C_element059  label="C_element : 032"  # scripted group (container) (typed FeaturePython)
  n = 1
  ref = C_element
FEATURE [App::DocumentObjectGroupPython] H_element053  label="H_element : 028"  # scripted group (container) (typed FeaturePython)
  n = 4
  ref = H_element
FEATURE [App::DocumentObjectGroupPython] G4_METHANE  # scripted group (container) (typed FeaturePython)
  Dunit = g/cm3
  Dvalue = 0.000667151
  Group = -> [C_element059,H_element053]
  conduct = 2
  density = 1
  expand = 3
  formula = G4_METHANE
  name = G4_METHANE
  specific = 4
FEATURE [App::DocumentObjectGroupPython] C_element060  label="C_element : 033"  # scripted group (container) (typed FeaturePython)
  n = 1
  ref = C_element
FEATURE [App::DocumentObjectGroupPython] H_element054  label="H_element : 029"  # scripted group (container) (typed FeaturePython)
  n = 4
  ref = H_element
FEATURE [App::DocumentObjectGroupPython] O_element062  label="O_element : 033"  # scripted group (container) (typed FeaturePython)
  n = 1
  ref = O_element
FEATURE [App::DocumentObjectGroupPython] G4_METHANOL  # scripted group (container) (typed FeaturePython)
  Dunit = g/cm3
  Dvalue = 0.7914
  Group = -> [C_element060,H_element054,O_element062]
  conduct = 2
  density = 1
  expand = 3
  formula = G4_METHANOL
  name = G4_METHANOL
  specific = 4
FEATURE [App::DocumentObjectGroupPython] H_element055  label="H_element : 0.134"  # scripted group (container) (typed FeaturePython)
  n = 0.13404
FEATURE [App::DocumentObjectGroupPython] C_element061  label="C_element : 0.778"  # scripted group (container) (typed FeaturePython)
  n = 0.77796
FEATURE [App::DocumentObjectGroupPython] O_element063  label="O_element : 0.035"  # scripted group (container) (typed FeaturePython)
  n = 0.03502
FEATURE [App::DocumentObjectGroupPython] Mg_element009  label="Mg_element : 0.039"  # scripted group (container) (typed FeaturePython)
  n = 0.038594
FEATURE [App::DocumentObjectGroupPython] Ti_element002  label="Ti_element : 0.014"  # scripted group (container) (typed FeaturePython)
  n = 0.014386
FEATURE [App::DocumentObjectGroupPython] G4_MIX_D_WAX  # scripted group (container) (typed FeaturePython)
  Dunit = g/cm3
  Dvalue = 0.99
  Group = -> [H_element055,C_element061,O_element063,Mg_element009,Ti_element002]
  conduct = 2
  density = 1
  expand = 3
  formula = G4_MIX_D_WAX
  name = G4_MIX_D_WAX
  specific = 4
FEATURE [App::DocumentObjectGroupPython] H_element056  label="H_element : 0.135"  # scripted group (container) (typed FeaturePython)
  n = 0.081192
FEATURE [App::DocumentObjectGroupPython] C_element062  label="C_element : 0.583"  # scripted group (container) (typed FeaturePython)
  n = 0.583442
FEATURE [App::DocumentObjectGroupPython] N_element024  label="N_element : 0.018"  # scripted group (container) (typed FeaturePython)
  n = 0.017798
FEATURE [App::DocumentObjectGroupPython] O_element064  label="O_element : 0.186"  # scripted group (container) (typed FeaturePython)
  n = 0.186381
FEATURE [App::DocumentObjectGroupPython] Mg_element010  label="Mg_element : 0.130"  # scripted group (container) (typed FeaturePython)
  n = 0.130287
FEATURE [App::DocumentObjectGroupPython] Cl_element015  label="Cl_element : 0.588"  # scripted group (container) (typed FeaturePython)
  n = 0.0009
FEATURE [App::DocumentObjectGroupPython] G4_MS20_TISSUE  # scripted group (container) (typed FeaturePython)
  Dunit = g/cm3
  Dvalue = 1
  Group = -> [H_element056,C_element062,N_element024,O_element064,Mg_element010,Cl_element015]
  conduct = 2
  density = 1
  expand = 3
  formula = G4_MS20_TISSUE
  name = G4_MS20_TISSUE
  specific = 4
FEATURE [App::DocumentObjectGroupPython] H_element057  label="H_element : 0.136"  # scripted group (container) (typed FeaturePython)
  n = 0.102
FEATURE [App::DocumentObjectGroupPython] C_element063  label="C_element : 0.143"  # scripted group (container) (typed FeaturePython)
  n = 0.143
FEATURE [App::DocumentObjectGroupPython] N_element025  label="N_element : 0.034"  # scripted group (container) (typed FeaturePython)
  n = 0.034
FEATURE [App::DocumentObjectGroupPython] O_element065  label="O_element : 0.710"  # scripted group (container) (typed FeaturePython)
  n = 0.71
FEATURE [App::DocumentObjectGroupPython] Na_element011  label="Na_element : 0.098"  # scripted group (container) (typed FeaturePython)
  n = 0.001
FEATURE [App::DocumentObjectGroupPython] P_element007  label="P_element : 0.002"  # scripted group (container) (typed FeaturePython)
  n = 0.002
FEATURE [App::DocumentObjectGroupPython] S_element017  label="S_element : 0.018"  # scripted group (container) (typed FeaturePython)
  n = 0.003
FEATURE [App::DocumentObjectGroupPython] Cl_element016  label="Cl_element : 0.589"  # scripted group (container) (typed FeaturePython)
  n = 0.001
FEATURE [App::DocumentObjectGroupPython] K_element006  label="K_element : 0.004"  # scripted group (container) (typed FeaturePython)
  n = 0.004
FEATURE [App::DocumentObjectGroupPython] G4_MUSCLE_SKELETAL_ICRP  # scripted group (container) (typed FeaturePython)
  Dunit = g/cm3
  Dvalue = 1.05
  Group = -> [H_element057,C_element063,N_element025,O_element065,Na_element011,P_element007,S_element017,Cl_element016,K_element006]
  conduct = 2
  density = 1
  expand = 3
  formula = G4_MUSCLE_SKELETAL_ICRP
  name = G4_MUSCLE_SKELETAL_ICRP
  specific = 4
FEATURE [App::DocumentObjectGroupPython] H_element058  label="H_element : 0.137"  # scripted group (container) (typed FeaturePython)
  n = 0.102102
FEATURE [App::DocumentObjectGroupPython] C_element064  label="C_element : 0.123"  # scripted group (container) (typed FeaturePython)
  n = 0.123123
FEATURE [App::DocumentObjectGroupPython] N_element026  label="N_element : 0.756"  # scripted group (container) (typed FeaturePython)
  n = 0.035035
FEATURE [App::DocumentObjectGroupPython] O_element066  label="O_element : 0.730"  # scripted group (container) (typed FeaturePython)
  n = 0.72973
FEATURE [App::DocumentObjectGroupPython] Na_element012  label="Na_element : 0.099"  # scripted group (container) (typed FeaturePython)
  n = 0.001001
FEATURE [App::DocumentObjectGroupPython] P_element008  label="P_element : 0.106"  # scripted group (container) (typed FeaturePython)
  n = 0.002002
FEATURE [App::DocumentObjectGroupPython] S_element018  label="S_element : 0.019"  # scripted group (container) (typed FeaturePython)
  n = 0.004004
FEATURE [App::DocumentObjectGroupPython] K_element007  label="K_element : 0.016"  # scripted group (container) (typed FeaturePython)
  n = 0.003003
FEATURE [App::DocumentObjectGroupPython] G4_MUSCLE_STRIATED_ICRU  # scripted group (container) (typed FeaturePython)
  Dunit = g/cm3
  Dvalue = 1.04
  Group = -> [H_element058,C_element064,N_element026,O_element066,Na_element012,P_element008,S_element018,K_element007]
  conduct = 2
  density = 1
  expand = 3
  formula = G4_MUSCLE_STRIATED_ICRU
  name = G4_MUSCLE_STRIATED_ICRU
  specific = 4
FEATURE [App::DocumentObjectGroupPython] H_element059  label="H_element : 0.098"  # scripted group (container) (typed FeaturePython)
  n = 0.0982341
FEATURE [App::DocumentObjectGroupPython] C_element065  label="C_element : 0.156"  # scripted group (container) (typed FeaturePython)
  n = 0.156214
FEATURE [App::DocumentObjectGroupPython] N_element027  label="N_element : 0.757"  # scripted group (container) (typed FeaturePython)
  n = 0.035451
FEATURE [App::DocumentObjectGroupPython] O_element067  label="O_element : 0.880"  # scripted group (container) (typed FeaturePython)
  n = 0.710101
FEATURE [App::DocumentObjectGroupPython] G4_MUSCLE_WITH_SUCROSE  # scripted group (container) (typed FeaturePython)
  Dunit = g/cm3
  Dvalue = 1.11
  Group = -> [H_element059,C_element065,N_element027,O_element067]
  conduct = 2
  density = 1
  expand = 3
  formula = G4_MUSCLE_WITH_SUCROSE
  name = G4_MUSCLE_WITH_SUCROSE
  specific = 4
FEATURE [App::DocumentObjectGroupPython] H_element060  label="H_element : 0.138"  # scripted group (container) (typed FeaturePython)
  n = 0.101969
FEATURE [App::DocumentObjectGroupPython] C_element066  label="C_element : 0.120"  # scripted group (container) (typed FeaturePython)
  n = 0.120058
FEATURE [App::DocumentObjectGroupPython] N_element028  label="N_element : 0.758"  # scripted group (container) (typed FeaturePython)
  n = 0.035451
FEATURE [App::DocumentObjectGroupPython] O_element068  label="O_element : 0.743"  # scripted group (container) (typed FeaturePython)
  n = 0.742522
FEATURE [App::DocumentObjectGroupPython] G4_MUSCLE_WITHOUT_SUCROSE  # scripted group (container) (typed FeaturePython)
  Dunit = g/cm3
  Dvalue = 1.07
  Group = -> [H_element060,C_element066,N_element028,O_element068]
  conduct = 2
  density = 1
  expand = 3
  formula = G4_MUSCLE_WITHOUT_SUCROSE
  name = G4_MUSCLE_WITHOUT_SUCROSE
  specific = 4
FEATURE [App::DocumentObjectGroupPython] C_element067  label="C_element : 10"  # scripted group (container) (typed FeaturePython)
  n = 10
  ref = C_element
FEATURE [App::DocumentObjectGroupPython] H_element061  label="H_element : 030"  # scripted group (container) (typed FeaturePython)
  n = 8
  ref = H_element
FEATURE [App::DocumentObjectGroupPython] G4_NAPHTHALENE  # scripted group (container) (typed FeaturePython)
  Dunit = g/cm3
  Dvalue = 1.145
  Group = -> [C_element067,H_element061]
  conduct = 2
  density = 1
  expand = 3
  formula = G4_NAPHTHALENE
  name = G4_NAPHTHALENE
  specific = 4
FEATURE [App::DocumentObjectGroupPython] C_element068  label="C_element : 034"  # scripted group (container) (typed FeaturePython)
  n = 6
  ref = C_element
FEATURE [App::DocumentObjectGroupPython] H_element062  label="H_element : 031"  # scripted group (container) (typed FeaturePython)
  n = 5
  ref = H_element
FEATURE [App::DocumentObjectGroupPython] N_element029  label="N_element : 012"  # scripted group (container) (typed FeaturePython)
  n = 1
  ref = N_element
FEATURE [App::DocumentObjectGroupPython] O_element069  label="O_element : 034"  # scripted group (container) (typed FeaturePython)
  n = 2
  ref = O_element
FEATURE [App::DocumentObjectGroupPython] G4_NITROBENZENE  # scripted group (container) (typed FeaturePython)
  Dunit = g/cm3
  Dvalue = 1.19867
  Group = -> [C_element068,H_element062,N_element029,O_element069]
  conduct = 2
  density = 1
  expand = 3
  formula = G4_NITROBENZENE
  name = G4_NITROBENZENE
  specific = 4
FEATURE [App::DocumentObjectGroupPython] N_element030  label="N_element : 013"  # scripted group (container) (typed FeaturePython)
  n = 2
  ref = N_element
FEATURE [App::DocumentObjectGroupPython] O_element070  label="O_element : 035"  # scripted group (container) (typed FeaturePython)
  n = 1
  ref = O_element
FEATURE [App::DocumentObjectGroupPython] G4_NITROUS_OXIDE  # scripted group (container) (typed FeaturePython)
  Dunit = g/cm3
  Dvalue = 0.00183094
  Group = -> [N_element030,O_element070]
  conduct = 2
  density = 1
  expand = 3
  formula = G4_NITROUS_OXIDE
  name = G4_NITROUS_OXIDE
  specific = 4
FEATURE [App::DocumentObjectGroupPython] H_element063  label="H_element : 0.104"  # scripted group (container) (typed FeaturePython)
  n = 0.103509
FEATURE [App::DocumentObjectGroupPython] C_element069  label="C_element : 0.648"  # scripted group (container) (typed FeaturePython)
  n = 0.648416
FEATURE [App::DocumentObjectGroupPython] N_element031  label="N_element : 0.100"  # scripted group (container) (typed FeaturePython)
  n = 0.0995361
FEATURE [App::DocumentObjectGroupPython] O_element071  label="O_element : 0.149"  # scripted group (container) (typed FeaturePython)
  n = 0.148539
FEATURE [App::DocumentObjectGroupPython] G4_NYLON_8062  label="G4_NYLON-8062"  # scripted group (container) (typed FeaturePython)
  Dunit = g/cm3
  Dvalue = 1.08
  Group = -> [H_element063,C_element069,N_element031,O_element071]
  conduct = 2
  density = 1
  expand = 3
  formula = G4_NYLON-8062
  name = G4_NYLON-8062
  specific = 4
FEATURE [App::DocumentObjectGroupPython] C_element070  label="C_element : 035"  # scripted group (container) (typed FeaturePython)
  n = 6
  ref = C_element
FEATURE [App::DocumentObjectGroupPython] H_element064  label="H_element : 11"  # scripted group (container) (typed FeaturePython)
  n = 11
  ref = H_element
FEATURE [App::DocumentObjectGroupPython] N_element032  label="N_element : 014"  # scripted group (container) (typed FeaturePython)
  n = 1
  ref = N_element
FEATURE [App::DocumentObjectGroupPython] O_element072  label="O_element : 036"  # scripted group (container) (typed FeaturePython)
  n = 1
  ref = O_element
FEATURE [App::DocumentObjectGroupPython] G4_NYLON_6_6  label="G4_NYLON-6-6"  # scripted group (container) (typed FeaturePython)
  Dunit = g/cm3
  Dvalue = 1.14
  Group = -> [C_element070,H_element064,N_element032,O_element072]
  conduct = 2
  density = 1
  expand = 3
  formula = G4_NYLON-6-6
  name = G4_NYLON-6-6
  specific = 4
FEATURE [App::DocumentObjectGroupPython] H_element065  label="H_element : 0.139"  # scripted group (container) (typed FeaturePython)
  n = 0.107062
FEATURE [App::DocumentObjectGroupPython] C_element071  label="C_element : 0.680"  # scripted group (container) (typed FeaturePython)
  n = 0.680449
FEATURE [App::DocumentObjectGroupPython] N_element033  label="N_element : 0.099"  # scripted group (container) (typed FeaturePython)
  n = 0.099189
FEATURE [App::DocumentObjectGroupPython] O_element073  label="O_element : 0.113"  # scripted group (container) (typed FeaturePython)
  n = 0.1133
FEATURE [App::DocumentObjectGroupPython] G4_NYLON_6_10  label="G4_NYLON-6-10"  # scripted group (container) (typed FeaturePython)
  Dunit = g/cm3
  Dvalue = 1.14
  Group = -> [H_element065,C_element071,N_element033,O_element073]
  conduct = 2
  density = 1
  expand = 3
  formula = G4_NYLON-6-10
  name = G4_NYLON-6-10
  specific = 4
FEATURE [App::DocumentObjectGroupPython] H_element066  label="H_element : 0.140"  # scripted group (container) (typed FeaturePython)
  n = 0.115476
FEATURE [App::DocumentObjectGroupPython] C_element072  label="C_element : 0.721"  # scripted group (container) (typed FeaturePython)
  n = 0.720818
FEATURE [App::DocumentObjectGroupPython] N_element034  label="N_element : 0.076"  # scripted group (container) (typed FeaturePython)
  n = 0.0764169
FEATURE [App::DocumentObjectGroupPython] O_element074  label="O_element : 0.087"  # scripted group (container) (typed FeaturePython)
  n = 0.0872889
FEATURE [App::DocumentObjectGroupPython] G4_NYLON_11_RILSAN  label="G4_NYLON-11_RILSAN"  # scripted group (container) (typed FeaturePython)
  Dunit = g/cm3
  Dvalue = 1.425
  Group = -> [H_element066,C_element072,N_element034,O_element074]
  conduct = 2
  density = 1
  expand = 3
  formula = G4_NYLON-11_RILSAN
  name = G4_NYLON-11_RILSAN
  specific = 4
FEATURE [App::DocumentObjectGroupPython] C_element073  label="C_element : 8"  # scripted group (container) (typed FeaturePython)
  n = 8
  ref = C_element
FEATURE [App::DocumentObjectGroupPython] H_element067  label="H_element : 18"  # scripted group (container) (typed FeaturePython)
  n = 18
  ref = H_element
FEATURE [App::DocumentObjectGroupPython] G4_OCTANE  # scripted group (container) (typed FeaturePython)
  Dunit = g/cm3
  Dvalue = 0.7026
  Group = -> [C_element073,H_element067]
  conduct = 2
  density = 1
  expand = 3
  formula = G4_OCTANE
  name = G4_OCTANE
  specific = 4
FEATURE [App::DocumentObjectGroupPython] C_element074  label="C_element : 25"  # scripted group (container) (typed FeaturePython)
  n = 25
  ref = C_element
FEATURE [App::DocumentObjectGroupPython] H_element068  label="H_element : 52"  # scripted group (container) (typed FeaturePython)
  n = 52
  ref = H_element
FEATURE [App::DocumentObjectGroupPython] G4_PARAFFIN  # scripted group (container) (typed FeaturePython)
  Dunit = g/cm3
  Dvalue = 0.93
  Group = -> [C_element074,H_element068]
  conduct = 2
  density = 1
  expand = 3
  formula = G4_PARAFFIN
  name = G4_PARAFFIN
  specific = 4
FEATURE [App::DocumentObjectGroupPython] C_element075  label="C_element : 036"  # scripted group (container) (typed FeaturePython)
  n = 5
  ref = C_element
FEATURE [App::DocumentObjectGroupPython] H_element069  label="H_element : 032"  # scripted group (container) (typed FeaturePython)
  n = 12
  ref = H_element
FEATURE [App::DocumentObjectGroupPython] G4_N_PENTANE  label="G4_N-PENTANE"  # scripted group (container) (typed FeaturePython)
  Dunit = g/cm3
  Dvalue = 0.6262
  Group = -> [C_element075,H_element069]
  conduct = 2
  density = 1
  expand = 3
  formula = G4_N-PENTANE
  name = G4_N-PENTANE
  specific = 4
FEATURE [App::DocumentObjectGroupPython] H_element070  label="H_element : 0.014"  # scripted group (container) (typed FeaturePython)
  n = 0.0141
FEATURE [App::DocumentObjectGroupPython] C_element076  label="C_element : 0.072"  # scripted group (container) (typed FeaturePython)
  n = 0.072261
FEATURE [App::DocumentObjectGroupPython] N_element035  label="N_element : 0.019"  # scripted group (container) (typed FeaturePython)
  n = 0.01932
FEATURE [App::DocumentObjectGroupPython] O_element075  label="O_element : 0.066"  # scripted group (container) (typed FeaturePython)
  n = 0.066101
FEATURE [App::DocumentObjectGroupPython] S_element019  label="S_element : 0.020"  # scripted group (container) (typed FeaturePython)
  n = 0.00189
FEATURE [App::DocumentObjectGroupPython] Br_element004  label="Br_element : 0.349"  # scripted group (container) (typed FeaturePython)
  n = 0.349103
FEATURE [App::DocumentObjectGroupPython] Ag_element001  label="Ag_element : 0.474"  # scripted group (container) (typed FeaturePython)
  n = 0.474105
FEATURE [App::DocumentObjectGroupPython] I_element005  label="I_element : 0.003"  # scripted group (container) (typed FeaturePython)
  n = 0.00312
FEATURE [App::DocumentObjectGroupPython] G4_PHOTO_EMULSION  # scripted group (container) (typed FeaturePython)
  Dunit = g/cm3
  Dvalue = 3.815
  Group = -> [H_element070,C_element076,N_element035,O_element075,S_element019,Br_element004,Ag_element001,I_element005]
  conduct = 2
  density = 1
  expand = 3
  formula = G4_PHOTO_EMULSION
  name = G4_PHOTO_EMULSION
  specific = 4
FEATURE [App::DocumentObjectGroupPython] C_element077  label="C_element : 9"  # scripted group (container) (typed FeaturePython)
  n = 9
  ref = C_element
FEATURE [App::DocumentObjectGroupPython] H_element071  label="H_element : 033"  # scripted group (container) (typed FeaturePython)
  n = 10
  ref = H_element
FEATURE [App::DocumentObjectGroupPython] G4_PLASTIC_SC_VINYLTOLUENE  # scripted group (container) (typed FeaturePython)
  Dunit = g/cm3
  Dvalue = 1.032
  Group = -> [C_element077,H_element071]
  conduct = 2
  density = 1
  expand = 3
  formula = G4_PLASTIC_SC_VINYLTOLUENE
  name = G4_PLASTIC_SC_VINYLTOLUENE
  specific = 4
FEATURE [App::DocumentObjectGroupPython] Pu_element001  label="Pu_element : 1"  # scripted group (container) (typed FeaturePython)
  n = 1
  ref = Pu_element
FEATURE [App::DocumentObjectGroupPython] O_element076  label="O_element : 037"  # scripted group (container) (typed FeaturePython)
  n = 2
  ref = O_element
FEATURE [App::DocumentObjectGroupPython] G4_PLUTONIUM_DIOXIDE  # scripted group (container) (typed FeaturePython)
  Dunit = g/cm3
  Dvalue = 11.46
  Group = -> [Pu_element001,O_element076]
  conduct = 2
  density = 1
  expand = 3
  formula = G4_PLUTONIUM_DIOXIDE
  name = G4_PLUTONIUM_DIOXIDE
  specific = 4
FEATURE [App::DocumentObjectGroupPython] C_element078  label="C_element : 037"  # scripted group (container) (typed FeaturePython)
  n = 3
  ref = C_element
FEATURE [App::DocumentObjectGroupPython] H_element072  label="H_element : 034"  # scripted group (container) (typed FeaturePython)
  n = 3
  ref = H_element
FEATURE [App::DocumentObjectGroupPython] N_element036  label="N_element : 015"  # scripted group (container) (typed FeaturePython)
  n = 1
  ref = N_element
FEATURE [App::DocumentObjectGroupPython] G4_POLYACRYLONITRILE  # scripted group (container) (typed FeaturePython)
  Dunit = g/cm3
  Dvalue = 1.17
  Group = -> [C_element078,H_element072,N_element036]
  conduct = 2
  density = 1
  expand = 3
  formula = G4_POLYACRYLONITRILE
  name = G4_POLYACRYLONITRILE
  specific = 4
FEATURE [App::DocumentObjectGroupPython] C_element079  label="C_element : 16"  # scripted group (container) (typed FeaturePython)
  n = 16
  ref = C_element
FEATURE [App::DocumentObjectGroupPython] H_element073  label="H_element : 035"  # scripted group (container) (typed FeaturePython)
  n = 14
  ref = H_element
FEATURE [App::DocumentObjectGroupPython] O_element077  label="O_element : 038"  # scripted group (container) (typed FeaturePython)
  n = 3
  ref = O_element
FEATURE [App::DocumentObjectGroupPython] G4_POLYCARBONATE  # scripted group (container) (typed FeaturePython)
  Dunit = g/cm3
  Dvalue = 1.2
  Group = -> [C_element079,H_element073,O_element077]
  conduct = 2
  density = 1
  expand = 3
  formula = G4_POLYCARBONATE
  name = G4_POLYCARBONATE
  specific = 4
FEATURE [App::DocumentObjectGroupPython] C_element080  label="C_element : 038"  # scripted group (container) (typed FeaturePython)
  n = 8
  ref = C_element
FEATURE [App::DocumentObjectGroupPython] H_element074  label="H_element : 036"  # scripted group (container) (typed FeaturePython)
  n = 7
  ref = H_element
FEATURE [App::DocumentObjectGroupPython] Cl_element017  label="Cl_element : 007"  # scripted group (container) (typed FeaturePython)
  n = 1
  ref = Cl_element
FEATURE [App::DocumentObjectGroupPython] G4_POLYCHLOROSTYRENE  # scripted group (container) (typed FeaturePython)
  Dunit = g/cm3
  Dvalue = 1.3
  Group = -> [C_element080,H_element074,Cl_element017]
  conduct = 2
  density = 1
  expand = 3
  formula = G4_POLYCHLOROSTYRENE
  name = G4_POLYCHLOROSTYRENE
  specific = 4
FEATURE [App::DocumentObjectGroupPython] C_element081  label="C_element : 039"  # scripted group (container) (typed FeaturePython)
  n = 1
  ref = C_element
FEATURE [App::DocumentObjectGroupPython] H_element075  label="H_element : 037"  # scripted group (container) (typed FeaturePython)
  n = 2
  ref = H_element
FEATURE [App::DocumentObjectGroupPython] G4_POLYETHYLENE  # scripted group (container) (typed FeaturePython)
  Dunit = g/cm3
  Dvalue = 0.94
  Group = -> [C_element081,H_element075]
  conduct = 2
  density = 1
  expand = 3
  formula = G4_POLYETHYLENE
  name = G4_POLYETHYLENE
  specific = 4
FEATURE [App::DocumentObjectGroupPython] C_element082  label="C_element : 040"  # scripted group (container) (typed FeaturePython)
  n = 10
  ref = C_element
FEATURE [App::DocumentObjectGroupPython] H_element076  label="H_element : 038"  # scripted group (container) (typed FeaturePython)
  n = 8
  ref = H_element
FEATURE [App::DocumentObjectGroupPython] O_element078  label="O_element : 039"  # scripted group (container) (typed FeaturePython)
  n = 4
  ref = O_element
FEATURE [App::DocumentObjectGroupPython] G4_MYLAR  # scripted group (container) (typed FeaturePython)
  Dunit = g/cm3
  Dvalue = 1.4
  Group = -> [C_element082,H_element076,O_element078]
  conduct = 2
  density = 1
  expand = 3
  formula = G4_MYLAR
  name = G4_MYLAR
  specific = 4
FEATURE [App::DocumentObjectGroupPython] C_element083  label="C_element : 041"  # scripted group (container) (typed FeaturePython)
  n = 5
  ref = C_element
FEATURE [App::DocumentObjectGroupPython] H_element077  label="H_element : 039"  # scripted group (container) (typed FeaturePython)
  n = 8
  ref = H_element
FEATURE [App::DocumentObjectGroupPython] O_element079  label="O_element : 040"  # scripted group (container) (typed FeaturePython)
  n = 2
  ref = O_element
FEATURE [App::DocumentObjectGroupPython] G4_PLEXIGLASS  # scripted group (container) (typed FeaturePython)
  Dunit = g/cm3
  Dvalue = 1.19
  Group = -> [C_element083,H_element077,O_element079]
  conduct = 2
  density = 1
  expand = 3
  formula = G4_PLEXIGLASS
  name = G4_PLEXIGLASS
  specific = 4
FEATURE [App::DocumentObjectGroupPython] C_element084  label="C_element : 042"  # scripted group (container) (typed FeaturePython)
  n = 1
  ref = C_element
FEATURE [App::DocumentObjectGroupPython] H_element078  label="H_element : 040"  # scripted group (container) (typed FeaturePython)
  n = 2
  ref = H_element
FEATURE [App::DocumentObjectGroupPython] O_element080  label="O_element : 041"  # scripted group (container) (typed FeaturePython)
  n = 1
  ref = O_element
FEATURE [App::DocumentObjectGroupPython] G4_POLYOXYMETHYLENE  # scripted group (container) (typed FeaturePython)
  Dunit = g/cm3
  Dvalue = 1.425
  Group = -> [C_element084,H_element078,O_element080]
  conduct = 2
  density = 1
  expand = 3
  formula = G4_POLYOXYMETHYLENE
  name = G4_POLYOXYMETHYLENE
  specific = 4
FEATURE [App::DocumentObjectGroupPython] C_element085  label="C_element : 043"  # scripted group (container) (typed FeaturePython)
  n = 2
  ref = C_element
FEATURE [App::DocumentObjectGroupPython] H_element079  label="H_element : 041"  # scripted group (container) (typed FeaturePython)
  n = 4
  ref = H_element
FEATURE [App::DocumentObjectGroupPython] G4_POLYPROPYLENE  # scripted group (container) (typed FeaturePython)
  Dunit = g/cm3
  Dvalue = 0.9
  Group = -> [C_element085,H_element079]
  conduct = 2
  density = 1
  expand = 3
  formula = G4_POLYPROPYLENE
  name = G4_POLYPROPYLENE
  specific = 4
FEATURE [App::DocumentObjectGroupPython] C_element086  label="C_element : 044"  # scripted group (container) (typed FeaturePython)
  n = 8
  ref = C_element
FEATURE [App::DocumentObjectGroupPython] H_element080  label="H_element : 042"  # scripted group (container) (typed FeaturePython)
  n = 8
  ref = H_element
FEATURE [App::DocumentObjectGroupPython] G4_POLYSTYRENE  # scripted group (container) (typed FeaturePython)
  Dunit = g/cm3
  Dvalue = 1.06
  Group = -> [C_element086,H_element080]
  conduct = 2
  density = 1
  expand = 3
  formula = G4_POLYSTYRENE
  name = G4_POLYSTYRENE
  specific = 4
FEATURE [App::DocumentObjectGroupPython] C_element087  label="C_element : 045"  # scripted group (container) (typed FeaturePython)
  n = 2
  ref = C_element
FEATURE [App::DocumentObjectGroupPython] F_element014  label="F_element : 4"  # scripted group (container) (typed FeaturePython)
  n = 4
  ref = F_element
FEATURE [App::DocumentObjectGroupPython] G4_TEFLON  # scripted group (container) (typed FeaturePython)
  Dunit = g/cm3
  Dvalue = 2.2
  Group = -> [C_element087,F_element014]
  conduct = 2
  density = 1
  expand = 3
  formula = G4_TEFLON
  name = G4_TEFLON
  specific = 4
FEATURE [App::DocumentObjectGroupPython] C_element088  label="C_element : 046"  # scripted group (container) (typed FeaturePython)
  n = 2
  ref = C_element
FEATURE [App::DocumentObjectGroupPython] F_element015  label="F_element : 006"  # scripted group (container) (typed FeaturePython)
  n = 3
  ref = F_element
FEATURE [App::DocumentObjectGroupPython] Cl_element018  label="Cl_element : 008"  # scripted group (container) (typed FeaturePython)
  n = 1
  ref = Cl_element
FEATURE [App::DocumentObjectGroupPython] G4_POLYTRIFLUOROCHLOROETHYLENE  # scripted group (container) (typed FeaturePython)
  Dunit = g/cm3
  Dvalue = 2.1
  Group = -> [C_element088,F_element015,Cl_element018]
  conduct = 2
  density = 1
  expand = 3
  formula = G4_POLYTRIFLUOROCHLOROETHYLENE
  name = G4_POLYTRIFLUOROCHLOROETHYLENE
  specific = 4
FEATURE [App::DocumentObjectGroupPython] C_element089  label="C_element : 047"  # scripted group (container) (typed FeaturePython)
  n = 4
  ref = C_element
FEATURE [App::DocumentObjectGroupPython] H_element081  label="H_element : 043"  # scripted group (container) (typed FeaturePython)
  n = 6
  ref = H_element
FEATURE [App::DocumentObjectGroupPython] O_element081  label="O_element : 042"  # scripted group (container) (typed FeaturePython)
  n = 2
  ref = O_element
FEATURE [App::DocumentObjectGroupPython] G4_POLYVINYL_ACETATE  # scripted group (container) (typed FeaturePython)
  Dunit = g/cm3
  Dvalue = 1.19
  Group = -> [C_element089,H_element081,O_element081]
  conduct = 2
  density = 1
  expand = 3
  formula = G4_POLYVINYL_ACETATE
  name = G4_POLYVINYL_ACETATE
  specific = 4
FEATURE [App::DocumentObjectGroupPython] C_element090  label="C_element : 048"  # scripted group (container) (typed FeaturePython)
  n = 2
  ref = C_element
FEATURE [App::DocumentObjectGroupPython] H_element082  label="H_element : 044"  # scripted group (container) (typed FeaturePython)
  n = 4
  ref = H_element
FEATURE [App::DocumentObjectGroupPython] O_element082  label="O_element : 043"  # scripted group (container) (typed FeaturePython)
  n = 1
  ref = O_element
FEATURE [App::DocumentObjectGroupPython] G4_POLYVINYL_ALCOHOL  # scripted group (container) (typed FeaturePython)
  Dunit = g/cm3
  Dvalue = 1.3
  Group = -> [C_element090,H_element082,O_element082]
  conduct = 2
  density = 1
  expand = 3
  formula = G4_POLYVINYL_ALCOHOL
  name = G4_POLYVINYL_ALCOHOL
  specific = 4
FEATURE [App::DocumentObjectGroupPython] C_element091  label="C_element : 049"  # scripted group (container) (typed FeaturePython)
  n = 8
  ref = C_element
FEATURE [App::DocumentObjectGroupPython] H_element083  label="H_element : 045"  # scripted group (container) (typed FeaturePython)
  n = 14
  ref = H_element
FEATURE [App::DocumentObjectGroupPython] O_element083  label="O_element : 044"  # scripted group (container) (typed FeaturePython)
  n = 2
  ref = O_element
FEATURE [App::DocumentObjectGroupPython] G4_POLYVINYL_BUTYRAL  # scripted group (container) (typed FeaturePython)
  Dunit = g/cm3
  Dvalue = 1.12
  Group = -> [C_element091,H_element083,O_element083]
  conduct = 2
  density = 1
  expand = 3
  formula = G4_POLYVINYL_BUTYRAL
  name = G4_POLYVINYL_BUTYRAL
  specific = 4
FEATURE [App::DocumentObjectGroupPython] C_element092  label="C_element : 050"  # scripted group (container) (typed FeaturePython)
  n = 2
  ref = C_element
FEATURE [App::DocumentObjectGroupPython] H_element084  label="H_element : 046"  # scripted group (container) (typed FeaturePython)
  n = 3
  ref = H_element
FEATURE [App::DocumentObjectGroupPython] Cl_element019  label="Cl_element : 009"  # scripted group (container) (typed FeaturePython)
  n = 1
  ref = Cl_element
FEATURE [App::DocumentObjectGroupPython] G4_POLYVINYL_CHLORIDE  # scripted group (container) (typed FeaturePython)
  Dunit = g/cm3
  Dvalue = 1.3
  Group = -> [C_element092,H_element084,Cl_element019]
  conduct = 2
  density = 1
  expand = 3
  formula = G4_POLYVINYL_CHLORIDE
  name = G4_POLYVINYL_CHLORIDE
  specific = 4
FEATURE [App::DocumentObjectGroupPython] C_element093  label="C_element : 051"  # scripted group (container) (typed FeaturePython)
  n = 2
  ref = C_element
FEATURE [App::DocumentObjectGroupPython] H_element085  label="H_element : 047"  # scripted group (container) (typed FeaturePython)
  n = 2
  ref = H_element
FEATURE [App::DocumentObjectGroupPython] Cl_element020  label="Cl_element : 010"  # scripted group (container) (typed FeaturePython)
  n = 2
  ref = Cl_element
FEATURE [App::DocumentObjectGroupPython] G4_POLYVINYLIDENE_CHLORIDE  # scripted group (container) (typed FeaturePython)
  Dunit = g/cm3
  Dvalue = 1.7
  Group = -> [C_element093,H_element085,Cl_element020]
  conduct = 2
  density = 1
  expand = 3
  formula = G4_POLYVINYLIDENE_CHLORIDE
  name = G4_POLYVINYLIDENE_CHLORIDE
  specific = 4
FEATURE [App::DocumentObjectGroupPython] C_element094  label="C_element : 052"  # scripted group (container) (typed FeaturePython)
  n = 2
  ref = C_element
FEATURE [App::DocumentObjectGroupPython] H_element086  label="H_element : 048"  # scripted group (container) (typed FeaturePython)
  n = 2
  ref = H_element
FEATURE [App::DocumentObjectGroupPython] F_element016  label="F_element : 007"  # scripted group (container) (typed FeaturePython)
  n = 2
  ref = F_element
FEATURE [App::DocumentObjectGroupPython] G4_POLYVINYLIDENE_FLUORIDE  # scripted group (container) (typed FeaturePython)
  Dunit = g/cm3
  Dvalue = 1.76
  Group = -> [C_element094,H_element086,F_element016]
  conduct = 2
  density = 1
  expand = 3
  formula = G4_POLYVINYLIDENE_FLUORIDE
  name = G4_POLYVINYLIDENE_FLUORIDE
  specific = 4
FEATURE [App::DocumentObjectGroupPython] C_element095  label="C_element : 053"  # scripted group (container) (typed FeaturePython)
  n = 6
  ref = C_element
FEATURE [App::DocumentObjectGroupPython] H_element087  label="H_element : 9"  # scripted group (container) (typed FeaturePython)
  n = 9
  ref = H_element
FEATURE [App::DocumentObjectGroupPython] N_element037  label="N_element : 016"  # scripted group (container) (typed FeaturePython)
  n = 1
  ref = N_element
FEATURE [App::DocumentObjectGroupPython] O_element084  label="O_element : 045"  # scripted group (container) (typed FeaturePython)
  n = 1
  ref = O_element
FEATURE [App::DocumentObjectGroupPython] G4_POLYVINYL_PYRROLIDONE  # scripted group (container) (typed FeaturePython)
  Dunit = g/cm3
  Dvalue = 1.25
  Group = -> [C_element095,H_element087,N_element037,O_element084]
  conduct = 2
  density = 1
  expand = 3
  formula = G4_POLYVINYL_PYRROLIDONE
  name = G4_POLYVINYL_PYRROLIDONE
  specific = 4
FEATURE [App::DocumentObjectGroupPython] K_element008  label="K_element : 1"  # scripted group (container) (typed FeaturePython)
  n = 1
  ref = K_element
FEATURE [App::DocumentObjectGroupPython] I_element006  label="I_element : 003"  # scripted group (container) (typed FeaturePython)
  n = 1
  ref = I_element
FEATURE [App::DocumentObjectGroupPython] G4_POTASSIUM_IODIDE  # scripted group (container) (typed FeaturePython)
  Dunit = g/cm3
  Dvalue = 3.13
  Group = -> [K_element008,I_element006]
  conduct = 2
  density = 1
  expand = 3
  formula = G4_POTASSIUM_IODIDE
  name = G4_POTASSIUM_IODIDE
  specific = 4
FEATURE [App::DocumentObjectGroupPython] K_element009  label="K_element : 2"  # scripted group (container) (typed FeaturePython)
  n = 2
  ref = K_element
FEATURE [App::DocumentObjectGroupPython] O_element085  label="O_element : 046"  # scripted group (container) (typed FeaturePython)
  n = 1
  ref = O_element
FEATURE [App::DocumentObjectGroupPython] G4_POTASSIUM_OXIDE  # scripted group (container) (typed FeaturePython)
  Dunit = g/cm3
  Dvalue = 2.32
  Group = -> [K_element009,O_element085]
  conduct = 2
  density = 1
  expand = 3
  formula = G4_POTASSIUM_OXIDE
  name = G4_POTASSIUM_OXIDE
  specific = 4
FEATURE [App::DocumentObjectGroupPython] C_element096  label="C_element : 054"  # scripted group (container) (typed FeaturePython)
  n = 3
  ref = C_element
FEATURE [App::DocumentObjectGroupPython] H_element088  label="H_element : 049"  # scripted group (container) (typed FeaturePython)
  n = 8
  ref = H_element
FEATURE [App::DocumentObjectGroupPython] G4_PROPANE  # scripted group (container) (typed FeaturePython)
  Dunit = g/cm3
  Dvalue = 0.00187939
  Group = -> [C_element096,H_element088]
  conduct = 2
  density = 1
  expand = 3
  formula = G4_PROPANE
  name = G4_PROPANE
  specific = 4
FEATURE [App::DocumentObjectGroupPython] C_element097  label="C_element : 055"  # scripted group (container) (typed FeaturePython)
  n = 3
  ref = C_element
FEATURE [App::DocumentObjectGroupPython] H_element089  label="H_element : 050"  # scripted group (container) (typed FeaturePython)
  n = 8
  ref = H_element
FEATURE [App::DocumentObjectGroupPython] G4_lPROPANE  # scripted group (container) (typed FeaturePython)
  Dunit = g/cm3
  Dvalue = 0.43
  Group = -> [C_element097,H_element089]
  conduct = 2
  density = 1
  expand = 3
  formula = G4_lPROPANE
  name = G4_lPROPANE
  specific = 4
FEATURE [App::DocumentObjectGroupPython] C_element098  label="C_element : 056"  # scripted group (container) (typed FeaturePython)
  n = 3
  ref = C_element
FEATURE [App::DocumentObjectGroupPython] H_element090  label="H_element : 051"  # scripted group (container) (typed FeaturePython)
  n = 8
  ref = H_element
FEATURE [App::DocumentObjectGroupPython] O_element086  label="O_element : 047"  # scripted group (container) (typed FeaturePython)
  n = 1
  ref = O_element
FEATURE [App::DocumentObjectGroupPython] G4_N_PROPYL_ALCOHOL  label="G4_N-PROPYL_ALCOHOL"  # scripted group (container) (typed FeaturePython)
  Dunit = g/cm3
  Dvalue = 0.8035
  Group = -> [C_element098,H_element090,O_element086]
  conduct = 2
  density = 1
  expand = 3
  formula = G4_N-PROPYL_ALCOHOL
  name = G4_N-PROPYL_ALCOHOL
  specific = 4
FEATURE [App::DocumentObjectGroupPython] C_element099  label="C_element : 057"  # scripted group (container) (typed FeaturePython)
  n = 5
  ref = C_element
FEATURE [App::DocumentObjectGroupPython] H_element091  label="H_element : 052"  # scripted group (container) (typed FeaturePython)
  n = 5
  ref = H_element
FEATURE [App::DocumentObjectGroupPython] N_element038  label="N_element : 017"  # scripted group (container) (typed FeaturePython)
  n = 1
  ref = N_element
FEATURE [App::DocumentObjectGroupPython] G4_PYRIDINE  # scripted group (container) (typed FeaturePython)
  Dunit = g/cm3
  Dvalue = 0.9819
  Group = -> [C_element099,H_element091,N_element038]
  conduct = 2
  density = 1
  expand = 3
  formula = G4_PYRIDINE
  name = G4_PYRIDINE
  specific = 4
FEATURE [App::DocumentObjectGroupPython] H_element092  label="H_element : 0.144"  # scripted group (container) (typed FeaturePython)
  n = 0.143711
FEATURE [App::DocumentObjectGroupPython] C_element100  label="C_element : 0.856"  # scripted group (container) (typed FeaturePython)
  n = 0.856289
FEATURE [App::DocumentObjectGroupPython] G4_RUBBER_BUTYL  # scripted group (container) (typed FeaturePython)
  Dunit = g/cm3
  Dvalue = 0.92
  Group = -> [H_element092,C_element100]
  conduct = 2
  density = 1
  expand = 3
  formula = G4_RUBBER_BUTYL
  name = G4_RUBBER_BUTYL
  specific = 4
FEATURE [App::DocumentObjectGroupPython] H_element093  label="H_element : 0.118"  # scripted group (container) (typed FeaturePython)
  n = 0.118371
FEATURE [App::DocumentObjectGroupPython] C_element101  label="C_element : 0.882"  # scripted group (container) (typed FeaturePython)
  n = 0.881629
FEATURE [App::DocumentObjectGroupPython] G4_RUBBER_NATURAL  # scripted group (container) (typed FeaturePython)
  Dunit = g/cm3
  Dvalue = 0.92
  Group = -> [H_element093,C_element101]
  conduct = 2
  density = 1
  expand = 3
  formula = G4_RUBBER_NATURAL
  name = G4_RUBBER_NATURAL
  specific = 4
FEATURE [App::DocumentObjectGroupPython] H_element094  label="H_element : 0.145"  # scripted group (container) (typed FeaturePython)
  n = 0.05692
FEATURE [App::DocumentObjectGroupPython] C_element102  label="C_element : 0.543"  # scripted group (container) (typed FeaturePython)
  n = 0.542646
FEATURE [App::DocumentObjectGroupPython] Cl_element021  label="Cl_element : 0.400"  # scripted group (container) (typed FeaturePython)
  n = 0.400434
FEATURE [App::DocumentObjectGroupPython] G4_RUBBER_NEOPRENE  # scripted group (container) (typed FeaturePython)
  Dunit = g/cm3
  Dvalue = 1.23
  Group = -> [H_element094,C_element102,Cl_element021]
  conduct = 2
  density = 1
  expand = 3
  formula = G4_RUBBER_NEOPRENE
  name = G4_RUBBER_NEOPRENE
  specific = 4
FEATURE [App::DocumentObjectGroupPython] Si_element006  label="Si_element : 1"  # scripted group (container) (typed FeaturePython)
  n = 1
  ref = Si_element
FEATURE [App::DocumentObjectGroupPython] O_element087  label="O_element : 048"  # scripted group (container) (typed FeaturePython)
  n = 2
  ref = O_element
FEATURE [App::DocumentObjectGroupPython] G4_SILICON_DIOXIDE  # scripted group (container) (typed FeaturePython)
  Dunit = g/cm3
  Dvalue = 2.32
  Group = -> [Si_element006,O_element087]
  conduct = 2
  density = 1
  expand = 3
  formula = G4_SILICON_DIOXIDE
  name = G4_SILICON_DIOXIDE
  specific = 4
FEATURE [App::DocumentObjectGroupPython] Ag_element002  label="Ag_element : 1"  # scripted group (container) (typed FeaturePython)
  n = 1
  ref = Ag_element
FEATURE [App::DocumentObjectGroupPython] Br_element005  label="Br_element : 003"  # scripted group (container) (typed FeaturePython)
  n = 1
  ref = Br_element
FEATURE [App::DocumentObjectGroupPython] G4_SILVER_BROMIDE  # scripted group (container) (typed FeaturePython)
  Dunit = g/cm3
  Dvalue = 6.473
  Group = -> [Ag_element002,Br_element005]
  conduct = 2
  density = 1
  expand = 3
  formula = G4_SILVER_BROMIDE
  name = G4_SILVER_BROMIDE
  specific = 4
FEATURE [App::DocumentObjectGroupPython] Ag_element003  label="Ag_element : 002"  # scripted group (container) (typed FeaturePython)
  n = 1
  ref = Ag_element
FEATURE [App::DocumentObjectGroupPython] Cl_element022  label="Cl_element : 011"  # scripted group (container) (typed FeaturePython)
  n = 1
  ref = Cl_element
FEATURE [App::DocumentObjectGroupPython] G4_SILVER_CHLORIDE  # scripted group (container) (typed FeaturePython)
  Dunit = g/cm3
  Dvalue = 5.56
  Group = -> [Ag_element003,Cl_element022]
  conduct = 2
  density = 1
  expand = 3
  formula = G4_SILVER_CHLORIDE
  name = G4_SILVER_CHLORIDE
  specific = 4
FEATURE [App::DocumentObjectGroupPython] Br_element006  label="Br_element : 0.423"  # scripted group (container) (typed FeaturePython)
  n = 0.422895
FEATURE [App::DocumentObjectGroupPython] Ag_element004  label="Ag_element : 0.574"  # scripted group (container) (typed FeaturePython)
  n = 0.573748
FEATURE [App::DocumentObjectGroupPython] I_element007  label="I_element : 0.649"  # scripted group (container) (typed FeaturePython)
  n = 0.003357
FEATURE [App::DocumentObjectGroupPython] G4_SILVER_HALIDES  # scripted group (container) (typed FeaturePython)
  Dunit = g/cm3
  Dvalue = 6.47
  Group = -> [Br_element006,Ag_element004,I_element007]
  conduct = 2
  density = 1
  expand = 3
  formula = G4_SILVER_HALIDES
  name = G4_SILVER_HALIDES
  specific = 4
FEATURE [App::DocumentObjectGroupPython] Ag_element005  label="Ag_element : 003"  # scripted group (container) (typed FeaturePython)
  n = 1
  ref = Ag_element
FEATURE [App::DocumentObjectGroupPython] I_element008  label="I_element : 004"  # scripted group (container) (typed FeaturePython)
  n = 1
  ref = I_element
FEATURE [App::DocumentObjectGroupPython] G4_SILVER_IODIDE  # scripted group (container) (typed FeaturePython)
  Dunit = g/cm3
  Dvalue = 6.01
  Group = -> [Ag_element005,I_element008]
  conduct = 2
  density = 1
  expand = 3
  formula = G4_SILVER_IODIDE
  name = G4_SILVER_IODIDE
  specific = 4
FEATURE [App::DocumentObjectGroupPython] H_element095  label="H_element : 0.100"  # scripted group (container) (typed FeaturePython)
  n = 0.1
FEATURE [App::DocumentObjectGroupPython] C_element103  label="C_element : 0.204"  # scripted group (container) (typed FeaturePython)
  n = 0.204
FEATURE [App::DocumentObjectGroupPython] N_element039  label="N_element : 0.759"  # scripted group (container) (typed FeaturePython)
  n = 0.042
FEATURE [App::DocumentObjectGroupPython] O_element088  label="O_element : 0.645"  # scripted group (container) (typed FeaturePython)
  n = 0.645
FEATURE [App::DocumentObjectGroupPython] Na_element013  label="Na_element : 0.100"  # scripted group (container) (typed FeaturePython)
  n = 0.002
FEATURE [App::DocumentObjectGroupPython] P_element009  label="P_element : 0.107"  # scripted group (container) (typed FeaturePython)
  n = 0.001
FEATURE [App::DocumentObjectGroupPython] S_element020  label="S_element : 0.021"  # scripted group (container) (typed FeaturePython)
  n = 0.002
FEATURE [App::DocumentObjectGroupPython] Cl_element023  label="Cl_element : 0.590"  # scripted group (container) (typed FeaturePython)
  n = 0.003
FEATURE [App::DocumentObjectGroupPython] K_element010  label="K_element : 0.001"  # scripted group (container) (typed FeaturePython)
  n = 0.001
FEATURE [App::DocumentObjectGroupPython] G4_SKIN_ICRP  # scripted group (container) (typed FeaturePython)
  Dunit = g/cm3
  Dvalue = 1.09
  Group = -> [H_element095,C_element103,N_element039,O_element088,Na_element013,P_element009,S_element020,Cl_element023,K_element010]
  conduct = 2
  density = 1
  expand = 3
  formula = G4_SKIN_ICRP
  name = G4_SKIN_ICRP
  specific = 4
FEATURE [App::DocumentObjectGroupPython] Na_element014  label="Na_element : 2"  # scripted group (container) (typed FeaturePython)
  n = 2
  ref = Na_element
FEATURE [App::DocumentObjectGroupPython] C_element104  label="C_element : 058"  # scripted group (container) (typed FeaturePython)
  n = 1
  ref = C_element
FEATURE [App::DocumentObjectGroupPython] O_element089  label="O_element : 049"  # scripted group (container) (typed FeaturePython)
  n = 3
  ref = O_element
FEATURE [App::DocumentObjectGroupPython] G4_SODIUM_CARBONATE  # scripted group (container) (typed FeaturePython)
  Dunit = g/cm3
  Dvalue = 2.532
  Group = -> [Na_element014,C_element104,O_element089]
  conduct = 2
  density = 1
  expand = 3
  formula = G4_SODIUM_CARBONATE
  name = G4_SODIUM_CARBONATE
  specific = 4
FEATURE [App::DocumentObjectGroupPython] Na_element015  label="Na_element : 1"  # scripted group (container) (typed FeaturePython)
  n = 1
  ref = Na_element
FEATURE [App::DocumentObjectGroupPython] I_element009  label="I_element : 005"  # scripted group (container) (typed FeaturePython)
  n = 1
  ref = I_element
FEATURE [App::DocumentObjectGroupPython] G4_SODIUM_IODIDE  # scripted group (container) (typed FeaturePython)
  Dunit = g/cm3
  Dvalue = 3.667
  Group = -> [Na_element015,I_element009]
  conduct = 2
  density = 1
  expand = 3
  formula = G4_SODIUM_IODIDE
  name = G4_SODIUM_IODIDE
  specific = 4
FEATURE [App::DocumentObjectGroupPython] Na_element016  label="Na_element : 003"  # scripted group (container) (typed FeaturePython)
  n = 2
  ref = Na_element
FEATURE [App::DocumentObjectGroupPython] O_element090  label="O_element : 050"  # scripted group (container) (typed FeaturePython)
  n = 1
  ref = O_element
FEATURE [App::DocumentObjectGroupPython] G4_SODIUM_MONOXIDE  # scripted group (container) (typed FeaturePython)
  Dunit = g/cm3
  Dvalue = 2.27
  Group = -> [Na_element016,O_element090]
  conduct = 2
  density = 1
  expand = 3
  formula = G4_SODIUM_MONOXIDE
  name = G4_SODIUM_MONOXIDE
  specific = 4
FEATURE [App::DocumentObjectGroupPython] Na_element017  label="Na_element : 004"  # scripted group (container) (typed FeaturePython)
  n = 1
  ref = Na_element
FEATURE [App::DocumentObjectGroupPython] N_element040  label="N_element : 018"  # scripted group (container) (typed FeaturePython)
  n = 1
  ref = N_element
FEATURE [App::DocumentObjectGroupPython] O_element091  label="O_element : 051"  # scripted group (container) (typed FeaturePython)
  n = 3
  ref = O_element
FEATURE [App::DocumentObjectGroupPython] G4_SODIUM_NITRATE  # scripted group (container) (typed FeaturePython)
  Dunit = g/cm3
  Dvalue = 2.261
  Group = -> [Na_element017,N_element040,O_element091]
  conduct = 2
  density = 1
  expand = 3
  formula = G4_SODIUM_NITRATE
  name = G4_SODIUM_NITRATE
  specific = 4
FEATURE [App::DocumentObjectGroupPython] C_element105  label="C_element : 059"  # scripted group (container) (typed FeaturePython)
  n = 14
  ref = C_element
FEATURE [App::DocumentObjectGroupPython] H_element096  label="H_element : 053"  # scripted group (container) (typed FeaturePython)
  n = 12
  ref = H_element
FEATURE [App::DocumentObjectGroupPython] G4_STILBENE  # scripted group (container) (typed FeaturePython)
  Dunit = g/cm3
  Dvalue = 0.9707
  Group = -> [C_element105,H_element096]
  conduct = 2
  density = 1
  expand = 3
  formula = G4_STILBENE
  name = G4_STILBENE
  specific = 4
FEATURE [App::DocumentObjectGroupPython] C_element106  label="C_element : 12"  # scripted group (container) (typed FeaturePython)
  n = 12
  ref = C_element
FEATURE [App::DocumentObjectGroupPython] H_element097  label="H_element : 22"  # scripted group (container) (typed FeaturePython)
  n = 22
  ref = H_element
FEATURE [App::DocumentObjectGroupPython] O_element092  label="O_element : 11"  # scripted group (container) (typed FeaturePython)
  n = 11
  ref = O_element
FEATURE [App::DocumentObjectGroupPython] G4_SUCROSE  # scripted group (container) (typed FeaturePython)
  Dunit = g/cm3
  Dvalue = 1.5805
  Group = -> [C_element106,H_element097,O_element092]
  conduct = 2
  density = 1
  expand = 3
  formula = G4_SUCROSE
  name = G4_SUCROSE
  specific = 4
FEATURE [App::DocumentObjectGroupPython] C_element107  label="C_element : 18"  # scripted group (container) (typed FeaturePython)
  n = 18
  ref = C_element
FEATURE [App::DocumentObjectGroupPython] H_element098  label="H_element : 054"  # scripted group (container) (typed FeaturePython)
  n = 14
  ref = H_element
FEATURE [App::DocumentObjectGroupPython] G4_TERPHENYL  # scripted group (container) (typed FeaturePython)
  Dunit = g/cm3
  Dvalue = 1.24
  Group = -> [C_element107,H_element098]
  conduct = 2
  density = 1
  expand = 3
  formula = G4_TERPHENYL
  name = G4_TERPHENYL
  specific = 4
FEATURE [App::DocumentObjectGroupPython] H_element099  label="H_element : 0.146"  # scripted group (container) (typed FeaturePython)
  n = 0.106
FEATURE [App::DocumentObjectGroupPython] C_element108  label="C_element : 0.883"  # scripted group (container) (typed FeaturePython)
  n = 0.099
FEATURE [App::DocumentObjectGroupPython] N_element041  label="N_element : 0.020"  # scripted group (container) (typed FeaturePython)
  n = 0.02
FEATURE [App::DocumentObjectGroupPython] O_element093  label="O_element : 0.766"  # scripted group (container) (typed FeaturePython)
  n = 0.766
FEATURE [App::DocumentObjectGroupPython] Na_element018  label="Na_element : 0.101"  # scripted group (container) (typed FeaturePython)
  n = 0.002
FEATURE [App::DocumentObjectGroupPython] P_element010  label="P_element : 0.108"  # scripted group (container) (typed FeaturePython)
  n = 0.001
FEATURE [App::DocumentObjectGroupPython] S_element021  label="S_element : 0.022"  # scripted group (container) (typed FeaturePython)
  n = 0.002
FEATURE [App::DocumentObjectGroupPython] Cl_element024  label="Cl_element : 0.002"  # scripted group (container) (typed FeaturePython)
  n = 0.002
FEATURE [App::DocumentObjectGroupPython] K_element011  label="K_element : 0.017"  # scripted group (container) (typed FeaturePython)
  n = 0.002
FEATURE [App::DocumentObjectGroupPython] G4_TESTIS_ICRP  # scripted group (container) (typed FeaturePython)
  Dunit = g/cm3
  Dvalue = 1.04
  Group = -> [H_element099,C_element108,N_element041,O_element093,Na_element018,P_element010,S_element021,Cl_element024,K_element011]
  conduct = 2
  density = 1
  expand = 3
  formula = G4_TESTIS_ICRP
  name = G4_TESTIS_ICRP
  specific = 4
FEATURE [App::DocumentObjectGroupPython] C_element109  label="C_element : 060"  # scripted group (container) (typed FeaturePython)
  n = 2
  ref = C_element
FEATURE [App::DocumentObjectGroupPython] Cl_element025  label="Cl_element : 012"  # scripted group (container) (typed FeaturePython)
  n = 4
  ref = Cl_element
FEATURE [App::DocumentObjectGroupPython] G4_TETRACHLOROETHYLENE  # scripted group (container) (typed FeaturePython)
  Dunit = g/cm3
  Dvalue = 1.625
  Group = -> [C_element109,Cl_element025]
  conduct = 2
  density = 1
  expand = 3
  formula = G4_TETRACHLOROETHYLENE
  name = G4_TETRACHLOROETHYLENE
  specific = 4
FEATURE [App::DocumentObjectGroupPython] Tl_element001  label="Tl_element : 1"  # scripted group (container) (typed FeaturePython)
  n = 1
  ref = Tl_element
FEATURE [App::DocumentObjectGroupPython] Cl_element026  label="Cl_element : 013"  # scripted group (container) (typed FeaturePython)
  n = 1
  ref = Cl_element
FEATURE [App::DocumentObjectGroupPython] G4_THALLIUM_CHLORIDE  # scripted group (container) (typed FeaturePython)
  Dunit = g/cm3
  Dvalue = 7.004
  Group = -> [Tl_element001,Cl_element026]
  conduct = 2
  density = 1
  expand = 3
  formula = G4_THALLIUM_CHLORIDE
  name = G4_THALLIUM_CHLORIDE
  specific = 4
FEATURE [App::DocumentObjectGroupPython] H_element100  label="H_element : 0.147"  # scripted group (container) (typed FeaturePython)
  n = 0.105
FEATURE [App::DocumentObjectGroupPython] C_element110  label="C_element : 0.256"  # scripted group (container) (typed FeaturePython)
  n = 0.256
FEATURE [App::DocumentObjectGroupPython] N_element042  label="N_element : 0.760"  # scripted group (container) (typed FeaturePython)
  n = 0.027
FEATURE [App::DocumentObjectGroupPython] O_element094  label="O_element : 0.602"  # scripted group (container) (typed FeaturePython)
  n = 0.602
FEATURE [App::DocumentObjectGroupPython] Na_element019  label="Na_element : 0.102"  # scripted group (container) (typed FeaturePython)
  n = 0.001
FEATURE [App::DocumentObjectGroupPython] P_element011  label="P_element : 0.109"  # scripted group (container) (typed FeaturePython)
  n = 0.002
FEATURE [App::DocumentObjectGroupPython] S_element022  label="S_element : 0.023"  # scripted group (container) (typed FeaturePython)
  n = 0.003
FEATURE [App::DocumentObjectGroupPython] Cl_element027  label="Cl_element : 0.591"  # scripted group (container) (typed FeaturePython)
  n = 0.002
FEATURE [App::DocumentObjectGroupPython] K_element012  label="K_element : 0.018"  # scripted group (container) (typed FeaturePython)
  n = 0.002
FEATURE [App::DocumentObjectGroupPython] G4_TISSUE_SOFT_ICRP  # scripted group (container) (typed FeaturePython)
  Dunit = g/cm3
  Dvalue = 1.03
  Group = -> [H_element100,C_element110,N_element042,O_element094,Na_element019,P_element011,S_element022,Cl_element027,K_element012]
  conduct = 2
  density = 1
  expand = 3
  formula = G4_TISSUE_SOFT_ICRP
  name = G4_TISSUE_SOFT_ICRP
  specific = 4
FEATURE [App::DocumentObjectGroupPython] H_element101  label="H_element : 0.148"  # scripted group (container) (typed FeaturePython)
  n = 0.101
FEATURE [App::DocumentObjectGroupPython] C_element111  label="C_element : 0.111"  # scripted group (container) (typed FeaturePython)
  n = 0.111
FEATURE [App::DocumentObjectGroupPython] N_element043  label="N_element : 0.026"  # scripted group (container) (typed FeaturePython)
  n = 0.026
FEATURE [App::DocumentObjectGroupPython] O_element095  label="O_element : 0.762"  # scripted group (container) (typed FeaturePython)
  n = 0.762
FEATURE [App::DocumentObjectGroupPython] G4_TISSUE_SOFT_ICRU_4  label="G4_TISSUE_SOFT_ICRU-4"  # scripted group (container) (typed FeaturePython)
  Dunit = g/cm3
  Dvalue = 1
  Group = -> [H_element101,C_element111,N_element043,O_element095]
  conduct = 2
  density = 1
  expand = 3
  formula = G4_TISSUE_SOFT_ICRU-4
  name = G4_TISSUE_SOFT_ICRU-4
  specific = 4
FEATURE [App::DocumentObjectGroupPython] H_element102  label="H_element : 0.149"  # scripted group (container) (typed FeaturePython)
  n = 0.101869
FEATURE [App::DocumentObjectGroupPython] C_element112  label="C_element : 0.456"  # scripted group (container) (typed FeaturePython)
  n = 0.456179
FEATURE [App::DocumentObjectGroupPython] N_element044  label="N_element : 0.761"  # scripted group (container) (typed FeaturePython)
  n = 0.035172
FEATURE [App::DocumentObjectGroupPython] O_element096  label="O_element : 0.407"  # scripted group (container) (typed FeaturePython)
  n = 0.40678
FEATURE [App::DocumentObjectGroupPython] G4_TISSUE_METHANE  label="G4_TISSUE-METHANE"  # scripted group (container) (typed FeaturePython)
  Dunit = g/cm3
  Dvalue = 0.00106409
  Group = -> [H_element102,C_element112,N_element044,O_element096]
  conduct = 2
  density = 1
  expand = 3
  formula = G4_TISSUE-METHANE
  name = G4_TISSUE-METHANE
  specific = 4
FEATURE [App::DocumentObjectGroupPython] H_element103  label="H_element : 0.103"  # scripted group (container) (typed FeaturePython)
  n = 0.102672
FEATURE [App::DocumentObjectGroupPython] C_element113  label="C_element : 0.569"  # scripted group (container) (typed FeaturePython)
  n = 0.56894
FEATURE [App::DocumentObjectGroupPython] N_element045  label="N_element : 0.762"  # scripted group (container) (typed FeaturePython)
  n = 0.035022
FEATURE [App::DocumentObjectGroupPython] O_element097  label="O_element : 0.293"  # scripted group (container) (typed FeaturePython)
  n = 0.293366
FEATURE [App::DocumentObjectGroupPython] G4_TISSUE_PROPANE  label="G4_TISSUE-PROPANE"  # scripted group (container) (typed FeaturePython)
  Dunit = g/cm3
  Dvalue = 0.00182628
  Group = -> [H_element103,C_element113,N_element045,O_element097]
  conduct = 2
  density = 1
  expand = 3
  formula = G4_TISSUE-PROPANE
  name = G4_TISSUE-PROPANE
  specific = 4
FEATURE [App::DocumentObjectGroupPython] Ti_element003  label="Ti_element : 1"  # scripted group (container) (typed FeaturePython)
  n = 1
  ref = Ti_element
FEATURE [App::DocumentObjectGroupPython] O_element098  label="O_element : 052"  # scripted group (container) (typed FeaturePython)
  n = 2
  ref = O_element
FEATURE [App::DocumentObjectGroupPython] G4_TITANIUM_DIOXIDE  # scripted group (container) (typed FeaturePython)
  Dunit = g/cm3
  Dvalue = 4.26
  Group = -> [Ti_element003,O_element098]
  conduct = 2
  density = 1
  expand = 3
  formula = G4_TITANIUM_DIOXIDE
  name = G4_TITANIUM_DIOXIDE
  specific = 4
FEATURE [App::DocumentObjectGroupPython] C_element114  label="C_element : 061"  # scripted group (container) (typed FeaturePython)
  n = 7
  ref = C_element
FEATURE [App::DocumentObjectGroupPython] H_element104  label="H_element : 055"  # scripted group (container) (typed FeaturePython)
  n = 8
  ref = H_element
FEATURE [App::DocumentObjectGroupPython] G4_TOLUENE  # scripted group (container) (typed FeaturePython)
  Dunit = g/cm3
  Dvalue = 0.8669
  Group = -> [C_element114,H_element104]
  conduct = 2
  density = 1
  expand = 3
  formula = G4_TOLUENE
  name = G4_TOLUENE
  specific = 4
FEATURE [App::DocumentObjectGroupPython] C_element115  label="C_element : 062"  # scripted group (container) (typed FeaturePython)
  n = 2
  ref = C_element
FEATURE [App::DocumentObjectGroupPython] H_element105  label="H_element : 056"  # scripted group (container) (typed FeaturePython)
  n = 1
  ref = H_element
FEATURE [App::DocumentObjectGroupPython] Cl_element028  label="Cl_element : 014"  # scripted group (container) (typed FeaturePython)
  n = 3
  ref = Cl_element
FEATURE [App::DocumentObjectGroupPython] G4_TRICHLOROETHYLENE  # scripted group (container) (typed FeaturePython)
  Dunit = g/cm3
  Dvalue = 1.46
  Group = -> [C_element115,H_element105,Cl_element028]
  conduct = 2
  density = 1
  expand = 3
  formula = G4_TRICHLOROETHYLENE
  name = G4_TRICHLOROETHYLENE
  specific = 4
FEATURE [App::DocumentObjectGroupPython] C_element116  label="C_element : 063"  # scripted group (container) (typed FeaturePython)
  n = 6
  ref = C_element
FEATURE [App::DocumentObjectGroupPython] H_element106  label="H_element : 15"  # scripted group (container) (typed FeaturePython)
  n = 15
  ref = H_element
FEATURE [App::DocumentObjectGroupPython] O_element099  label="O_element : 053"  # scripted group (container) (typed FeaturePython)
  n = 4
  ref = O_element
FEATURE [App::DocumentObjectGroupPython] P_element012  label="P_element : 1"  # scripted group (container) (typed FeaturePython)
  n = 1
  ref = P_element
FEATURE [App::DocumentObjectGroupPython] G4_TRIETHYL_PHOSPHATE  # scripted group (container) (typed FeaturePython)
  Dunit = g/cm3
  Dvalue = 1.07
  Group = -> [C_element116,H_element106,O_element099,P_element012]
  conduct = 2
  density = 1
  expand = 3
  formula = G4_TRIETHYL_PHOSPHATE
  name = G4_TRIETHYL_PHOSPHATE
  specific = 4
FEATURE [App::DocumentObjectGroupPython] W_element003  label="W_element : 003"  # scripted group (container) (typed FeaturePython)
  n = 1
  ref = W_element
FEATURE [App::DocumentObjectGroupPython] F_element017  label="F_element : 6"  # scripted group (container) (typed FeaturePython)
  n = 6
  ref = F_element
FEATURE [App::DocumentObjectGroupPython] G4_TUNGSTEN_HEXAFLUORIDE  # scripted group (container) (typed FeaturePython)
  Dunit = g/cm3
  Dvalue = 2.4
  Group = -> [W_element003,F_element017]
  conduct = 2
  density = 1
  expand = 3
  formula = G4_TUNGSTEN_HEXAFLUORIDE
  name = G4_TUNGSTEN_HEXAFLUORIDE
  specific = 4
FEATURE [App::DocumentObjectGroupPython] U_element001  label="U_element : 1"  # scripted group (container) (typed FeaturePython)
  n = 1
  ref = U_element
FEATURE [App::DocumentObjectGroupPython] C_element117  label="C_element : 064"  # scripted group (container) (typed FeaturePython)
  n = 2
  ref = C_element
FEATURE [App::DocumentObjectGroupPython] G4_URANIUM_DICARBIDE  # scripted group (container) (typed FeaturePython)
  Dunit = g/cm3
  Dvalue = 11.28
  Group = -> [U_element001,C_element117]
  conduct = 2
  density = 1
  expand = 3
  formula = G4_URANIUM_DICARBIDE
  name = G4_URANIUM_DICARBIDE
  specific = 4
FEATURE [App::DocumentObjectGroupPython] U_element002  label="U_element : 002"  # scripted group (container) (typed FeaturePython)
  n = 1
  ref = U_element
FEATURE [App::DocumentObjectGroupPython] C_element118  label="C_element : 065"  # scripted group (container) (typed FeaturePython)
  n = 1
  ref = C_element
FEATURE [App::DocumentObjectGroupPython] G4_URANIUM_MONOCARBIDE  # scripted group (container) (typed FeaturePython)
  Dunit = g/cm3
  Dvalue = 13.63
  Group = -> [U_element002,C_element118]
  conduct = 2
  density = 1
  expand = 3
  formula = G4_URANIUM_MONOCARBIDE
  name = G4_URANIUM_MONOCARBIDE
  specific = 4
FEATURE [App::DocumentObjectGroupPython] U_element003  label="U_element : 003"  # scripted group (container) (typed FeaturePython)
  n = 1
  ref = U_element
FEATURE [App::DocumentObjectGroupPython] O_element100  label="O_element : 054"  # scripted group (container) (typed FeaturePython)
  n = 2
  ref = O_element
FEATURE [App::DocumentObjectGroupPython] G4_URANIUM_OXIDE  # scripted group (container) (typed FeaturePython)
  Dunit = g/cm3
  Dvalue = 10.96
  Group = -> [U_element003,O_element100]
  conduct = 2
  density = 1
  expand = 3
  formula = G4_URANIUM_OXIDE
  name = G4_URANIUM_OXIDE
  specific = 4
FEATURE [App::DocumentObjectGroupPython] C_element119  label="C_element : 066"  # scripted group (container) (typed FeaturePython)
  n = 1
  ref = C_element
FEATURE [App::DocumentObjectGroupPython] H_element107  label="H_element : 057"  # scripted group (container) (typed FeaturePython)
  n = 4
  ref = H_element
FEATURE [App::DocumentObjectGroupPython] N_element046  label="N_element : 019"  # scripted group (container) (typed FeaturePython)
  n = 2
  ref = N_element
FEATURE [App::DocumentObjectGroupPython] O_element101  label="O_element : 055"  # scripted group (container) (typed FeaturePython)
  n = 1
  ref = O_element
FEATURE [App::DocumentObjectGroupPython] G4_UREA  # scripted group (container) (typed FeaturePython)
  Dunit = g/cm3
  Dvalue = 1.323
  Group = -> [C_element119,H_element107,N_element046,O_element101]
  conduct = 2
  density = 1
  expand = 3
  formula = G4_UREA
  name = G4_UREA
  specific = 4
FEATURE [App::DocumentObjectGroupPython] C_element120  label="C_element : 067"  # scripted group (container) (typed FeaturePython)
  n = 5
  ref = C_element
FEATURE [App::DocumentObjectGroupPython] H_element108  label="H_element : 058"  # scripted group (container) (typed FeaturePython)
  n = 11
  ref = H_element
FEATURE [App::DocumentObjectGroupPython] N_element047  label="N_element : 020"  # scripted group (container) (typed FeaturePython)
  n = 1
  ref = N_element
FEATURE [App::DocumentObjectGroupPython] O_element102  label="O_element : 056"  # scripted group (container) (typed FeaturePython)
  n = 2
  ref = O_element
FEATURE [App::DocumentObjectGroupPython] G4_VALINE  # scripted group (container) (typed FeaturePython)
  Dunit = g/cm3
  Dvalue = 1.23
  Group = -> [C_element120,H_element108,N_element047,O_element102]
  conduct = 2
  density = 1
  expand = 3
  formula = G4_VALINE
  name = G4_VALINE
  specific = 4
FEATURE [App::DocumentObjectGroupPython] H_element109  label="H_element : 0.009"  # scripted group (container) (typed FeaturePython)
  n = 0.009417
FEATURE [App::DocumentObjectGroupPython] C_element121  label="C_element : 0.281"  # scripted group (container) (typed FeaturePython)
  n = 0.280555
FEATURE [App::DocumentObjectGroupPython] F_element018  label="F_element : 0.710"  # scripted group (container) (typed FeaturePython)
  n = 0.710028
FEATURE [App::DocumentObjectGroupPython] G4_VITON  # scripted group (container) (typed FeaturePython)
  Dunit = g/cm3
  Dvalue = 1.8
  Group = -> [H_element109,C_element121,F_element018]
  conduct = 2
  density = 1
  expand = 3
  formula = G4_VITON
  name = G4_VITON
  specific = 4
FEATURE [App::DocumentObjectGroupPython] H_element110  label="H_element : 059"  # scripted group (container) (typed FeaturePython)
  n = 2
  ref = H_element
FEATURE [App::DocumentObjectGroupPython] O_element103  label="O_element : 057"  # scripted group (container) (typed FeaturePython)
  n = 1
  ref = O_element
FEATURE [App::DocumentObjectGroupPython] G4_WATER  # scripted group (container) (typed FeaturePython)
  Dunit = g/cm3
  Dvalue = 1
  Group = -> [H_element110,O_element103]
  conduct = 2
  density = 1
  expand = 3
  formula = G4_WATER
  name = G4_WATER
  specific = 4
FEATURE [App::DocumentObjectGroupPython] H_element111  label="H_element : 060"  # scripted group (container) (typed FeaturePython)
  n = 2
  ref = H_element
FEATURE [App::DocumentObjectGroupPython] O_element104  label="O_element : 058"  # scripted group (container) (typed FeaturePython)
  n = 1
  ref = O_element
FEATURE [App::DocumentObjectGroupPython] G4_WATER_VAPOR  # scripted group (container) (typed FeaturePython)
  Dunit = g/cm3
  Dvalue = 0.000756182
  Group = -> [H_element111,O_element104]
  conduct = 2
  density = 1
  expand = 3
  formula = G4_WATER_VAPOR
  name = G4_WATER_VAPOR
  specific = 4
FEATURE [App::DocumentObjectGroupPython] C_element122  label="C_element : 068"  # scripted group (container) (typed FeaturePython)
  n = 8
  ref = C_element
FEATURE [App::DocumentObjectGroupPython] H_element112  label="H_element : 061"  # scripted group (container) (typed FeaturePython)
  n = 10
  ref = H_element
FEATURE [App::DocumentObjectGroupPython] G4_XYLENE  # scripted group (container) (typed FeaturePython)
  Dunit = g/cm3
  Dvalue = 0.87
  Group = -> [C_element122,H_element112]
  conduct = 2
  density = 1
  expand = 3
  formula = G4_XYLENE
  name = G4_XYLENE
  specific = 4
FEATURE [App::DocumentObjectGroupPython] C_element123  label="C_element : 069"  # scripted group (container) (typed FeaturePython)
  n = 1
  ref = C_element
FEATURE [App::DocumentObjectGroupPython] G4_GRAPHITE  # scripted group (container) (typed FeaturePython)
  Dunit = g/cm3
  Dvalue = 2.21
  Group = -> [C_element123]
  conduct = 2
  density = 1
  expand = 3
  formula = G4_GRAPHITE
  name = G4_GRAPHITE
  specific = 4
FEATURE [App::DocumentObjectGroupPython] NIST  # scripted group (container) (typed FeaturePython)
  Group = -> [G4_A_150_TISSUE,G4_ACETONE,G4_ACETYLENE,G4_ADENINE,G4_ADIPOSE_TISSUE_ICRP,G4_AIR,G4_ALANINE,G4_ALUMINUM_OXIDE,G4_AMBER,G4_AMMONIA,G4_ANILINE,G4_ANTHRACENE,G4_B_100_BONE,G4_BAKELITE,G4_BARIUM_FLUORIDE,G4_BARIUM_SULFATE,G4_BENZENE,G4_BERYLLIUM_OXIDE,G4_BGO,G4_BLOOD_ICRP,G4_BONE_COMPACT_ICRU,G4_BONE_CORTICAL_ICRP,G4_BORON_CARBIDE,G4_BORON_OXIDE,G4_BRAIN_ICRP,G4_BUTANE,G4_N_BUTYL_ALCOHOL,G4_C_552,+152 more]
FEATURE [App::DocumentObjectGroupPython] H_element113  label="H_element : 062"  # scripted group (container) (typed FeaturePython)
  n = 1
  ref = H_element
FEATURE [App::DocumentObjectGroupPython] G4_H  # scripted group (container) (typed FeaturePython)
  Dunit = g/cm3
  Dvalue = 8.3748e-05
  Group = -> [H_element113]
  conduct = 2
  density = 1
  expand = 3
  formula = H
  name = G4_H
  specific = 4
FEATURE [App::DocumentObjectGroupPython] He_element001  label="He_element : 1"  # scripted group (container) (typed FeaturePython)
  n = 1
  ref = He_element
FEATURE [App::DocumentObjectGroupPython] G4_He  # scripted group (container) (typed FeaturePython)
  Dunit = g/cm3
  Dvalue = 0.000166322
  Group = -> [He_element001]
  conduct = 2
  density = 1
  expand = 3
  formula = He
  name = G4_He
  specific = 4
FEATURE [App::DocumentObjectGroupPython] Li_element008  label="Li_element : 008"  # scripted group (container) (typed FeaturePython)
  n = 1
  ref = Li_element
FEATURE [App::DocumentObjectGroupPython] G4_Li  # scripted group (container) (typed FeaturePython)
  Dunit = g/cm3
  Dvalue = 0.534
  Group = -> [Li_element008]
  conduct = 2
  density = 1
  expand = 3
  formula = Li
  name = G4_Li
  specific = 4
FEATURE [App::DocumentObjectGroupPython] Be_element002  label="Be_element : 002"  # scripted group (container) (typed FeaturePython)
  n = 1
  ref = Be_element
FEATURE [App::DocumentObjectGroupPython] G4_Be  # scripted group (container) (typed FeaturePython)
  Dunit = g/cm3
  Dvalue = 1.848
  Group = -> [Be_element002]
  conduct = 2
  density = 1
  expand = 3
  formula = Be
  name = G4_Be
  specific = 4
FEATURE [App::DocumentObjectGroupPython] B_element007  label="B_element : 007"  # scripted group (container) (typed FeaturePython)
  n = 1
  ref = B_element
FEATURE [App::DocumentObjectGroupPython] G4_B  # scripted group (container) (typed FeaturePython)
  Dunit = g/cm3
  Dvalue = 2.37
  Group = -> [B_element007]
  conduct = 2
  density = 1
  expand = 3
  formula = B
  name = G4_B
  specific = 4
FEATURE [App::DocumentObjectGroupPython] C_element124  label="C_element : 070"  # scripted group (container) (typed FeaturePython)
  n = 1
  ref = C_element
FEATURE [App::DocumentObjectGroupPython] G4_C  # scripted group (container) (typed FeaturePython)
  Dunit = g/cm3
  Dvalue = 2
  Group = -> [C_element124]
  conduct = 2
  density = 1
  expand = 3
  formula = C
  name = G4_C
  specific = 4
FEATURE [App::DocumentObjectGroupPython] N_element048  label="N_element : 021"  # scripted group (container) (typed FeaturePython)
  n = 1
  ref = N_element
FEATURE [App::DocumentObjectGroupPython] G4_N  # scripted group (container) (typed FeaturePython)
  Dunit = g/cm3
  Dvalue = 0.0011652
  Group = -> [N_element048]
  conduct = 2
  density = 1
  expand = 3
  formula = N
  name = G4_N
  specific = 4
FEATURE [App::DocumentObjectGroupPython] O_element105  label="O_element : 059"  # scripted group (container) (typed FeaturePython)
  n = 1
  ref = O_element
FEATURE [App::DocumentObjectGroupPython] G4_O  # scripted group (container) (typed FeaturePython)
  Dunit = g/cm3
  Dvalue = 0.00133151
  Group = -> [O_element105]
  conduct = 2
  density = 1
  expand = 3
  formula = O
  name = G4_O
  specific = 4
FEATURE [App::DocumentObjectGroupPython] F_element019  label="F_element : 008"  # scripted group (container) (typed FeaturePython)
  n = 1
  ref = F_element
FEATURE [App::DocumentObjectGroupPython] G4_F  # scripted group (container) (typed FeaturePython)
  Dunit = g/cm3
  Dvalue = 0.00158029
  Group = -> [F_element019]
  conduct = 2
  density = 1
  expand = 3
  formula = F
  name = G4_F
  specific = 4
FEATURE [App::DocumentObjectGroupPython] Ne_element001  label="Ne_element : 1"  # scripted group (container) (typed FeaturePython)
  n = 1
  ref = Ne_element
FEATURE [App::DocumentObjectGroupPython] G4_Ne  # scripted group (container) (typed FeaturePython)
  Dunit = g/cm3
  Dvalue = 0.000838505
  Group = -> [Ne_element001]
  conduct = 2
  density = 1
  expand = 3
  formula = Ne
  name = G4_Ne
  specific = 4
FEATURE [App::DocumentObjectGroupPython] Na_element020  label="Na_element : 005"  # scripted group (container) (typed FeaturePython)
  n = 1
  ref = Na_element
FEATURE [App::DocumentObjectGroupPython] G4_Na  # scripted group (container) (typed FeaturePython)
  Dunit = g/cm3
  Dvalue = 0.971
  Group = -> [Na_element020]
  conduct = 2
  density = 1
  expand = 3
  formula = Na
  name = G4_Na
  specific = 4
FEATURE [App::DocumentObjectGroupPython] Mg_element011  label="Mg_element : 005"  # scripted group (container) (typed FeaturePython)
  n = 1
  ref = Mg_element
FEATURE [App::DocumentObjectGroupPython] G4_Mg  # scripted group (container) (typed FeaturePython)
  Dunit = g/cm3
  Dvalue = 1.74
  Group = -> [Mg_element011]
  conduct = 2
  density = 1
  expand = 3
  formula = Mg
  name = G4_Mg
  specific = 4
FEATURE [App::DocumentObjectGroupPython] Al_element004  label="Al_element : 1"  # scripted group (container) (typed FeaturePython)
  n = 1
  ref = Al_element
FEATURE [App::DocumentObjectGroupPython] G4_Al  # scripted group (container) (typed FeaturePython)
  Dunit = g/cm3
  Dvalue = 2.699
  Group = -> [Al_element004]
  conduct = 2
  density = 1
  expand = 3
  formula = Al
  name = G4_Al
  specific = 4
FEATURE [App::DocumentObjectGroupPython] Si_element007  label="Si_element : 002"  # scripted group (container) (typed FeaturePython)
  n = 1
  ref = Si_element
FEATURE [App::DocumentObjectGroupPython] G4_Si  # scripted group (container) (typed FeaturePython)
  Dunit = g/cm3
  Dvalue = 2.33
  Group = -> [Si_element007]
  conduct = 2
  density = 1
  expand = 3
  formula = Si
  name = G4_Si
  specific = 4
FEATURE [App::DocumentObjectGroupPython] P_element013  label="P_element : 002"  # scripted group (container) (typed FeaturePython)
  n = 1
  ref = P_element
FEATURE [App::DocumentObjectGroupPython] G4_P  # scripted group (container) (typed FeaturePython)
  Dunit = g/cm3
  Dvalue = 2.2
  Group = -> [P_element013]
  conduct = 2
  density = 1
  expand = 3
  formula = P
  name = G4_P
  specific = 4
FEATURE [App::DocumentObjectGroupPython] S_element023  label="S_element : 007"  # scripted group (container) (typed FeaturePython)
  n = 1
  ref = S_element
FEATURE [App::DocumentObjectGroupPython] G4_S  # scripted group (container) (typed FeaturePython)
  Dunit = g/cm3
  Dvalue = 2
  Group = -> [S_element023]
  conduct = 2
  density = 1
  expand = 3
  formula = S
  name = G4_S
  specific = 4
FEATURE [App::DocumentObjectGroupPython] Cl_element029  label="Cl_element : 015"  # scripted group (container) (typed FeaturePython)
  n = 1
  ref = Cl_element
FEATURE [App::DocumentObjectGroupPython] G4_Cl  # scripted group (container) (typed FeaturePython)
  Dunit = g/cm3
  Dvalue = 0.00299473
  Group = -> [Cl_element029]
  conduct = 2
  density = 1
  expand = 3
  formula = Cl
  name = G4_Cl
  specific = 4
FEATURE [App::DocumentObjectGroupPython] Ar_element002  label="Ar_element : 1"  # scripted group (container) (typed FeaturePython)
  n = 1
  ref = Ar_element
FEATURE [App::DocumentObjectGroupPython] G4_Ar  # scripted group (container) (typed FeaturePython)
  Dunit = g/cm3
  Dvalue = 0.00166201
  Group = -> [Ar_element002]
  conduct = 2
  density = 1
  expand = 3
  formula = Ar
  name = G4_Ar
  specific = 4
FEATURE [App::DocumentObjectGroupPython] K_element013  label="K_element : 003"  # scripted group (container) (typed FeaturePython)
  n = 1
  ref = K_element
FEATURE [App::DocumentObjectGroupPython] G4_K  # scripted group (container) (typed FeaturePython)
  Dunit = g/cm3
  Dvalue = 0.862
  Group = -> [K_element013]
  conduct = 2
  density = 1
  expand = 3
  formula = K
  name = G4_K
  specific = 4
FEATURE [App::DocumentObjectGroupPython] Ca_element014  label="Ca_element : 007"  # scripted group (container) (typed FeaturePython)
  n = 1
  ref = Ca_element
FEATURE [App::DocumentObjectGroupPython] G4_Ca  # scripted group (container) (typed FeaturePython)
  Dunit = g/cm3
  Dvalue = 1.55
  Group = -> [Ca_element014]
  conduct = 2
  density = 1
  expand = 3
  formula = Ca
  name = G4_Ca
  specific = 4
FEATURE [App::DocumentObjectGroupPython] Sc_element001  label="Sc_element : 1"  # scripted group (container) (typed FeaturePython)
  n = 1
  ref = Sc_element
FEATURE [App::DocumentObjectGroupPython] G4_Sc  # scripted group (container) (typed FeaturePython)
  Dunit = g/cm3
  Dvalue = 2.989
  Group = -> [Sc_element001]
  conduct = 2
  density = 1
  expand = 3
  formula = Sc
  name = G4_Sc
  specific = 4
FEATURE [App::DocumentObjectGroupPython] Ti_element004  label="Ti_element : 002"  # scripted group (container) (typed FeaturePython)
  n = 1
  ref = Ti_element
FEATURE [App::DocumentObjectGroupPython] G4_Ti  # scripted group (container) (typed FeaturePython)
  Dunit = g/cm3
  Dvalue = 4.54
  Group = -> [Ti_element004]
  conduct = 2
  density = 1
  expand = 3
  formula = Ti
  name = G4_Ti
  specific = 4
FEATURE [App::DocumentObjectGroupPython] V_element001  label="V_element : 1"  # scripted group (container) (typed FeaturePython)
  n = 1
  ref = V_element
FEATURE [App::DocumentObjectGroupPython] G4_V  # scripted group (container) (typed FeaturePython)
  Dunit = g/cm3
  Dvalue = 6.11
  Group = -> [V_element001]
  conduct = 2
  density = 1
  expand = 3
  formula = V
  name = G4_V
  specific = 4
FEATURE [App::DocumentObjectGroupPython] Cr_element001  label="Cr_element : 1"  # scripted group (container) (typed FeaturePython)
  n = 1
  ref = Cr_element
FEATURE [App::DocumentObjectGroupPython] G4_Cr  # scripted group (container) (typed FeaturePython)
  Dunit = g/cm3
  Dvalue = 7.18
  Group = -> [Cr_element001]
  conduct = 2
  density = 1
  expand = 3
  formula = Cr
  name = G4_Cr
  specific = 4
FEATURE [App::DocumentObjectGroupPython] Mn_element001  label="Mn_element : 1"  # scripted group (container) (typed FeaturePython)
  n = 1
  ref = Mn_element
FEATURE [App::DocumentObjectGroupPython] G4_Mn  # scripted group (container) (typed FeaturePython)
  Dunit = g/cm3
  Dvalue = 7.44
  Group = -> [Mn_element001]
  conduct = 2
  density = 1
  expand = 3
  formula = Mn
  name = G4_Mn
  specific = 4
FEATURE [App::DocumentObjectGroupPython] Fe_element007  label="Fe_element : 004"  # scripted group (container) (typed FeaturePython)
  n = 1
  ref = Fe_element
FEATURE [App::DocumentObjectGroupPython] G4_Fe  # scripted group (container) (typed FeaturePython)
  Dunit = g/cm3
  Dvalue = 7.874
  Group = -> [Fe_element007]
  conduct = 2
  density = 1
  expand = 3
  formula = Fe
  name = G4_Fe
  specific = 4
FEATURE [App::DocumentObjectGroupPython] Co_element001  label="Co_element : 1"  # scripted group (container) (typed FeaturePython)
  n = 1
  ref = Co_element
FEATURE [App::DocumentObjectGroupPython] G4_Co  # scripted group (container) (typed FeaturePython)
  Dunit = g/cm3
  Dvalue = 8.9
  Group = -> [Co_element001]
  conduct = 2
  density = 1
  expand = 3
  formula = Co
  name = G4_Co
  specific = 4
FEATURE [App::DocumentObjectGroupPython] Ni_element001  label="Ni_element : 1"  # scripted group (container) (typed FeaturePython)
  n = 1
  ref = Ni_element
FEATURE [App::DocumentObjectGroupPython] G4_Ni  # scripted group (container) (typed FeaturePython)
  Dunit = g/cm3
  Dvalue = 8.902
  Group = -> [Ni_element001]
  conduct = 2
  density = 1
  expand = 3
  formula = Ni
  name = G4_Ni
  specific = 4
FEATURE [App::DocumentObjectGroupPython] Cu_element001  label="Cu_element : 1"  # scripted group (container) (typed FeaturePython)
  n = 1
  ref = Cu_element
FEATURE [App::DocumentObjectGroupPython] G4_Cu  # scripted group (container) (typed FeaturePython)
  Dunit = g/cm3
  Dvalue = 8.96
  Group = -> [Cu_element001]
  conduct = 2
  density = 1
  expand = 3
  formula = Cu
  name = G4_Cu
  specific = 4
FEATURE [App::DocumentObjectGroupPython] Zn_element001  label="Zn_element : 1"  # scripted group (container) (typed FeaturePython)
  n = 1
  ref = Zn_element
FEATURE [App::DocumentObjectGroupPython] G4_Zn  # scripted group (container) (typed FeaturePython)
  Dunit = g/cm3
  Dvalue = 7.133
  Group = -> [Zn_element001]
  conduct = 2
  density = 1
  expand = 3
  formula = Zn
  name = G4_Zn
  specific = 4
FEATURE [App::DocumentObjectGroupPython] Ga_element002  label="Ga_element : 002"  # scripted group (container) (typed FeaturePython)
  n = 1
  ref = Ga_element
FEATURE [App::DocumentObjectGroupPython] G4_Ga  # scripted group (container) (typed FeaturePython)
  Dunit = g/cm3
  Dvalue = 5.904
  Group = -> [Ga_element002]
  conduct = 2
  density = 1
  expand = 3
  formula = Ga
  name = G4_Ga
  specific = 4
FEATURE [App::DocumentObjectGroupPython] Ge_element002  label="Ge_element : 1"  # scripted group (container) (typed FeaturePython)
  n = 1
  ref = Ge_element
FEATURE [App::DocumentObjectGroupPython] G4_Ge  # scripted group (container) (typed FeaturePython)
  Dunit = g/cm3
  Dvalue = 5.323
  Group = -> [Ge_element002]
  conduct = 2
  density = 1
  expand = 3
  formula = Ge
  name = G4_Ge
  specific = 4
FEATURE [App::DocumentObjectGroupPython] As_element003  label="As_element : 002"  # scripted group (container) (typed FeaturePython)
  n = 1
  ref = As_element
FEATURE [App::DocumentObjectGroupPython] G4_As  # scripted group (container) (typed FeaturePython)
  Dunit = g/cm3
  Dvalue = 5.73
  Group = -> [As_element003]
  conduct = 2
  density = 1
  expand = 3
  formula = As
  name = G4_As
  specific = 4
FEATURE [App::DocumentObjectGroupPython] Se_element001  label="Se_element : 1"  # scripted group (container) (typed FeaturePython)
  n = 1
  ref = Se_element
FEATURE [App::DocumentObjectGroupPython] G4_Se  # scripted group (container) (typed FeaturePython)
  Dunit = g/cm3
  Dvalue = 4.5
  Group = -> [Se_element001]
  conduct = 2
  density = 1
  expand = 3
  formula = Se
  name = G4_Se
  specific = 4
FEATURE [App::DocumentObjectGroupPython] Br_element007  label="Br_element : 004"  # scripted group (container) (typed FeaturePython)
  n = 1
  ref = Br_element
FEATURE [App::DocumentObjectGroupPython] G4_Br  # scripted group (container) (typed FeaturePython)
  Dunit = g/cm3
  Dvalue = 0.0070721
  Group = -> [Br_element007]
  conduct = 2
  density = 1
  expand = 3
  formula = Br
  name = G4_Br
  specific = 4
FEATURE [App::DocumentObjectGroupPython] Kr_element001  label="Kr_element : 1"  # scripted group (container) (typed FeaturePython)
  n = 1
  ref = Kr_element
FEATURE [App::DocumentObjectGroupPython] G4_Kr  # scripted group (container) (typed FeaturePython)
  Dunit = g/cm3
  Dvalue = 0.00347832
  Group = -> [Kr_element001]
  conduct = 2
  density = 1
  expand = 3
  formula = Kr
  name = G4_Kr
  specific = 4
FEATURE [App::DocumentObjectGroupPython] Rb_element001  label="Rb_element : 1"  # scripted group (container) (typed FeaturePython)
  n = 1
  ref = Rb_element
FEATURE [App::DocumentObjectGroupPython] G4_Rb  # scripted group (container) (typed FeaturePython)
  Dunit = g/cm3
  Dvalue = 1.532
  Group = -> [Rb_element001]
  conduct = 2
  density = 1
  expand = 3
  formula = Rb
  name = G4_Rb
  specific = 4
FEATURE [App::DocumentObjectGroupPython] Sr_element001  label="Sr_element : 1"  # scripted group (container) (typed FeaturePython)
  n = 1
  ref = Sr_element
FEATURE [App::DocumentObjectGroupPython] G4_Sr  # scripted group (container) (typed FeaturePython)
  Dunit = g/cm3
  Dvalue = 2.54
  Group = -> [Sr_element001]
  conduct = 2
  density = 1
  expand = 3
  formula = Sr
  name = G4_Sr
  specific = 4
FEATURE [App::DocumentObjectGroupPython] Y_element001  label="Y_element : 1"  # scripted group (container) (typed FeaturePython)
  n = 1
  ref = Y_element
FEATURE [App::DocumentObjectGroupPython] G4_Y  # scripted group (container) (typed FeaturePython)
  Dunit = g/cm3
  Dvalue = 4.469
  Group = -> [Y_element001]
  conduct = 2
  density = 1
  expand = 3
  formula = Y
  name = G4_Y
  specific = 4
FEATURE [App::DocumentObjectGroupPython] Zr_element001  label="Zr_element : 1"  # scripted group (container) (typed FeaturePython)
  n = 1
  ref = Zr_element
FEATURE [App::DocumentObjectGroupPython] G4_Zr  # scripted group (container) (typed FeaturePython)
  Dunit = g/cm3
  Dvalue = 6.506
  Group = -> [Zr_element001]
  conduct = 2
  density = 1
  expand = 3
  formula = Zr
  name = G4_Zr
  specific = 4
FEATURE [App::DocumentObjectGroupPython] Nb_element001  label="Nb_element : 1"  # scripted group (container) (typed FeaturePython)
  n = 1
  ref = Nb_element
FEATURE [App::DocumentObjectGroupPython] G4_Nb  # scripted group (container) (typed FeaturePython)
  Dunit = g/cm3
  Dvalue = 8.57
  Group = -> [Nb_element001]
  conduct = 2
  density = 1
  expand = 3
  formula = Nb
  name = G4_Nb
  specific = 4
FEATURE [App::DocumentObjectGroupPython] Mo_element001  label="Mo_element : 1"  # scripted group (container) (typed FeaturePython)
  n = 1
  ref = Mo_element
FEATURE [App::DocumentObjectGroupPython] G4_Mo  # scripted group (container) (typed FeaturePython)
  Dunit = g/cm3
  Dvalue = 10.22
  Group = -> [Mo_element001]
  conduct = 2
  density = 1
  expand = 3
  formula = Mo
  name = G4_Mo
  specific = 4
FEATURE [App::DocumentObjectGroupPython] Tc_element001  label="Tc_element : 1"  # scripted group (container) (typed FeaturePython)
  n = 1
  ref = Tc_element
FEATURE [App::DocumentObjectGroupPython] G4_Tc  # scripted group (container) (typed FeaturePython)
  Dunit = g/cm3
  Dvalue = 11.5
  Group = -> [Tc_element001]
  conduct = 2
  density = 1
  expand = 3
  formula = Tc
  name = G4_Tc
  specific = 4
FEATURE [App::DocumentObjectGroupPython] Ru_element001  label="Ru_element : 1"  # scripted group (container) (typed FeaturePython)
  n = 1
  ref = Ru_element
FEATURE [App::DocumentObjectGroupPython] G4_Ru  # scripted group (container) (typed FeaturePython)
  Dunit = g/cm3
  Dvalue = 12.41
  Group = -> [Ru_element001]
  conduct = 2
  density = 1
  expand = 3
  formula = Ru
  name = G4_Ru
  specific = 4
FEATURE [App::DocumentObjectGroupPython] Rh_element001  label="Rh_element : 1"  # scripted group (container) (typed FeaturePython)
  n = 1
  ref = Rh_element
FEATURE [App::DocumentObjectGroupPython] G4_Rh  # scripted group (container) (typed FeaturePython)
  Dunit = g/cm3
  Dvalue = 12.41
  Group = -> [Rh_element001]
  conduct = 2
  density = 1
  expand = 3
  formula = Rh
  name = G4_Rh
  specific = 4
FEATURE [App::DocumentObjectGroupPython] Pd_element001  label="Pd_element : 1"  # scripted group (container) (typed FeaturePython)
  n = 1
  ref = Pd_element
FEATURE [App::DocumentObjectGroupPython] G4_Pd  # scripted group (container) (typed FeaturePython)
  Dunit = g/cm3
  Dvalue = 12.02
  Group = -> [Pd_element001]
  conduct = 2
  density = 1
  expand = 3
  formula = Pd
  name = G4_Pd
  specific = 4
FEATURE [App::DocumentObjectGroupPython] Ag_element006  label="Ag_element : 004"  # scripted group (container) (typed FeaturePython)
  n = 1
  ref = Ag_element
FEATURE [App::DocumentObjectGroupPython] G4_Ag  # scripted group (container) (typed FeaturePython)
  Dunit = g/cm3
  Dvalue = 10.5
  Group = -> [Ag_element006]
  conduct = 2
  density = 1
  expand = 3
  formula = Ag
  name = G4_Ag
  specific = 4
FEATURE [App::DocumentObjectGroupPython] Cd_element003  label="Cd_element : 003"  # scripted group (container) (typed FeaturePython)
  n = 1
  ref = Cd_element
FEATURE [App::DocumentObjectGroupPython] G4_Cd  # scripted group (container) (typed FeaturePython)
  Dunit = g/cm3
  Dvalue = 8.65
  Group = -> [Cd_element003]
  conduct = 2
  density = 1
  expand = 3
  formula = Cd
  name = G4_Cd
  specific = 4
FEATURE [App::DocumentObjectGroupPython] In_element001  label="In_element : 1"  # scripted group (container) (typed FeaturePython)
  n = 1
  ref = In_element
FEATURE [App::DocumentObjectGroupPython] G4_In  # scripted group (container) (typed FeaturePython)
  Dunit = g/cm3
  Dvalue = 7.31
  Group = -> [In_element001]
  conduct = 2
  density = 1
  expand = 3
  formula = In
  name = G4_In
  specific = 4
FEATURE [App::DocumentObjectGroupPython] Sn_element001  label="Sn_element : 1"  # scripted group (container) (typed FeaturePython)
  n = 1
  ref = Sn_element
FEATURE [App::DocumentObjectGroupPython] G4_Sn  # scripted group (container) (typed FeaturePython)
  Dunit = g/cm3
  Dvalue = 7.31
  Group = -> [Sn_element001]
  conduct = 2
  density = 1
  expand = 3
  formula = Sn
  name = G4_Sn
  specific = 4
FEATURE [App::DocumentObjectGroupPython] Sb_element001  label="Sb_element : 1"  # scripted group (container) (typed FeaturePython)
  n = 1
  ref = Sb_element
FEATURE [App::DocumentObjectGroupPython] G4_Sb  # scripted group (container) (typed FeaturePython)
  Dunit = g/cm3
  Dvalue = 6.691
  Group = -> [Sb_element001]
  conduct = 2
  density = 1
  expand = 3
  formula = Sb
  name = G4_Sb
  specific = 4
FEATURE [App::DocumentObjectGroupPython] Te_element002  label="Te_element : 002"  # scripted group (container) (typed FeaturePython)
  n = 1
  ref = Te_element
FEATURE [App::DocumentObjectGroupPython] G4_Te  # scripted group (container) (typed FeaturePython)
  Dunit = g/cm3
  Dvalue = 6.24
  Group = -> [Te_element002]
  conduct = 2
  density = 1
  expand = 3
  formula = Te
  name = G4_Te
  specific = 4
FEATURE [App::DocumentObjectGroupPython] I_element010  label="I_element : 006"  # scripted group (container) (typed FeaturePython)
  n = 1
  ref = I_element
FEATURE [App::DocumentObjectGroupPython] G4_I  # scripted group (container) (typed FeaturePython)
  Dunit = g/cm3
  Dvalue = 4.93
  Group = -> [I_element010]
  conduct = 2
  density = 1
  expand = 3
  formula = I
  name = G4_I
  specific = 4
FEATURE [App::DocumentObjectGroupPython] Xe_element001  label="Xe_element : 1"  # scripted group (container) (typed FeaturePython)
  n = 1
  ref = Xe_element
FEATURE [App::DocumentObjectGroupPython] G4_Xe  # scripted group (container) (typed FeaturePython)
  Dunit = g/cm3
  Dvalue = 0.00548536
  Group = -> [Xe_element001]
  conduct = 2
  density = 1
  expand = 3
  formula = Xe
  name = G4_Xe
  specific = 4
FEATURE [App::DocumentObjectGroupPython] Cs_element003  label="Cs_element : 003"  # scripted group (container) (typed FeaturePython)
  n = 1
  ref = Cs_element
FEATURE [App::DocumentObjectGroupPython] G4_Cs  # scripted group (container) (typed FeaturePython)
  Dunit = g/cm3
  Dvalue = 1.873
  Group = -> [Cs_element003]
  conduct = 2
  density = 1
  expand = 3
  formula = Cs
  name = G4_Cs
  specific = 4
FEATURE [App::DocumentObjectGroupPython] Ba_element003  label="Ba_element : 003"  # scripted group (container) (typed FeaturePython)
  n = 1
  ref = Ba_element
FEATURE [App::DocumentObjectGroupPython] G4_Ba  # scripted group (container) (typed FeaturePython)
  Dunit = g/cm3
  Dvalue = 3.5
  Group = -> [Ba_element003]
  conduct = 2
  density = 1
  expand = 3
  formula = Ba
  name = G4_Ba
  specific = 4
FEATURE [App::DocumentObjectGroupPython] La_element003  label="La_element : 003"  # scripted group (container) (typed FeaturePython)
  n = 1
  ref = La_element
FEATURE [App::DocumentObjectGroupPython] G4_La  # scripted group (container) (typed FeaturePython)
  Dunit = g/cm3
  Dvalue = 6.154
  Group = -> [La_element003]
  conduct = 2
  density = 1
  expand = 3
  formula = La
  name = G4_La
  specific = 4
FEATURE [App::DocumentObjectGroupPython] Ce_element002  label="Ce_element : 1"  # scripted group (container) (typed FeaturePython)
  n = 1
  ref = Ce_element
FEATURE [App::DocumentObjectGroupPython] G4_Ce  # scripted group (container) (typed FeaturePython)
  Dunit = g/cm3
  Dvalue = 6.657
  Group = -> [Ce_element002]
  conduct = 2
  density = 1
  expand = 3
  formula = Ce
  name = G4_Ce
  specific = 4
FEATURE [App::DocumentObjectGroupPython] Pr_element001  label="Pr_element : 1"  # scripted group (container) (typed FeaturePython)
  n = 1
  ref = Pr_element
FEATURE [App::DocumentObjectGroupPython] G4_Pr  # scripted group (container) (typed FeaturePython)
  Dunit = g/cm3
  Dvalue = 6.71
  Group = -> [Pr_element001]
  conduct = 2
  density = 1
  expand = 3
  formula = Pr
  name = G4_Pr
  specific = 4
FEATURE [App::DocumentObjectGroupPython] Nd_element001  label="Nd_element : 1"  # scripted group (container) (typed FeaturePython)
  n = 1
  ref = Nd_element
FEATURE [App::DocumentObjectGroupPython] G4_Nd  # scripted group (container) (typed FeaturePython)
  Dunit = g/cm3
  Dvalue = 6.9
  Group = -> [Nd_element001]
  conduct = 2
  density = 1
  expand = 3
  formula = Nd
  name = G4_Nd
  specific = 4
FEATURE [App::DocumentObjectGroupPython] Pm_element001  label="Pm_element : 1"  # scripted group (container) (typed FeaturePython)
  n = 1
  ref = Pm_element
FEATURE [App::DocumentObjectGroupPython] G4_Pm  # scripted group (container) (typed FeaturePython)
  Dunit = g/cm3
  Dvalue = 7.22
  Group = -> [Pm_element001]
  conduct = 2
  density = 1
  expand = 3
  formula = Pm
  name = G4_Pm
  specific = 4
FEATURE [App::DocumentObjectGroupPython] Sm_element001  label="Sm_element : 1"  # scripted group (container) (typed FeaturePython)
  n = 1
  ref = Sm_element
FEATURE [App::DocumentObjectGroupPython] G4_Sm  # scripted group (container) (typed FeaturePython)
  Dunit = g/cm3
  Dvalue = 7.46
  Group = -> [Sm_element001]
  conduct = 2
  density = 1
  expand = 3
  formula = Sm
  name = G4_Sm
  specific = 4
FEATURE [App::DocumentObjectGroupPython] Eu_element001  label="Eu_element : 1"  # scripted group (container) (typed FeaturePython)
  n = 1
  ref = Eu_element
FEATURE [App::DocumentObjectGroupPython] G4_Eu  # scripted group (container) (typed FeaturePython)
  Dunit = g/cm3
  Dvalue = 5.243
  Group = -> [Eu_element001]
  conduct = 2
  density = 1
  expand = 3
  formula = Eu
  name = G4_Eu
  specific = 4
FEATURE [App::DocumentObjectGroupPython] Gd_element002  label="Gd_element : 1"  # scripted group (container) (typed FeaturePython)
  n = 1
  ref = Gd_element
FEATURE [App::DocumentObjectGroupPython] G4_Gd  # scripted group (container) (typed FeaturePython)
  Dunit = g/cm3
  Dvalue = 7.9004
  Group = -> [Gd_element002]
  conduct = 2
  density = 1
  expand = 3
  formula = Gd
  name = G4_Gd
  specific = 4
FEATURE [App::DocumentObjectGroupPython] Tb_element001  label="Tb_element : 1"  # scripted group (container) (typed FeaturePython)
  n = 1
  ref = Tb_element
FEATURE [App::DocumentObjectGroupPython] G4_Tb  # scripted group (container) (typed FeaturePython)
  Dunit = g/cm3
  Dvalue = 8.229
  Group = -> [Tb_element001]
  conduct = 2
  density = 1
  expand = 3
  formula = Tb
  name = G4_Tb
  specific = 4
FEATURE [App::DocumentObjectGroupPython] Dy_element001  label="Dy_element : 1"  # scripted group (container) (typed FeaturePython)
  n = 1
  ref = Dy_element
FEATURE [App::DocumentObjectGroupPython] G4_Dy  # scripted group (container) (typed FeaturePython)
  Dunit = g/cm3
  Dvalue = 8.55
  Group = -> [Dy_element001]
  conduct = 2
  density = 1
  expand = 3
  formula = Dy
  name = G4_Dy
  specific = 4
FEATURE [App::DocumentObjectGroupPython] Ho_element001  label="Ho_element : 1"  # scripted group (container) (typed FeaturePython)
  n = 1
  ref = Ho_element
FEATURE [App::DocumentObjectGroupPython] G4_Ho  # scripted group (container) (typed FeaturePython)
  Dunit = g/cm3
  Dvalue = 8.795
  Group = -> [Ho_element001]
  conduct = 2
  density = 1
  expand = 3
  formula = Ho
  name = G4_Ho
  specific = 4
FEATURE [App::DocumentObjectGroupPython] Er_element001  label="Er_element : 1"  # scripted group (container) (typed FeaturePython)
  n = 1
  ref = Er_element
FEATURE [App::DocumentObjectGroupPython] G4_Er  # scripted group (container) (typed FeaturePython)
  Dunit = g/cm3
  Dvalue = 9.066
  Group = -> [Er_element001]
  conduct = 2
  density = 1
  expand = 3
  formula = Er
  name = G4_Er
  specific = 4
FEATURE [App::DocumentObjectGroupPython] Tm_element001  label="Tm_element : 1"  # scripted group (container) (typed FeaturePython)
  n = 1
  ref = Tm_element
FEATURE [App::DocumentObjectGroupPython] G4_Tm  # scripted group (container) (typed FeaturePython)
  Dunit = g/cm3
  Dvalue = 9.321
  Group = -> [Tm_element001]
  conduct = 2
  density = 1
  expand = 3
  formula = Tm
  name = G4_Tm
  specific = 4
FEATURE [App::DocumentObjectGroupPython] Yb_element001  label="Yb_element : 1"  # scripted group (container) (typed FeaturePython)
  n = 1
  ref = Yb_element
FEATURE [App::DocumentObjectGroupPython] G4_Yb  # scripted group (container) (typed FeaturePython)
  Dunit = g/cm3
  Dvalue = 6.73
  Group = -> [Yb_element001]
  conduct = 2
  density = 1
  expand = 3
  formula = Yb
  name = G4_Yb
  specific = 4
FEATURE [App::DocumentObjectGroupPython] Lu_element001  label="Lu_element : 1"  # scripted group (container) (typed FeaturePython)
  n = 1
  ref = Lu_element
FEATURE [App::DocumentObjectGroupPython] G4_Lu  # scripted group (container) (typed FeaturePython)
  Dunit = g/cm3
  Dvalue = 9.84
  Group = -> [Lu_element001]
  conduct = 2
  density = 1
  expand = 3
  formula = Lu
  name = G4_Lu
  specific = 4
FEATURE [App::DocumentObjectGroupPython] Hf_element001  label="Hf_element : 1"  # scripted group (container) (typed FeaturePython)
  n = 1
  ref = Hf_element
FEATURE [App::DocumentObjectGroupPython] G4_Hf  # scripted group (container) (typed FeaturePython)
  Dunit = g/cm3
  Dvalue = 13.31
  Group = -> [Hf_element001]
  conduct = 2
  density = 1
  expand = 3
  formula = Hf
  name = G4_Hf
  specific = 4
FEATURE [App::DocumentObjectGroupPython] Ta_element001  label="Ta_element : 1"  # scripted group (container) (typed FeaturePython)
  n = 1
  ref = Ta_element
FEATURE [App::DocumentObjectGroupPython] G4_Ta  # scripted group (container) (typed FeaturePython)
  Dunit = g/cm3
  Dvalue = 16.654
  Group = -> [Ta_element001]
  conduct = 2
  density = 1
  expand = 3
  formula = Ta
  name = G4_Ta
  specific = 4
FEATURE [App::DocumentObjectGroupPython] W_element004  label="W_element : 004"  # scripted group (container) (typed FeaturePython)
  n = 1
  ref = W_element
FEATURE [App::DocumentObjectGroupPython] G4_W  # scripted group (container) (typed FeaturePython)
  Dunit = g/cm3
  Dvalue = 19.3
  Group = -> [W_element004]
  conduct = 2
  density = 1
  expand = 3
  formula = W
  name = G4_W
  specific = 4
FEATURE [App::DocumentObjectGroupPython] Re_element001  label="Re_element : 1"  # scripted group (container) (typed FeaturePython)
  n = 1
  ref = Re_element
FEATURE [App::DocumentObjectGroupPython] G4_Re  # scripted group (container) (typed FeaturePython)
  Dunit = g/cm3
  Dvalue = 21.02
  Group = -> [Re_element001]
  conduct = 2
  density = 1
  expand = 3
  formula = Re
  name = G4_Re
  specific = 4
FEATURE [App::DocumentObjectGroupPython] Os_element001  label="Os_element : 1"  # scripted group (container) (typed FeaturePython)
  n = 1
  ref = Os_element
FEATURE [App::DocumentObjectGroupPython] G4_Os  # scripted group (container) (typed FeaturePython)
  Dunit = g/cm3
  Dvalue = 22.57
  Group = -> [Os_element001]
  conduct = 2
  density = 1
  expand = 3
  formula = Os
  name = G4_Os
  specific = 4
FEATURE [App::DocumentObjectGroupPython] Ir_element001  label="Ir_element : 1"  # scripted group (container) (typed FeaturePython)
  n = 1
  ref = Ir_element
FEATURE [App::DocumentObjectGroupPython] G4_Ir  # scripted group (container) (typed FeaturePython)
  Dunit = g/cm3
  Dvalue = 22.42
  Group = -> [Ir_element001]
  conduct = 2
  density = 1
  expand = 3
  formula = Ir
  name = G4_Ir
  specific = 4
FEATURE [App::DocumentObjectGroupPython] Pt_element001  label="Pt_element : 1"  # scripted group (container) (typed FeaturePython)
  n = 1
  ref = Pt_element
FEATURE [App::DocumentObjectGroupPython] G4_Pt  # scripted group (container) (typed FeaturePython)
  Dunit = g/cm3
  Dvalue = 21.45
  Group = -> [Pt_element001]
  conduct = 2
  density = 1
  expand = 3
  formula = Pt
  name = G4_Pt
  specific = 4
FEATURE [App::DocumentObjectGroupPython] Au_element001  label="Au_element : 1"  # scripted group (container) (typed FeaturePython)
  n = 1
  ref = Au_element
FEATURE [App::DocumentObjectGroupPython] G4_Au  # scripted group (container) (typed FeaturePython)
  Dunit = g/cm3
  Dvalue = 19.32
  Group = -> [Au_element001]
  conduct = 2
  density = 1
  expand = 3
  formula = Au
  name = G4_Au
  specific = 4
FEATURE [App::DocumentObjectGroupPython] Hg_element002  label="Hg_element : 002"  # scripted group (container) (typed FeaturePython)
  n = 1
  ref = Hg_element
FEATURE [App::DocumentObjectGroupPython] G4_Hg  # scripted group (container) (typed FeaturePython)
  Dunit = g/cm3
  Dvalue = 13.546
  Group = -> [Hg_element002]
  conduct = 2
  density = 1
  expand = 3
  formula = Hg
  name = G4_Hg
  specific = 4
FEATURE [App::DocumentObjectGroupPython] Tl_element002  label="Tl_element : 002"  # scripted group (container) (typed FeaturePython)
  n = 1
  ref = Tl_element
FEATURE [App::DocumentObjectGroupPython] G4_Tl  # scripted group (container) (typed FeaturePython)
  Dunit = g/cm3
  Dvalue = 11.72
  Group = -> [Tl_element002]
  conduct = 2
  density = 1
  expand = 3
  formula = Tl
  name = G4_Tl
  specific = 4
FEATURE [App::DocumentObjectGroupPython] Pb_element003  label="Pb_element : 1"  # scripted group (container) (typed FeaturePython)
  n = 1
  ref = Pb_element
FEATURE [App::DocumentObjectGroupPython] G4_Pb  # scripted group (container) (typed FeaturePython)
  Dunit = g/cm3
  Dvalue = 11.35
  Group = -> [Pb_element003]
  conduct = 2
  density = 1
  expand = 3
  formula = Pb
  name = G4_Pb
  specific = 4
FEATURE [App::DocumentObjectGroupPython] Bi_element002  label="Bi_element : 1"  # scripted group (container) (typed FeaturePython)
  n = 1
  ref = Bi_element
FEATURE [App::DocumentObjectGroupPython] G4_Bi  # scripted group (container) (typed FeaturePython)
  Dunit = g/cm3
  Dvalue = 9.747
  Group = -> [Bi_element002]
  conduct = 2
  density = 1
  expand = 3
  formula = Bi
  name = G4_Bi
  specific = 4
FEATURE [App::DocumentObjectGroupPython] Po_element001  label="Po_element : 1"  # scripted group (container) (typed FeaturePython)
  n = 1
  ref = Po_element
FEATURE [App::DocumentObjectGroupPython] G4_Po  # scripted group (container) (typed FeaturePython)
  Dunit = g/cm3
  Dvalue = 9.32
  Group = -> [Po_element001]
  conduct = 2
  density = 1
  expand = 3
  formula = Po
  name = G4_Po
  specific = 4
FEATURE [App::DocumentObjectGroupPython] At_element001  label="At_element : 1"  # scripted group (container) (typed FeaturePython)
  n = 1
  ref = At_element
FEATURE [App::DocumentObjectGroupPython] G4_At  # scripted group (container) (typed FeaturePython)
  Dunit = g/cm3
  Dvalue = 9.32
  Group = -> [At_element001]
  conduct = 2
  density = 1
  expand = 3
  formula = At
  name = G4_At
  specific = 4
FEATURE [App::DocumentObjectGroupPython] Rn_element001  label="Rn_element : 1"  # scripted group (container) (typed FeaturePython)
  n = 1
  ref = Rn_element
FEATURE [App::DocumentObjectGroupPython] G4_Rn  # scripted group (container) (typed FeaturePython)
  Dunit = g/cm3
  Dvalue = 0.00900662
  Group = -> [Rn_element001]
  conduct = 2
  density = 1
  expand = 3
  formula = Rn
  name = G4_Rn
  specific = 4
FEATURE [App::DocumentObjectGroupPython] Fr_element001  label="Fr_element : 1"  # scripted group (container) (typed FeaturePython)
  n = 1
  ref = Fr_element
FEATURE [App::DocumentObjectGroupPython] G4_Fr  # scripted group (container) (typed FeaturePython)
  Dunit = g/cm3
  Dvalue = 1
  Group = -> [Fr_element001]
  conduct = 2
  density = 1
  expand = 3
  formula = Fr
  name = G4_Fr
  specific = 4
FEATURE [App::DocumentObjectGroupPython] Ra_element001  label="Ra_element : 1"  # scripted group (container) (typed FeaturePython)
  n = 1
  ref = Ra_element
FEATURE [App::DocumentObjectGroupPython] G4_Ra  # scripted group (container) (typed FeaturePython)
  Dunit = g/cm3
  Dvalue = 5
  Group = -> [Ra_element001]
  conduct = 2
  density = 1
  expand = 3
  formula = Ra
  name = G4_Ra
  specific = 4
FEATURE [App::DocumentObjectGroupPython] Ac_element001  label="Ac_element : 1"  # scripted group (container) (typed FeaturePython)
  n = 1
  ref = Ac_element
FEATURE [App::DocumentObjectGroupPython] G4_Ac  # scripted group (container) (typed FeaturePython)
  Dunit = g/cm3
  Dvalue = 10.07
  Group = -> [Ac_element001]
  conduct = 2
  density = 1
  expand = 3
  formula = Ac
  name = G4_Ac
  specific = 4
FEATURE [App::DocumentObjectGroupPython] Th_element001  label="Th_element : 1"  # scripted group (container) (typed FeaturePython)
  n = 1
  ref = Th_element
FEATURE [App::DocumentObjectGroupPython] G4_Th  # scripted group (container) (typed FeaturePython)
  Dunit = g/cm3
  Dvalue = 11.72
  Group = -> [Th_element001]
  conduct = 2
  density = 1
  expand = 3
  formula = Th
  name = G4_Th
  specific = 4
FEATURE [App::DocumentObjectGroupPython] Pa_element001  label="Pa_element : 1"  # scripted group (container) (typed FeaturePython)
  n = 1
  ref = Pa_element
FEATURE [App::DocumentObjectGroupPython] G4_Pa  # scripted group (container) (typed FeaturePython)
  Dunit = g/cm3
  Dvalue = 15.37
  Group = -> [Pa_element001]
  conduct = 2
  density = 1
  expand = 3
  formula = Pa
  name = G4_Pa
  specific = 4
FEATURE [App::DocumentObjectGroupPython] U_element004  label="U_element : 004"  # scripted group (container) (typed FeaturePython)
  n = 1
  ref = U_element
FEATURE [App::DocumentObjectGroupPython] G4_U  # scripted group (container) (typed FeaturePython)
  Dunit = g/cm3
  Dvalue = 18.95
  Group = -> [U_element004]
  conduct = 2
  density = 1
  expand = 3
  formula = U
  name = G4_U
  specific = 4
FEATURE [App::DocumentObjectGroupPython] Np_element001  label="Np_element : 1"  # scripted group (container) (typed FeaturePython)
  n = 1
  ref = Np_element
FEATURE [App::DocumentObjectGroupPython] G4_Np  # scripted group (container) (typed FeaturePython)
  Dunit = g/cm3
  Dvalue = 20.25
  Group = -> [Np_element001]
  conduct = 2
  density = 1
  expand = 3
  formula = Np
  name = G4_Np
  specific = 4
FEATURE [App::DocumentObjectGroupPython] Pu_element002  label="Pu_element : 002"  # scripted group (container) (typed FeaturePython)
  n = 1
  ref = Pu_element
FEATURE [App::DocumentObjectGroupPython] G4_Pu  # scripted group (container) (typed FeaturePython)
  Dunit = g/cm3
  Dvalue = 19.84
  Group = -> [Pu_element002]
  conduct = 2
  density = 1
  expand = 3
  formula = Pu
  name = G4_Pu
  specific = 4
FEATURE [App::DocumentObjectGroupPython] Am_element001  label="Am_element : 1"  # scripted group (container) (typed FeaturePython)
  n = 1
  ref = Am_element
FEATURE [App::DocumentObjectGroupPython] G4_Am  # scripted group (container) (typed FeaturePython)
  Dunit = g/cm3
  Dvalue = 13.67
  Group = -> [Am_element001]
  conduct = 2
  density = 1
  expand = 3
  formula = Am
  name = G4_Am
  specific = 4
FEATURE [App::DocumentObjectGroupPython] Cm_element001  label="Cm_element : 1"  # scripted group (container) (typed FeaturePython)
  n = 1
  ref = Cm_element
FEATURE [App::DocumentObjectGroupPython] G4_Cm  # scripted group (container) (typed FeaturePython)
  Dunit = g/cm3
  Dvalue = 13.51
  Group = -> [Cm_element001]
  conduct = 2
  density = 1
  expand = 3
  formula = Cm
  name = G4_Cm
  specific = 4
FEATURE [App::DocumentObjectGroupPython] Bk_element001  label="Bk_element : 1"  # scripted group (container) (typed FeaturePython)
  n = 1
  ref = Bk_element
FEATURE [App::DocumentObjectGroupPython] G4_Bk  # scripted group (container) (typed FeaturePython)
  Dunit = g/cm3
  Dvalue = 14
  Group = -> [Bk_element001]
  conduct = 2
  density = 1
  expand = 3
  formula = Bk
  name = G4_Bk
  specific = 4
FEATURE [App::DocumentObjectGroupPython] Cf_element001  label="Cf_element : 1"  # scripted group (container) (typed FeaturePython)
  n = 1
  ref = Cf_element
FEATURE [App::DocumentObjectGroupPython] G4_Cf  # scripted group (container) (typed FeaturePython)
  Dunit = g/cm3
  Dvalue = 10
  Group = -> [Cf_element001]
  conduct = 2
  density = 1
  expand = 3
  formula = Cf
  name = G4_Cf
  specific = 4
FEATURE [App::DocumentObjectGroupPython] Element  # scripted group (container) (typed FeaturePython)
  Group = -> [G4_H,G4_He,G4_Li,G4_Be,G4_B,G4_C,G4_N,G4_O,G4_F,G4_Ne,G4_Na,G4_Mg,G4_Al,G4_Si,G4_P,G4_S,G4_Cl,G4_Ar,G4_K,G4_Ca,G4_Sc,G4_Ti,G4_V,G4_Cr,G4_Mn,G4_Fe,G4_Co,G4_Ni,G4_Cu,G4_Zn,G4_Ga,G4_Ge,G4_As,G4_Se,G4_Br,G4_Kr,G4_Rb,G4_Sr,G4_Y,G4_Zr,G4_Nb,G4_Mo,G4_Tc,G4_Ru,G4_Rh,G4_Pd,G4_Ag,G4_Cd,G4_In,G4_Sn,G4_Sb,G4_Te,G4_I,G4_Xe,G4_Cs,G4_Ba,G4_La,G4_Ce,G4_Pr,G4_Nd,G4_Pm,G4_Sm,G4_Eu,G4_Gd,G4_Tb,G4_Dy,G4_Ho,G4_Er,+30 more]
FEATURE [App::DocumentObjectGroupPython] H_element114  label="H_element : 063"  # scripted group (container) (typed FeaturePython)
  n = 2
  ref = H_element
FEATURE [App::DocumentObjectGroupPython] G4_lH2  # scripted group (container) (typed FeaturePython)
  Dunit = g/cm3
  Dvalue = 0.0708
  Group = -> [H_element114]
  conduct = 2
  density = 1
  expand = 3
  formula = G4_lH2
  name = G4_lH2
  specific = 4
FEATURE [App::DocumentObjectGroupPython] N_element049  label="N_element : 022"  # scripted group (container) (typed FeaturePython)
  n = 2
  ref = N_element
FEATURE [App::DocumentObjectGroupPython] G4_lN2  # scripted group (container) (typed FeaturePython)
  Dunit = g/cm3
  Dvalue = 0.807
  Group = -> [N_element049]
  conduct = 2
  density = 1
  expand = 3
  formula = G4_lN2
  name = G4_lN2
  specific = 4
FEATURE [App::DocumentObjectGroupPython] O_element106  label="O_element : 060"  # scripted group (container) (typed FeaturePython)
  n = 2
  ref = O_element
FEATURE [App::DocumentObjectGroupPython] G4_lO2  # scripted group (container) (typed FeaturePython)
  Dunit = g/cm3
  Dvalue = 1.141
  Group = -> [O_element106]
  conduct = 2
  density = 1
  expand = 3
  formula = G4_lO2
  name = G4_lO2
  specific = 4
FEATURE [App::DocumentObjectGroupPython] Ar  label="Ar : 1"  # scripted group (container) (typed FeaturePython)
  n = 1
  ref = Ar
FEATURE [App::DocumentObjectGroupPython] G4_lAr  # scripted group (container) (typed FeaturePython)
  Dunit = g/cm3
  Dvalue = 1.396
  Group = -> [Ar]
  conduct = 2
  density = 1
  expand = 3
  formula = G4_lAr
  name = G4_lAr
  specific = 4
FEATURE [App::DocumentObjectGroupPython] Br  label="Br : 1"  # scripted group (container) (typed FeaturePython)
  n = 1
  ref = Br
FEATURE [App::DocumentObjectGroupPython] G4_lBr  # scripted group (container) (typed FeaturePython)
  Dunit = g/cm3
  Dvalue = 3.1028
  Group = -> [Br]
  conduct = 2
  density = 1
  expand = 3
  formula = G4_lBr
  name = G4_lBr
  specific = 4
FEATURE [App::DocumentObjectGroupPython] Kr  label="Kr : 1"  # scripted group (container) (typed FeaturePython)
  n = 1
  ref = Kr
FEATURE [App::DocumentObjectGroupPython] G4_lKr  # scripted group (container) (typed FeaturePython)
  Dunit = g/cm3
  Dvalue = 2.418
  Group = -> [Kr]
  conduct = 2
  density = 1
  expand = 3
  formula = G4_lKr
  name = G4_lKr
  specific = 4
FEATURE [App::DocumentObjectGroupPython] Xe  label="Xe : 1"  # scripted group (container) (typed FeaturePython)
  n = 1
  ref = Xe
FEATURE [App::DocumentObjectGroupPython] G4_lXe  # scripted group (container) (typed FeaturePython)
  Dunit = g/cm3
  Dvalue = 2.953
  Group = -> [Xe]
  conduct = 2
  density = 1
  expand = 3
  formula = G4_lXe
  name = G4_lXe
  specific = 4
FEATURE [App::DocumentObjectGroupPython] O_element107  label="O_element : 061"  # scripted group (container) (typed FeaturePython)
  n = 4
  ref = O_element
FEATURE [App::DocumentObjectGroupPython] Pb_element004  label="Pb_element : 002"  # scripted group (container) (typed FeaturePython)
  n = 1
  ref = Pb_element
FEATURE [App::DocumentObjectGroupPython] W_element005  label="W_element : 005"  # scripted group (container) (typed FeaturePython)
  n = 1
  ref = W_element
FEATURE [App::DocumentObjectGroupPython] G4_PbWO4  # scripted group (container) (typed FeaturePython)
  Dunit = g/cm3
  Dvalue = 8.28
  Group = -> [O_element107,Pb_element004,W_element005]
  conduct = 2
  density = 1
  expand = 3
  formula = G4_PbWO4
  name = G4_PbWO4
  specific = 4
FEATURE [App::DocumentObjectGroupPython] alactic  label="alactic : 1"  # scripted group (container) (typed FeaturePython)
  n = 1
  ref = alactic
FEATURE [App::DocumentObjectGroupPython] G4_Galactic  # scripted group (container) (typed FeaturePython)
  Dunit = g/cm3
  Dvalue = 0
  Group = -> [alactic]
  conduct = 2
  density = 1
  expand = 3
  formula = G4_Galactic
  name = G4_Galactic
  specific = 4
FEATURE [App::DocumentObjectGroupPython] RAPHITE_POROUS  label="RAPHITE_POROUS : 1"  # scripted group (container) (typed FeaturePython)
  n = 1
  ref = RAPHITE_POROUS
FEATURE [App::DocumentObjectGroupPython] G4_GRAPHITE_POROUS  # scripted group (container) (typed FeaturePython)
  Dunit = g/cm3
  Dvalue = 1.7
  Group = -> [RAPHITE_POROUS]
  conduct = 2
  density = 1
  expand = 3
  formula = G4_GRAPHITE_POROUS
  name = G4_GRAPHITE_POROUS
  specific = 4
FEATURE [App::DocumentObjectGroupPython] H_element115  label="H_element : 0.150"  # scripted group (container) (typed FeaturePython)
  n = 0.080538
FEATURE [App::DocumentObjectGroupPython] C_element125  label="C_element : 0.600"  # scripted group (container) (typed FeaturePython)
  n = 0.599848
FEATURE [App::DocumentObjectGroupPython] O_element108  label="O_element : 0.320"  # scripted group (container) (typed FeaturePython)
  n = 0.319614
FEATURE [App::DocumentObjectGroupPython] G4_LUCITE  # scripted group (container) (typed FeaturePython)
  Dunit = g/cm3
  Dvalue = 1.19
  Group = -> [H_element115,C_element125,O_element108]
  conduct = 2
  density = 1
  expand = 3
  formula = G4_LUCITE
  name = G4_LUCITE
  specific = 4
FEATURE [App::DocumentObjectGroupPython] Cu_element002  label="Cu_element : 62"  # scripted group (container) (typed FeaturePython)
  n = 62
  ref = Cu_element
FEATURE [App::DocumentObjectGroupPython] Zn_element002  label="Zn_element : 35"  # scripted group (container) (typed FeaturePython)
  n = 35
  ref = Zn_element
FEATURE [App::DocumentObjectGroupPython] Pb_element005  label="Pb_element : 3"  # scripted group (container) (typed FeaturePython)
  n = 3
  ref = Pb_element
FEATURE [App::DocumentObjectGroupPython] G4_BRASS  # scripted group (container) (typed FeaturePython)
  Dunit = g/cm3
  Dvalue = 8.52
  Group = -> [Cu_element002,Zn_element002,Pb_element005]
  conduct = 2
  density = 1
  expand = 3
  formula = G4_BRASS
  name = G4_BRASS
  specific = 4
FEATURE [App::DocumentObjectGroupPython] Cu_element003  label="Cu_element : 89"  # scripted group (container) (typed FeaturePython)
  n = 89
  ref = Cu_element
FEATURE [App::DocumentObjectGroupPython] Zn_element003  label="Zn_element : 9"  # scripted group (container) (typed FeaturePython)
  n = 9
  ref = Zn_element
FEATURE [App::DocumentObjectGroupPython] Pb_element006  label="Pb_element : 2"  # scripted group (container) (typed FeaturePython)
  n = 2
  ref = Pb_element
FEATURE [App::DocumentObjectGroupPython] G4_BRONZE  # scripted group (container) (typed FeaturePython)
  Dunit = g/cm3
  Dvalue = 8.82
  Group = -> [Cu_element003,Zn_element003,Pb_element006]
  conduct = 2
  density = 1
  expand = 3
  formula = G4_BRONZE
  name = G4_BRONZE
  specific = 4
FEATURE [App::DocumentObjectGroupPython] Fe_element008  label="Fe_element : 74"  # scripted group (container) (typed FeaturePython)
  n = 74
  ref = Fe_element
FEATURE [App::DocumentObjectGroupPython] Cr_element002  label="Cr_element : 18"  # scripted group (container) (typed FeaturePython)
  n = 18
  ref = Cr_element
FEATURE [App::DocumentObjectGroupPython] Ni_element002  label="Ni_element : 8"  # scripted group (container) (typed FeaturePython)
  n = 8
  ref = Ni_element
FEATURE [App::DocumentObjectGroupPython] G4_STAINLESS_STEEL  label="G4_STAINLESS-STEEL"  # scripted group (container) (typed FeaturePython)
  Dunit = g/cm3
  Dvalue = 8
  Group = -> [Fe_element008,Cr_element002,Ni_element002]
  conduct = 2
  density = 1
  expand = 3
  formula = G4_STAINLESS-STEEL
  name = G4_STAINLESS-STEEL
  specific = 4
FEATURE [App::DocumentObjectGroupPython] H_element116  label="H_element : 064"  # scripted group (container) (typed FeaturePython)
  n = 18
  ref = H_element
FEATURE [App::DocumentObjectGroupPython] C_element126  label="C_element : 071"  # scripted group (container) (typed FeaturePython)
  n = 12
  ref = C_element
FEATURE [App::DocumentObjectGroupPython] O_element109  label="O_element : 062"  # scripted group (container) (typed FeaturePython)
  n = 7
  ref = O_element
FEATURE [App::DocumentObjectGroupPython] G4_CR39  # scripted group (container) (typed FeaturePython)
  Dunit = g/cm3
  Dvalue = 1.32
  Group = -> [H_element116,C_element126,O_element109]
  conduct = 2
  density = 1
  expand = 3
  formula = G4_CR39
  name = G4_CR39
  specific = 4
FEATURE [App::DocumentObjectGroupPython] H_element117  label="H_element : 38"  # scripted group (container) (typed FeaturePython)
  n = 38
  ref = H_element
FEATURE [App::DocumentObjectGroupPython] C_element127  label="C_element : 072"  # scripted group (container) (typed FeaturePython)
  n = 18
  ref = C_element
FEATURE [App::DocumentObjectGroupPython] O_element110  label="O_element : 063"  # scripted group (container) (typed FeaturePython)
  n = 1
  ref = O_element
FEATURE [App::DocumentObjectGroupPython] G4_OCTADECANOL  # scripted group (container) (typed FeaturePython)
  Dunit = g/cm3
  Dvalue = 0.812
  Group = -> [H_element117,C_element127,O_element110]
  conduct = 2
  density = 1
  expand = 3
  formula = G4_OCTADECANOL
  name = G4_OCTADECANOL
  specific = 4
FEATURE [App::DocumentObjectGroupPython] HEP  # scripted group (container) (typed FeaturePython)
  Group = -> [G4_lH2,G4_lN2,G4_lO2,G4_lAr,G4_lBr,G4_lKr,G4_lXe,G4_PbWO4,G4_Galactic,G4_GRAPHITE_POROUS,G4_LUCITE,G4_BRASS,G4_BRONZE,G4_STAINLESS_STEEL,G4_CR39,G4_OCTADECANOL]
FEATURE [App::DocumentObjectGroupPython] C_element128  label="C_element : 073"  # scripted group (container) (typed FeaturePython)
  n = 14
  ref = C_element
FEATURE [App::DocumentObjectGroupPython] H_element118  label="H_element : 065"  # scripted group (container) (typed FeaturePython)
  n = 10
  ref = H_element
FEATURE [App::DocumentObjectGroupPython] O_element111  label="O_element : 064"  # scripted group (container) (typed FeaturePython)
  n = 2
  ref = O_element
FEATURE [App::DocumentObjectGroupPython] N_element050  label="N_element : 023"  # scripted group (container) (typed FeaturePython)
  n = 2
  ref = N_element
FEATURE [App::DocumentObjectGroupPython] G4_KEVLAR  # scripted group (container) (typed FeaturePython)
  Dunit = g/cm3
  Dvalue = 1.44
  Group = -> [C_element128,H_element118,O_element111,N_element050]
  conduct = 2
  density = 1
  expand = 3
  formula = G4_KEVLAR
  name = G4_KEVLAR
  specific = 4
FEATURE [App::DocumentObjectGroupPython] C_element129  label="C_element : 074"  # scripted group (container) (typed FeaturePython)
  n = 10
  ref = C_element
FEATURE [App::DocumentObjectGroupPython] H_element119  label="H_element : 066"  # scripted group (container) (typed FeaturePython)
  n = 8
  ref = H_element
FEATURE [App::DocumentObjectGroupPython] O_element112  label="O_element : 065"  # scripted group (container) (typed FeaturePython)
  n = 4
  ref = O_element
FEATURE [App::DocumentObjectGroupPython] G4_DACRON  # scripted group (container) (typed FeaturePython)
  Dunit = g/cm3
  Dvalue = 1.4
  Group = -> [C_element129,H_element119,O_element112]
  conduct = 2
  density = 1
  expand = 3
  formula = G4_DACRON
  name = G4_DACRON
  specific = 4
FEATURE [App::DocumentObjectGroupPython] C_element130  label="C_element : 075"  # scripted group (container) (typed FeaturePython)
  n = 4
  ref = C_element
FEATURE [App::DocumentObjectGroupPython] H_element120  label="H_element : 067"  # scripted group (container) (typed FeaturePython)
  n = 5
  ref = H_element
FEATURE [App::DocumentObjectGroupPython] Cl_element030  label="Cl_element : 016"  # scripted group (container) (typed FeaturePython)
  n = 1
  ref = Cl_element
FEATURE [App::DocumentObjectGroupPython] G4_NEOPRENE  # scripted group (container) (typed FeaturePython)
  Dunit = g/cm3
  Dvalue = 1.23
  Group = -> [C_element130,H_element120,Cl_element030]
  conduct = 2
  density = 1
  expand = 3
  formula = G4_NEOPRENE
  name = G4_NEOPRENE
  specific = 4
FEATURE [App::DocumentObjectGroupPython] Space  # scripted group (container) (typed FeaturePython)
  Group = -> [G4_KEVLAR,G4_DACRON,G4_NEOPRENE]
FEATURE [App::DocumentObjectGroupPython] H_element121  label="H_element : 068"  # scripted group (container) (typed FeaturePython)
  n = 5
  ref = H_element
FEATURE [App::DocumentObjectGroupPython] C_element131  label="C_element : 076"  # scripted group (container) (typed FeaturePython)
  n = 4
  ref = C_element
FEATURE [App::DocumentObjectGroupPython] N_element051  label="N_element : 3"  # scripted group (container) (typed FeaturePython)
  n = 3
  ref = N_element
FEATURE [App::DocumentObjectGroupPython] O_element113  label="O_element : 066"  # scripted group (container) (typed FeaturePython)
  n = 1
  ref = O_element
FEATURE [App::DocumentObjectGroupPython] G4_CYTOSINE  # scripted group (container) (typed FeaturePython)
  Dunit = g/cm3
  Dvalue = 1.55
  Group = -> [H_element121,C_element131,N_element051,O_element113]
  conduct = 2
  density = 1
  expand = 3
  formula = G4_CYTOSINE
  name = G4_CYTOSINE
  specific = 4
FEATURE [App::DocumentObjectGroupPython] H_element122  label="H_element : 069"  # scripted group (container) (typed FeaturePython)
  n = 6
  ref = H_element
FEATURE [App::DocumentObjectGroupPython] C_element132  label="C_element : 077"  # scripted group (container) (typed FeaturePython)
  n = 5
  ref = C_element
FEATURE [App::DocumentObjectGroupPython] N_element052  label="N_element : 024"  # scripted group (container) (typed FeaturePython)
  n = 2
  ref = N_element
FEATURE [App::DocumentObjectGroupPython] O_element114  label="O_element : 067"  # scripted group (container) (typed FeaturePython)
  n = 2
  ref = O_element
FEATURE [App::DocumentObjectGroupPython] G4_THYMINE  # scripted group (container) (typed FeaturePython)
  Dunit = g/cm3
  Dvalue = 1.23
  Group = -> [H_element122,C_element132,N_element052,O_element114]
  conduct = 2
  density = 1
  expand = 3
  formula = G4_THYMINE
  name = G4_THYMINE
  specific = 4
FEATURE [App::DocumentObjectGroupPython] H_element123  label="H_element : 070"  # scripted group (container) (typed FeaturePython)
  n = 4
  ref = H_element
FEATURE [App::DocumentObjectGroupPython] C_element133  label="C_element : 078"  # scripted group (container) (typed FeaturePython)
  n = 4
  ref = C_element
FEATURE [App::DocumentObjectGroupPython] N_element053  label="N_element : 025"  # scripted group (container) (typed FeaturePython)
  n = 2
  ref = N_element
FEATURE [App::DocumentObjectGroupPython] O_element115  label="O_element : 068"  # scripted group (container) (typed FeaturePython)
  n = 2
  ref = O_element
FEATURE [App::DocumentObjectGroupPython] G4_URACIL  # scripted group (container) (typed FeaturePython)
  Dunit = g/cm3
  Dvalue = 1.32
  Group = -> [H_element123,C_element133,N_element053,O_element115]
  conduct = 2
  density = 1
  expand = 3
  formula = G4_URACIL
  name = G4_URACIL
  specific = 4
FEATURE [App::DocumentObjectGroupPython] H_element124  label="H_element : 071"  # scripted group (container) (typed FeaturePython)
  n = 4
  ref = H_element
FEATURE [App::DocumentObjectGroupPython] C_element134  label="C_element : 079"  # scripted group (container) (typed FeaturePython)
  n = 5
  ref = C_element
FEATURE [App::DocumentObjectGroupPython] N_element054  label="N_element : 026"  # scripted group (container) (typed FeaturePython)
  n = 5
  ref = N_element
FEATURE [App::DocumentObjectGroupPython] G4_DNA_ADENINE  # scripted group (container) (typed FeaturePython)
  Dunit = g/cm3
  Dvalue = 1
  Group = -> [H_element124,C_element134,N_element054]
  conduct = 2
  density = 1
  expand = 3
  formula = G4_DNA_ADENINE
  name = G4_DNA_ADENINE
  specific = 4
FEATURE [App::DocumentObjectGroupPython] H_element125  label="H_element : 072"  # scripted group (container) (typed FeaturePython)
  n = 4
  ref = H_element
FEATURE [App::DocumentObjectGroupPython] C_element135  label="C_element : 080"  # scripted group (container) (typed FeaturePython)
  n = 5
  ref = C_element
FEATURE [App::DocumentObjectGroupPython] N_element055  label="N_element : 027"  # scripted group (container) (typed FeaturePython)
  n = 5
  ref = N_element
FEATURE [App::DocumentObjectGroupPython] O_element116  label="O_element : 069"  # scripted group (container) (typed FeaturePython)
  n = 1
  ref = O_element
FEATURE [App::DocumentObjectGroupPython] G4_DNA_GUANINE  # scripted group (container) (typed FeaturePython)
  Dunit = g/cm3
  Dvalue = 1
  Group = -> [H_element125,C_element135,N_element055,O_element116]
  conduct = 2
  density = 1
  expand = 3
  formula = G4_DNA_GUANINE
  name = G4_DNA_GUANINE
  specific = 4
FEATURE [App::DocumentObjectGroupPython] H_element126  label="H_element : 073"  # scripted group (container) (typed FeaturePython)
  n = 4
  ref = H_element
FEATURE [App::DocumentObjectGroupPython] C_element136  label="C_element : 081"  # scripted group (container) (typed FeaturePython)
  n = 4
  ref = C_element
FEATURE [App::DocumentObjectGroupPython] N_element056  label="N_element : 028"  # scripted group (container) (typed FeaturePython)
  n = 3
  ref = N_element
FEATURE [App::DocumentObjectGroupPython] O_element117  label="O_element : 070"  # scripted group (container) (typed FeaturePython)
  n = 1
  ref = O_element
FEATURE [App::DocumentObjectGroupPython] G4_DNA_CYTOSINE  # scripted group (container) (typed FeaturePython)
  Dunit = g/cm3
  Dvalue = 1
  Group = -> [H_element126,C_element136,N_element056,O_element117]
  conduct = 2
  density = 1
  expand = 3
  formula = G4_DNA_CYTOSINE
  name = G4_DNA_CYTOSINE
  specific = 4
FEATURE [App::DocumentObjectGroupPython] H_element127  label="H_element : 074"  # scripted group (container) (typed FeaturePython)
  n = 5
  ref = H_element
FEATURE [App::DocumentObjectGroupPython] C_element137  label="C_element : 082"  # scripted group (container) (typed FeaturePython)
  n = 5
  ref = C_element
FEATURE [App::DocumentObjectGroupPython] N_element057  label="N_element : 029"  # scripted group (container) (typed FeaturePython)
  n = 2
  ref = N_element
FEATURE [App::DocumentObjectGroupPython] O_element118  label="O_element : 071"  # scripted group (container) (typed FeaturePython)
  n = 2
  ref = O_element
FEATURE [App::DocumentObjectGroupPython] G4_DNA_THYMINE  # scripted group (container) (typed FeaturePython)
  Dunit = g/cm3
  Dvalue = 1
  Group = -> [H_element127,C_element137,N_element057,O_element118]
  conduct = 2
  density = 1
  expand = 3
  formula = G4_DNA_THYMINE
  name = G4_DNA_THYMINE
  specific = 4
FEATURE [App::DocumentObjectGroupPython] H_element128  label="H_element : 075"  # scripted group (container) (typed FeaturePython)
  n = 3
  ref = H_element
FEATURE [App::DocumentObjectGroupPython] C_element138  label="C_element : 083"  # scripted group (container) (typed FeaturePython)
  n = 4
  ref = C_element
FEATURE [App::DocumentObjectGroupPython] N_element058  label="N_element : 030"  # scripted group (container) (typed FeaturePython)
  n = 2
  ref = N_element
FEATURE [App::DocumentObjectGroupPython] O_element119  label="O_element : 072"  # scripted group (container) (typed FeaturePython)
  n = 2
  ref = O_element
FEATURE [App::DocumentObjectGroupPython] G4_DNA_URACIL  # scripted group (container) (typed FeaturePython)
  Dunit = g/cm3
  Dvalue = 1
  Group = -> [H_element128,C_element138,N_element058,O_element119]
  conduct = 2
  density = 1
  expand = 3
  formula = G4_DNA_URACIL
  name = G4_DNA_URACIL
  specific = 4
FEATURE [App::DocumentObjectGroupPython] H_element129  label="H_element : 076"  # scripted group (container) (typed FeaturePython)
  n = 10
  ref = H_element
FEATURE [App::DocumentObjectGroupPython] C_element139  label="C_element : 084"  # scripted group (container) (typed FeaturePython)
  n = 10
  ref = C_element
FEATURE [App::DocumentObjectGroupPython] N_element059  label="N_element : 031"  # scripted group (container) (typed FeaturePython)
  n = 5
  ref = N_element
FEATURE [App::DocumentObjectGroupPython] O_element120  label="O_element : 073"  # scripted group (container) (typed FeaturePython)
  n = 4
  ref = O_element
FEATURE [App::DocumentObjectGroupPython] G4_DNA_ADENOSINE  # scripted group (container) (typed FeaturePython)
  Dunit = g/cm3
  Dvalue = 1
  Group = -> [H_element129,C_element139,N_element059,O_element120]
  conduct = 2
  density = 1
  expand = 3
  formula = G4_DNA_ADENOSINE
  name = G4_DNA_ADENOSINE
  specific = 4
FEATURE [App::DocumentObjectGroupPython] H_element130  label="H_element : 077"  # scripted group (container) (typed FeaturePython)
  n = 10
  ref = H_element
FEATURE [App::DocumentObjectGroupPython] C_element140  label="C_element : 085"  # scripted group (container) (typed FeaturePython)
  n = 10
  ref = C_element
FEATURE [App::DocumentObjectGroupPython] N_element060  label="N_element : 032"  # scripted group (container) (typed FeaturePython)
  n = 5
  ref = N_element
FEATURE [App::DocumentObjectGroupPython] O_element121  label="O_element : 074"  # scripted group (container) (typed FeaturePython)
  n = 5
  ref = O_element
FEATURE [App::DocumentObjectGroupPython] G4_DNA_GUANOSINE  # scripted group (container) (typed FeaturePython)
  Dunit = g/cm3
  Dvalue = 1
  Group = -> [H_element130,C_element140,N_element060,O_element121]
  conduct = 2
  density = 1
  expand = 3
  formula = G4_DNA_GUANOSINE
  name = G4_DNA_GUANOSINE
  specific = 4
FEATURE [App::DocumentObjectGroupPython] H_element131  label="H_element : 078"  # scripted group (container) (typed FeaturePython)
  n = 10
  ref = H_element
FEATURE [App::DocumentObjectGroupPython] C_element141  label="C_element : 086"  # scripted group (container) (typed FeaturePython)
  n = 9
  ref = C_element
FEATURE [App::DocumentObjectGroupPython] N_element061  label="N_element : 033"  # scripted group (container) (typed FeaturePython)
  n = 3
  ref = N_element
FEATURE [App::DocumentObjectGroupPython] O_element122  label="O_element : 075"  # scripted group (container) (typed FeaturePython)
  n = 5
  ref = O_element
FEATURE [App::DocumentObjectGroupPython] G4_DNA_CYTIDINE  # scripted group (container) (typed FeaturePython)
  Dunit = g/cm3
  Dvalue = 1
  Group = -> [H_element131,C_element141,N_element061,O_element122]
  conduct = 2
  density = 1
  expand = 3
  formula = G4_DNA_CYTIDINE
  name = G4_DNA_CYTIDINE
  specific = 4
FEATURE [App::DocumentObjectGroupPython] H_element132  label="H_element : 079"  # scripted group (container) (typed FeaturePython)
  n = 9
  ref = H_element
FEATURE [App::DocumentObjectGroupPython] C_element142  label="C_element : 087"  # scripted group (container) (typed FeaturePython)
  n = 9
  ref = C_element
FEATURE [App::DocumentObjectGroupPython] N_element062  label="N_element : 034"  # scripted group (container) (typed FeaturePython)
  n = 2
  ref = N_element
FEATURE [App::DocumentObjectGroupPython] O_element123  label="O_element : 076"  # scripted group (container) (typed FeaturePython)
  n = 6
  ref = O_element
FEATURE [App::DocumentObjectGroupPython] G4_DNA_URIDINE  # scripted group (container) (typed FeaturePython)
  Dunit = g/cm3
  Dvalue = 1
  Group = -> [H_element132,C_element142,N_element062,O_element123]
  conduct = 2
  density = 1
  expand = 3
  formula = G4_DNA_URIDINE
  name = G4_DNA_URIDINE
  specific = 4
FEATURE [App::DocumentObjectGroupPython] H_element133  label="H_element : 080"  # scripted group (container) (typed FeaturePython)
  n = 11
  ref = H_element
FEATURE [App::DocumentObjectGroupPython] C_element143  label="C_element : 088"  # scripted group (container) (typed FeaturePython)
  n = 10
  ref = C_element
FEATURE [App::DocumentObjectGroupPython] N_element063  label="N_element : 035"  # scripted group (container) (typed FeaturePython)
  n = 2
  ref = N_element
FEATURE [App::DocumentObjectGroupPython] O_element124  label="O_element : 077"  # scripted group (container) (typed FeaturePython)
  n = 6
  ref = O_element
FEATURE [App::DocumentObjectGroupPython] G4_DNA_METHYLURIDINE  # scripted group (container) (typed FeaturePython)
  Dunit = g/cm3
  Dvalue = 1
  Group = -> [H_element133,C_element143,N_element063,O_element124]
  conduct = 2
  density = 1
  expand = 3
  formula = G4_DNA_METHYLURIDINE
  name = G4_DNA_METHYLURIDINE
  specific = 4
FEATURE [App::DocumentObjectGroupPython] P_element014  label="P_element : 003"  # scripted group (container) (typed FeaturePython)
  n = 1
  ref = P_element
FEATURE [App::DocumentObjectGroupPython] O_element125  label="O_element : 078"  # scripted group (container) (typed FeaturePython)
  n = 3
  ref = O_element
FEATURE [App::DocumentObjectGroupPython] G4_DNA_MONOPHOSPHATE  # scripted group (container) (typed FeaturePython)
  Dunit = g/cm3
  Dvalue = 1
  Group = -> [P_element014,O_element125]
  conduct = 2
  density = 1
  expand = 3
  formula = G4_DNA_MONOPHOSPHATE
  name = G4_DNA_MONOPHOSPHATE
  specific = 4
FEATURE [App::DocumentObjectGroupPython] H_element134  label="H_element : 081"  # scripted group (container) (typed FeaturePython)
  n = 10
  ref = H_element
FEATURE [App::DocumentObjectGroupPython] C_element144  label="C_element : 089"  # scripted group (container) (typed FeaturePython)
  n = 10
  ref = C_element
FEATURE [App::DocumentObjectGroupPython] N_element064  label="N_element : 036"  # scripted group (container) (typed FeaturePython)
  n = 5
  ref = N_element
FEATURE [App::DocumentObjectGroupPython] O_element126  label="O_element : 079"  # scripted group (container) (typed FeaturePython)
  n = 7
  ref = O_element
FEATURE [App::DocumentObjectGroupPython] P_element015  label="P_element : 004"  # scripted group (container) (typed FeaturePython)
  n = 1
  ref = P_element
FEATURE [App::DocumentObjectGroupPython] G4_DNA_A  # scripted group (container) (typed FeaturePython)
  Dunit = g/cm3
  Dvalue = 1
  Group = -> [H_element134,C_element144,N_element064,O_element126,P_element015]
  conduct = 2
  density = 1
  expand = 3
  formula = G4_DNA_A
  name = G4_DNA_A
  specific = 4
FEATURE [App::DocumentObjectGroupPython] H_element135  label="H_element : 082"  # scripted group (container) (typed FeaturePython)
  n = 10
  ref = H_element
FEATURE [App::DocumentObjectGroupPython] C_element145  label="C_element : 090"  # scripted group (container) (typed FeaturePython)
  n = 10
  ref = C_element
FEATURE [App::DocumentObjectGroupPython] N_element065  label="N_element : 037"  # scripted group (container) (typed FeaturePython)
  n = 5
  ref = N_element
FEATURE [App::DocumentObjectGroupPython] O_element127  label="O_element : 8"  # scripted group (container) (typed FeaturePython)
  n = 8
  ref = O_element
FEATURE [App::DocumentObjectGroupPython] P_element016  label="P_element : 005"  # scripted group (container) (typed FeaturePython)
  n = 1
  ref = P_element
FEATURE [App::DocumentObjectGroupPython] G4_DNA_G  # scripted group (container) (typed FeaturePython)
  Dunit = g/cm3
  Dvalue = 1
  Group = -> [H_element135,C_element145,N_element065,O_element127,P_element016]
  conduct = 2
  density = 1
  expand = 3
  formula = G4_DNA_G
  name = G4_DNA_G
  specific = 4
FEATURE [App::DocumentObjectGroupPython] H_element136  label="H_element : 083"  # scripted group (container) (typed FeaturePython)
  n = 10
  ref = H_element
FEATURE [App::DocumentObjectGroupPython] C_element146  label="C_element : 091"  # scripted group (container) (typed FeaturePython)
  n = 9
  ref = C_element
FEATURE [App::DocumentObjectGroupPython] N_element066  label="N_element : 038"  # scripted group (container) (typed FeaturePython)
  n = 3
  ref = N_element
FEATURE [App::DocumentObjectGroupPython] O_element128  label="O_element : 080"  # scripted group (container) (typed FeaturePython)
  n = 8
  ref = O_element
FEATURE [App::DocumentObjectGroupPython] P_element017  label="P_element : 006"  # scripted group (container) (typed FeaturePython)
  n = 1
  ref = P_element
FEATURE [App::DocumentObjectGroupPython] G4_DNA_C  # scripted group (container) (typed FeaturePython)
  Dunit = g/cm3
  Dvalue = 1
  Group = -> [H_element136,C_element146,N_element066,O_element128,P_element017]
  conduct = 2
  density = 1
  expand = 3
  formula = G4_DNA_C
  name = G4_DNA_C
  specific = 4
FEATURE [App::DocumentObjectGroupPython] H_element137  label="H_element : 084"  # scripted group (container) (typed FeaturePython)
  n = 9
  ref = H_element
FEATURE [App::DocumentObjectGroupPython] C_element147  label="C_element : 092"  # scripted group (container) (typed FeaturePython)
  n = 9
  ref = C_element
FEATURE [App::DocumentObjectGroupPython] N_element067  label="N_element : 039"  # scripted group (container) (typed FeaturePython)
  n = 2
  ref = N_element
FEATURE [App::DocumentObjectGroupPython] O_element129  label="O_element : 9"  # scripted group (container) (typed FeaturePython)
  n = 9
  ref = O_element
FEATURE [App::DocumentObjectGroupPython] P_element018  label="P_element : 007"  # scripted group (container) (typed FeaturePython)
  n = 1
  ref = P_element
FEATURE [App::DocumentObjectGroupPython] G4_DNA_U  # scripted group (container) (typed FeaturePython)
  Dunit = g/cm3
  Dvalue = 1
  Group = -> [H_element137,C_element147,N_element067,O_element129,P_element018]
  conduct = 2
  density = 1
  expand = 3
  formula = G4_DNA_U
  name = G4_DNA_U
  specific = 4
FEATURE [App::DocumentObjectGroupPython] H_element138  label="H_element : 085"  # scripted group (container) (typed FeaturePython)
  n = 11
  ref = H_element
FEATURE [App::DocumentObjectGroupPython] C_element148  label="C_element : 093"  # scripted group (container) (typed FeaturePython)
  n = 10
  ref = C_element
FEATURE [App::DocumentObjectGroupPython] N_element068  label="N_element : 040"  # scripted group (container) (typed FeaturePython)
  n = 2
  ref = N_element
FEATURE [App::DocumentObjectGroupPython] O_element130  label="O_element : 081"  # scripted group (container) (typed FeaturePython)
  n = 9
  ref = O_element
FEATURE [App::DocumentObjectGroupPython] P_element019  label="P_element : 008"  # scripted group (container) (typed FeaturePython)
  n = 1
  ref = P_element
FEATURE [App::DocumentObjectGroupPython] G4_DNA_MU  # scripted group (container) (typed FeaturePython)
  Dunit = g/cm3
  Dvalue = 1
  Group = -> [H_element138,C_element148,N_element068,O_element130,P_element019]
  conduct = 2
  density = 1
  expand = 3
  formula = G4_DNA_MU
  name = G4_DNA_MU
  specific = 4
FEATURE [App::DocumentObjectGroupPython] BioChemical  # scripted group (container) (typed FeaturePython)
  Group = -> [G4_CYTOSINE,G4_THYMINE,G4_URACIL,G4_DNA_ADENINE,G4_DNA_GUANINE,G4_DNA_CYTOSINE,G4_DNA_THYMINE,G4_DNA_URACIL,G4_DNA_ADENOSINE,G4_DNA_GUANOSINE,G4_DNA_CYTIDINE,G4_DNA_URIDINE,G4_DNA_METHYLURIDINE,G4_DNA_MONOPHOSPHATE,G4_DNA_A,G4_DNA_G,G4_DNA_C,G4_DNA_U,G4_DNA_MU]
FEATURE [App::DocumentObjectGroupPython] G4Materials  # scripted group (container) (typed FeaturePython)
  Group = -> [NIST,Element,HEP,Space,BioChemical]
  version = 1
FEATURE [App::DocumentObjectGroupPython] Geant4  # scripted group (container) (typed FeaturePython)
  Group = -> [G4Isotopes,G4Elements,G4Materials]
FEATURE [App::DocumentObjectGroupPython] Materials  # scripted group (container) (typed FeaturePython)
  Group = -> [Geant4]
FEATURE [Part::FeaturePython] GDMLBox_WorldBox  # WARN: FeaturePython — macro-defined, semantics opaque (R4)
  lunit = 2
  material = 5
  x = 26
  y = 27.5772
  z = 33.0792
FEATURE [Part::Cone] Cone
  Angle = 360
  AttacherType = Attacher::AttachEngine3D
  Height = 2
  Radius1 = 0
  Radius2 = 1
FEATURE [Part::Vertex] Vertex
  AttacherType = Attacher::AttachEngine3D
  Placement = pos=(5,0,0) rot=(0,0,1;0.349066rad)
  X = 0
  Y = 0
  Z = 0
FEATURE [Part::Vertex] Vertex001
  AttacherType = Attacher::AttachEngine3D
  Placement = pos=(5,5,0) rot=(0,0,1;0rad)
  X = 0
  Y = 0
  Z = 0
FEATURE [Part::Vertex] Vertex002
  AttacherType = Attacher::AttachEngine3D
  Placement = pos=(3,3,0) rot=(0,0,1;0rad)
  X = 0
  Y = 0
  Z = 0
FEATURE [Part::Vertex] Vertex003
  AttacherType = Attacher::AttachEngine3D
  X = 0
  Y = 0
  Z = 0
FEATURE [Part::Vertex] Vertex004
  AttacherType = Attacher::AttachEngine3D
  Placement = pos=(0,4,0) rot=(0,0,1;0rad)
  X = 0
  Y = 0
  Z = 0
FEATURE [Part::Compound] Compound
  Links = -> [Vertex,Vertex001,Vertex002,Vertex003,Vertex004]
FEATURE [Part::FeaturePython] PointArray  # Draft array (typed FeaturePython)
  Base = -> Cone
  Count = 5
  Fuse = false
  PointObject = -> Compound
FEATURE [App::Part] Part
  Group = -> [Vertex,Cone,Vertex002,Compound,Vertex003,Vertex004,Vertex001,PointArray]
  Origin = -> Origin001
FEATURE [App::Part] worldVOL
  Group = -> [GDMLBox_WorldBox,Part]
  Origin = -> Origin
